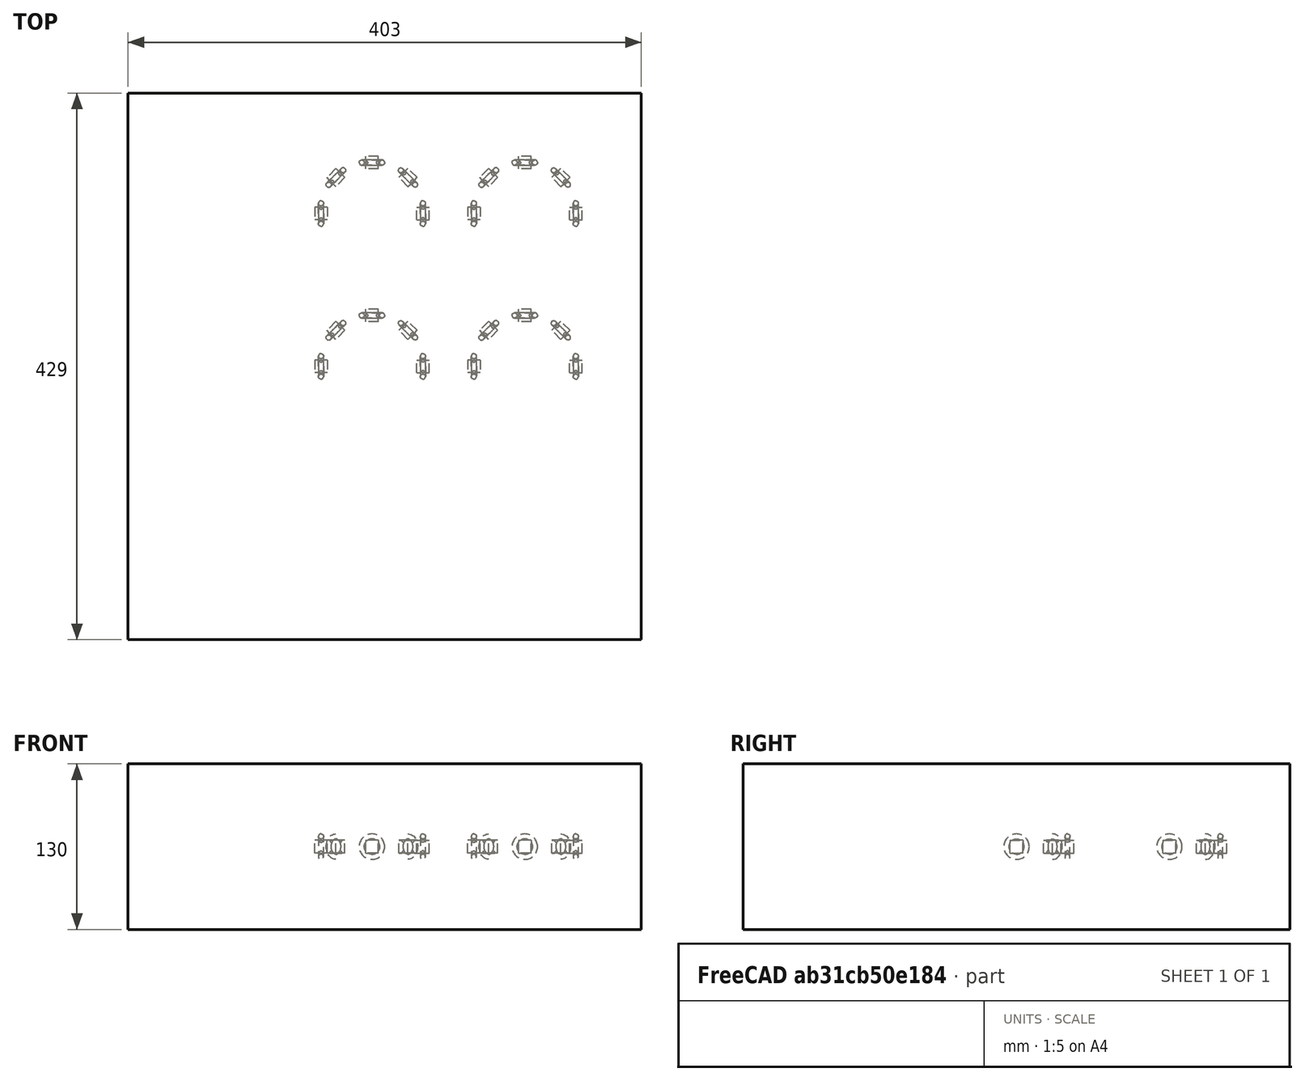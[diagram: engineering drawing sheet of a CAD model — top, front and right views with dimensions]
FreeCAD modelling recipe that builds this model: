
FCSTD DOCUMENT  (FreeCAD 0.21R33694 (Git))
Label: array-of-array-of-solid-offcenter
License: All rights reserved
objects: App::DocumentObjectGroupPython×1251, Part::FeaturePython×5, App::Part×2, Part::MultiFuse×1
note: 5 computed .brp shape members not serialized (recipe doc carries the construction recipe); baked Part::Feature solids carry a one-line shape summary decoded from their .brp

FEATURE [App::DocumentObjectGroupPython] HALFPI  # scripted group (container) (typed FeaturePython)
  name = HALFPI
  value = pi/2.
FEATURE [App::DocumentObjectGroupPython] PI  # scripted group (container) (typed FeaturePython)
  name = PI
  value = 1.*pi
FEATURE [App::DocumentObjectGroupPython] TWOPI  # scripted group (container) (typed FeaturePython)
  name = TWOPI
  value = 2.*pi
FEATURE [App::DocumentObjectGroupPython] Constants  # scripted group (container) (typed FeaturePython)
  Group = -> [HALFPI,PI,TWOPI]
FEATURE [App::DocumentObjectGroupPython] Variables  # scripted group (container) (typed FeaturePython)
FEATURE [App::DocumentObjectGroupPython] Quantities  # scripted group (container) (typed FeaturePython)
FEATURE [App::DocumentObjectGroupPython] Isotopes  # scripted group (container) (typed FeaturePython)
FEATURE [App::DocumentObjectGroupPython] Elements  # scripted group (container) (typed FeaturePython)
FEATURE [App::DocumentObjectGroupPython] Matrix  # scripted group (container) (typed FeaturePython)
FEATURE [App::DocumentObjectGroupPython] Surfaces  # scripted group (container) (typed FeaturePython)
FEATURE [App::DocumentObjectGroupPython] Opticals  # scripted group (container) (typed FeaturePython)
  Group = -> [Matrix,Surfaces]
FEATURE [App::DocumentObjectGroupPython] G4Isotopes  # scripted group (container) (typed FeaturePython)
FEATURE [App::DocumentObjectGroupPython] H_element  # scripted group (container) (typed FeaturePython)
  Z = 1
  atom_value = 1.008
  formula = H
  name = H_element
FEATURE [App::DocumentObjectGroupPython] He_element  # scripted group (container) (typed FeaturePython)
  Z = 2
  atom_value = 4.0026
  formula = He
  name = He_element
FEATURE [App::DocumentObjectGroupPython] Li_element  # scripted group (container) (typed FeaturePython)
  Z = 3
  atom_value = 6.94
  formula = Li
  name = Li_element
FEATURE [App::DocumentObjectGroupPython] Be_element  # scripted group (container) (typed FeaturePython)
  Z = 4
  atom_value = 9.01218
  formula = Be
  name = Be_element
FEATURE [App::DocumentObjectGroupPython] B_element  # scripted group (container) (typed FeaturePython)
  Z = 5
  atom_value = 10.81
  formula = B
  name = B_element
FEATURE [App::DocumentObjectGroupPython] C_element  # scripted group (container) (typed FeaturePython)
  Z = 6
  atom_value = 12.011
  formula = C
  name = C_element
FEATURE [App::DocumentObjectGroupPython] N_element  # scripted group (container) (typed FeaturePython)
  Z = 7
  atom_value = 14.007
  formula = N
  name = N_element
FEATURE [App::DocumentObjectGroupPython] O_element  # scripted group (container) (typed FeaturePython)
  Z = 8
  atom_value = 15.999
  formula = O
  name = O_element
FEATURE [App::DocumentObjectGroupPython] F_element  # scripted group (container) (typed FeaturePython)
  Z = 9
  atom_value = 18.9984
  formula = F
  name = F_element
FEATURE [App::DocumentObjectGroupPython] Ne_element  # scripted group (container) (typed FeaturePython)
  Z = 10
  atom_value = 20.1797
  formula = Ne
  name = Ne_element
FEATURE [App::DocumentObjectGroupPython] Na_element  # scripted group (container) (typed FeaturePython)
  Z = 11
  atom_value = 22.9898
  formula = Na
  name = Na_element
FEATURE [App::DocumentObjectGroupPython] Mg_element  # scripted group (container) (typed FeaturePython)
  Z = 12
  atom_value = 24.305
  formula = Mg
  name = Mg_element
FEATURE [App::DocumentObjectGroupPython] Al_element  # scripted group (container) (typed FeaturePython)
  Z = 13
  atom_value = 26.9815
  formula = Al
  name = Al_element
FEATURE [App::DocumentObjectGroupPython] Si_element  # scripted group (container) (typed FeaturePython)
  Z = 14
  atom_value = 28.085
  formula = Si
  name = Si_element
FEATURE [App::DocumentObjectGroupPython] P_element  # scripted group (container) (typed FeaturePython)
  Z = 15
  atom_value = 30.9738
  formula = P
  name = P_element
FEATURE [App::DocumentObjectGroupPython] S_element  # scripted group (container) (typed FeaturePython)
  Z = 16
  atom_value = 32.06
  formula = S
  name = S_element
FEATURE [App::DocumentObjectGroupPython] Cl_element  # scripted group (container) (typed FeaturePython)
  Z = 17
  atom_value = 35.45
  formula = Cl
  name = Cl_element
FEATURE [App::DocumentObjectGroupPython] Ar_element  # scripted group (container) (typed FeaturePython)
  Z = 18
  atom_value = 39.95
  formula = Ar
  name = Ar_element
FEATURE [App::DocumentObjectGroupPython] K_element  # scripted group (container) (typed FeaturePython)
  Z = 19
  atom_value = 39.0983
  formula = K
  name = K_element
FEATURE [App::DocumentObjectGroupPython] Ca_element  # scripted group (container) (typed FeaturePython)
  Z = 20
  atom_value = 40.078
  formula = Ca
  name = Ca_element
FEATURE [App::DocumentObjectGroupPython] Sc_element  # scripted group (container) (typed FeaturePython)
  Z = 21
  atom_value = 44.9559
  formula = Sc
  name = Sc_element
FEATURE [App::DocumentObjectGroupPython] Ti_element  # scripted group (container) (typed FeaturePython)
  Z = 22
  atom_value = 47.867
  formula = Ti
  name = Ti_element
FEATURE [App::DocumentObjectGroupPython] V_element  # scripted group (container) (typed FeaturePython)
  Z = 23
  atom_value = 50.9415
  formula = V
  name = V_element
FEATURE [App::DocumentObjectGroupPython] Cr_element  # scripted group (container) (typed FeaturePython)
  Z = 24
  atom_value = 51.9961
  formula = Cr
  name = Cr_element
FEATURE [App::DocumentObjectGroupPython] Mn_element  # scripted group (container) (typed FeaturePython)
  Z = 25
  atom_value = 54.938
  formula = Mn
  name = Mn_element
FEATURE [App::DocumentObjectGroupPython] Fe_element  # scripted group (container) (typed FeaturePython)
  Z = 26
  atom_value = 55.845
  formula = Fe
  name = Fe_element
FEATURE [App::DocumentObjectGroupPython] Co_element  # scripted group (container) (typed FeaturePython)
  Z = 27
  atom_value = 58.9332
  formula = Co
  name = Co_element
FEATURE [App::DocumentObjectGroupPython] Ni_element  # scripted group (container) (typed FeaturePython)
  Z = 28
  atom_value = 58.6934
  formula = Ni
  name = Ni_element
FEATURE [App::DocumentObjectGroupPython] Cu_element  # scripted group (container) (typed FeaturePython)
  Z = 29
  atom_value = 63.546
  formula = Cu
  name = Cu_element
FEATURE [App::DocumentObjectGroupPython] Zn_element  # scripted group (container) (typed FeaturePython)
  Z = 30
  atom_value = 65.38
  formula = Zn
  name = Zn_element
FEATURE [App::DocumentObjectGroupPython] Ga_element  # scripted group (container) (typed FeaturePython)
  Z = 31
  atom_value = 69.723
  formula = Ga
  name = Ga_element
FEATURE [App::DocumentObjectGroupPython] Ge_element  # scripted group (container) (typed FeaturePython)
  Z = 32
  atom_value = 72.63
  formula = Ge
  name = Ge_element
FEATURE [App::DocumentObjectGroupPython] As_element  # scripted group (container) (typed FeaturePython)
  Z = 33
  atom_value = 74.9216
  formula = As
  name = As_element
FEATURE [App::DocumentObjectGroupPython] Se_element  # scripted group (container) (typed FeaturePython)
  Z = 34
  atom_value = 78.971
  formula = Se
  name = Se_element
FEATURE [App::DocumentObjectGroupPython] Br_element  # scripted group (container) (typed FeaturePython)
  Z = 35
  atom_value = 79.904
  formula = Br
  name = Br_element
FEATURE [App::DocumentObjectGroupPython] Kr_element  # scripted group (container) (typed FeaturePython)
  Z = 36
  atom_value = 83.798
  formula = Kr
  name = Kr_element
FEATURE [App::DocumentObjectGroupPython] Rb_element  # scripted group (container) (typed FeaturePython)
  Z = 37
  atom_value = 85.4678
  formula = Rb
  name = Rb_element
FEATURE [App::DocumentObjectGroupPython] Sr_element  # scripted group (container) (typed FeaturePython)
  Z = 38
  atom_value = 87.62
  formula = Sr
  name = Sr_element
FEATURE [App::DocumentObjectGroupPython] Y_element  # scripted group (container) (typed FeaturePython)
  Z = 39
  atom_value = 88.9058
  formula = Y
  name = Y_element
FEATURE [App::DocumentObjectGroupPython] Zr_element  # scripted group (container) (typed FeaturePython)
  Z = 40
  atom_value = 91.224
  formula = Zr
  name = Zr_element
FEATURE [App::DocumentObjectGroupPython] Nb_element  # scripted group (container) (typed FeaturePython)
  Z = 41
  atom_value = 92.9064
  formula = Nb
  name = Nb_element
FEATURE [App::DocumentObjectGroupPython] Mo_element  # scripted group (container) (typed FeaturePython)
  Z = 42
  atom_value = 95.95
  formula = Mo
  name = Mo_element
FEATURE [App::DocumentObjectGroupPython] Tc_element  # scripted group (container) (typed FeaturePython)
  Z = 43
  atom_value = 97
  formula = Tc
  name = Tc_element
FEATURE [App::DocumentObjectGroupPython] Ru_element  # scripted group (container) (typed FeaturePython)
  Z = 44
  atom_value = 101.07
  formula = Ru
  name = Ru_element
FEATURE [App::DocumentObjectGroupPython] Rh_element  # scripted group (container) (typed FeaturePython)
  Z = 45
  atom_value = 102.905
  formula = Rh
  name = Rh_element
FEATURE [App::DocumentObjectGroupPython] Pd_element  # scripted group (container) (typed FeaturePython)
  Z = 46
  atom_value = 106.42
  formula = Pd
  name = Pd_element
FEATURE [App::DocumentObjectGroupPython] Ag_element  # scripted group (container) (typed FeaturePython)
  Z = 47
  atom_value = 107.868
  formula = Ag
  name = Ag_element
FEATURE [App::DocumentObjectGroupPython] Cd_element  # scripted group (container) (typed FeaturePython)
  Z = 48
  atom_value = 112.414
  formula = Cd
  name = Cd_element
FEATURE [App::DocumentObjectGroupPython] In_element  # scripted group (container) (typed FeaturePython)
  Z = 49
  atom_value = 114.818
  formula = In
  name = In_element
FEATURE [App::DocumentObjectGroupPython] Sn_element  # scripted group (container) (typed FeaturePython)
  Z = 50
  atom_value = 118.71
  formula = Sn
  name = Sn_element
FEATURE [App::DocumentObjectGroupPython] Sb_element  # scripted group (container) (typed FeaturePython)
  Z = 51
  atom_value = 121.76
  formula = Sb
  name = Sb_element
FEATURE [App::DocumentObjectGroupPython] Te_element  # scripted group (container) (typed FeaturePython)
  Z = 52
  atom_value = 127.6
  formula = Te
  name = Te_element
FEATURE [App::DocumentObjectGroupPython] I_element  # scripted group (container) (typed FeaturePython)
  Z = 53
  atom_value = 126.904
  formula = I
  name = I_element
FEATURE [App::DocumentObjectGroupPython] Xe_element  # scripted group (container) (typed FeaturePython)
  Z = 54
  atom_value = 131.293
  formula = Xe
  name = Xe_element
FEATURE [App::DocumentObjectGroupPython] Cs_element  # scripted group (container) (typed FeaturePython)
  Z = 55
  atom_value = 132.905
  formula = Cs
  name = Cs_element
FEATURE [App::DocumentObjectGroupPython] Ba_element  # scripted group (container) (typed FeaturePython)
  Z = 56
  atom_value = 137.327
  formula = Ba
  name = Ba_element
FEATURE [App::DocumentObjectGroupPython] La_element  # scripted group (container) (typed FeaturePython)
  Z = 57
  atom_value = 138.905
  formula = La
  name = La_element
FEATURE [App::DocumentObjectGroupPython] Ce_element  # scripted group (container) (typed FeaturePython)
  Z = 58
  atom_value = 140.116
  formula = Ce
  name = Ce_element
FEATURE [App::DocumentObjectGroupPython] Pr_element  # scripted group (container) (typed FeaturePython)
  Z = 59
  atom_value = 140.908
  formula = Pr
  name = Pr_element
FEATURE [App::DocumentObjectGroupPython] Nd_element  # scripted group (container) (typed FeaturePython)
  Z = 60
  atom_value = 144.242
  formula = Nd
  name = Nd_element
FEATURE [App::DocumentObjectGroupPython] Pm_element  # scripted group (container) (typed FeaturePython)
  Z = 61
  atom_value = 145
  formula = Pm
  name = Pm_element
FEATURE [App::DocumentObjectGroupPython] Sm_element  # scripted group (container) (typed FeaturePython)
  Z = 62
  atom_value = 150.36
  formula = Sm
  name = Sm_element
FEATURE [App::DocumentObjectGroupPython] Eu_element  # scripted group (container) (typed FeaturePython)
  Z = 63
  atom_value = 151.964
  formula = Eu
  name = Eu_element
FEATURE [App::DocumentObjectGroupPython] Gd_element  # scripted group (container) (typed FeaturePython)
  Z = 64
  atom_value = 157.25
  formula = Gd
  name = Gd_element
FEATURE [App::DocumentObjectGroupPython] Tb_element  # scripted group (container) (typed FeaturePython)
  Z = 65
  atom_value = 158.925
  formula = Tb
  name = Tb_element
FEATURE [App::DocumentObjectGroupPython] Dy_element  # scripted group (container) (typed FeaturePython)
  Z = 66
  atom_value = 162.5
  formula = Dy
  name = Dy_element
FEATURE [App::DocumentObjectGroupPython] Ho_element  # scripted group (container) (typed FeaturePython)
  Z = 67
  atom_value = 164.93
  formula = Ho
  name = Ho_element
FEATURE [App::DocumentObjectGroupPython] Er_element  # scripted group (container) (typed FeaturePython)
  Z = 68
  atom_value = 167.259
  formula = Er
  name = Er_element
FEATURE [App::DocumentObjectGroupPython] Tm_element  # scripted group (container) (typed FeaturePython)
  Z = 69
  atom_value = 168.934
  formula = Tm
  name = Tm_element
FEATURE [App::DocumentObjectGroupPython] Yb_element  # scripted group (container) (typed FeaturePython)
  Z = 70
  atom_value = 173.045
  formula = Yb
  name = Yb_element
FEATURE [App::DocumentObjectGroupPython] Lu_element  # scripted group (container) (typed FeaturePython)
  Z = 71
  atom_value = 174.967
  formula = Lu
  name = Lu_element
FEATURE [App::DocumentObjectGroupPython] Hf_element  # scripted group (container) (typed FeaturePython)
  Z = 72
  atom_value = 178.49
  formula = Hf
  name = Hf_element
FEATURE [App::DocumentObjectGroupPython] Ta_element  # scripted group (container) (typed FeaturePython)
  Z = 73
  atom_value = 180.948
  formula = Ta
  name = Ta_element
FEATURE [App::DocumentObjectGroupPython] W_element  # scripted group (container) (typed FeaturePython)
  Z = 74
  atom_value = 183.84
  formula = W
  name = W_element
FEATURE [App::DocumentObjectGroupPython] Re_element  # scripted group (container) (typed FeaturePython)
  Z = 75
  atom_value = 186.207
  formula = Re
  name = Re_element
FEATURE [App::DocumentObjectGroupPython] Os_element  # scripted group (container) (typed FeaturePython)
  Z = 76
  atom_value = 190.23
  formula = Os
  name = Os_element
FEATURE [App::DocumentObjectGroupPython] Ir_element  # scripted group (container) (typed FeaturePython)
  Z = 77
  atom_value = 192.217
  formula = Ir
  name = Ir_element
FEATURE [App::DocumentObjectGroupPython] Pt_element  # scripted group (container) (typed FeaturePython)
  Z = 78
  atom_value = 195.084
  formula = Pt
  name = Pt_element
FEATURE [App::DocumentObjectGroupPython] Au_element  # scripted group (container) (typed FeaturePython)
  Z = 79
  atom_value = 196.967
  formula = Au
  name = Au_element
FEATURE [App::DocumentObjectGroupPython] Hg_element  # scripted group (container) (typed FeaturePython)
  Z = 80
  atom_value = 200.592
  formula = Hg
  name = Hg_element
FEATURE [App::DocumentObjectGroupPython] Tl_element  # scripted group (container) (typed FeaturePython)
  Z = 81
  atom_value = 204.38
  formula = Tl
  name = Tl_element
FEATURE [App::DocumentObjectGroupPython] Pb_element  # scripted group (container) (typed FeaturePython)
  Z = 82
  atom_value = 207.2
  formula = Pb
  name = Pb_element
FEATURE [App::DocumentObjectGroupPython] Bi_element  # scripted group (container) (typed FeaturePython)
  Z = 83
  atom_value = 208.98
  formula = Bi
  name = Bi_element
FEATURE [App::DocumentObjectGroupPython] Po_element  # scripted group (container) (typed FeaturePython)
  Z = 84
  atom_value = 209
  formula = Po
  name = Po_element
FEATURE [App::DocumentObjectGroupPython] At_element  # scripted group (container) (typed FeaturePython)
  Z = 85
  atom_value = 210
  formula = At
  name = At_element
FEATURE [App::DocumentObjectGroupPython] Rn_element  # scripted group (container) (typed FeaturePython)
  Z = 86
  atom_value = 222
  formula = Rn
  name = Rn_element
FEATURE [App::DocumentObjectGroupPython] Fr_element  # scripted group (container) (typed FeaturePython)
  Z = 87
  atom_value = 223
  formula = Fr
  name = Fr_element
FEATURE [App::DocumentObjectGroupPython] Ra_element  # scripted group (container) (typed FeaturePython)
  Z = 88
  atom_value = 226
  formula = Ra
  name = Ra_element
FEATURE [App::DocumentObjectGroupPython] Ac_element  # scripted group (container) (typed FeaturePython)
  Z = 89
  atom_value = 227
  formula = Ac
  name = Ac_element
FEATURE [App::DocumentObjectGroupPython] Th_element  # scripted group (container) (typed FeaturePython)
  Z = 90
  atom_value = 232.038
  formula = Th
  name = Th_element
FEATURE [App::DocumentObjectGroupPython] Pa_element  # scripted group (container) (typed FeaturePython)
  Z = 91
  atom_value = 231.036
  formula = Pa
  name = Pa_element
FEATURE [App::DocumentObjectGroupPython] U_element  # scripted group (container) (typed FeaturePython)
  Z = 92
  atom_value = 238.029
  formula = U
  name = U_element
FEATURE [App::DocumentObjectGroupPython] Np_element  # scripted group (container) (typed FeaturePython)
  Z = 93
  atom_value = 237
  formula = Np
  name = Np_element
FEATURE [App::DocumentObjectGroupPython] Pu_element  # scripted group (container) (typed FeaturePython)
  Z = 94
  atom_value = 244
  formula = Pu
  name = Pu_element
FEATURE [App::DocumentObjectGroupPython] Am_element  # scripted group (container) (typed FeaturePython)
  Z = 95
  atom_value = 243
  formula = Am
  name = Am_element
FEATURE [App::DocumentObjectGroupPython] Cm_element  # scripted group (container) (typed FeaturePython)
  Z = 96
  atom_value = 247
  formula = Cm
  name = Cm_element
FEATURE [App::DocumentObjectGroupPython] Bk_element  # scripted group (container) (typed FeaturePython)
  Z = 97
  atom_value = 247
  formula = Bk
  name = Bk_element
FEATURE [App::DocumentObjectGroupPython] Cf_element  # scripted group (container) (typed FeaturePython)
  Z = 98
  atom_value = 251
  formula = Cf
  name = Cf_element
FEATURE [App::DocumentObjectGroupPython] G4Elements  # scripted group (container) (typed FeaturePython)
  Group = -> [H_element,He_element,Li_element,Be_element,B_element,C_element,N_element,O_element,F_element,Ne_element,Na_element,Mg_element,Al_element,Si_element,P_element,S_element,Cl_element,Ar_element,K_element,Ca_element,Sc_element,Ti_element,V_element,Cr_element,Mn_element,Fe_element,Co_element,Ni_element,Cu_element,Zn_element,Ga_element,Ge_element,As_element,Se_element,Br_element,Kr_element,Rb_element,+61 more]
FEATURE [App::DocumentObjectGroupPython] H_element001  label="H_element : 0.101"  # scripted group (container) (typed FeaturePython)
  n = 0.101327
FEATURE [App::DocumentObjectGroupPython] C_element001  label="C_element : 0.775"  # scripted group (container) (typed FeaturePython)
  n = 0.7755
FEATURE [App::DocumentObjectGroupPython] N_element001  label="N_element : 0.035"  # scripted group (container) (typed FeaturePython)
  n = 0.035057
FEATURE [App::DocumentObjectGroupPython] O_element001  label="O_element : 0.052"  # scripted group (container) (typed FeaturePython)
  n = 0.0523159
FEATURE [App::DocumentObjectGroupPython] F_element001  label="F_element : 0.017"  # scripted group (container) (typed FeaturePython)
  n = 0.017422
FEATURE [App::DocumentObjectGroupPython] Ca_element001  label="Ca_element : 0.018"  # scripted group (container) (typed FeaturePython)
  n = 0.018378
FEATURE [App::DocumentObjectGroupPython] G4_A_150_TISSUE  label="G4_A-150_TISSUE"  # scripted group (container) (typed FeaturePython)
  Dunit = g/cm3
  Dvalue = 1.127
  Group = -> [H_element001,C_element001,N_element001,O_element001,F_element001,Ca_element001]
  conduct = 2
  density = 1
  expand = 3
  formula = G4_A-150_TISSUE
  name = G4_A-150_TISSUE
  specific = 4
FEATURE [App::DocumentObjectGroupPython] C_element002  label="C_element : 3"  # scripted group (container) (typed FeaturePython)
  n = 3
  ref = C_element
FEATURE [App::DocumentObjectGroupPython] H_element002  label="H_element : 6"  # scripted group (container) (typed FeaturePython)
  n = 6
  ref = H_element
FEATURE [App::DocumentObjectGroupPython] O_element002  label="O_element : 1"  # scripted group (container) (typed FeaturePython)
  n = 1
  ref = O_element
FEATURE [App::DocumentObjectGroupPython] G4_ACETONE  # scripted group (container) (typed FeaturePython)
  Dunit = g/cm3
  Dvalue = 0.7899
  Group = -> [C_element002,H_element002,O_element002]
  conduct = 2
  density = 1
  expand = 3
  formula = G4_ACETONE
  name = G4_ACETONE
  specific = 4
FEATURE [App::DocumentObjectGroupPython] C_element003  label="C_element : 2"  # scripted group (container) (typed FeaturePython)
  n = 2
  ref = C_element
FEATURE [App::DocumentObjectGroupPython] H_element003  label="H_element : 2"  # scripted group (container) (typed FeaturePython)
  n = 2
  ref = H_element
FEATURE [App::DocumentObjectGroupPython] G4_ACETYLENE  # scripted group (container) (typed FeaturePython)
  Dunit = g/cm3
  Dvalue = 0.0010967
  Group = -> [C_element003,H_element003]
  conduct = 2
  density = 1
  expand = 3
  formula = G4_ACETYLENE
  name = G4_ACETYLENE
  specific = 4
FEATURE [App::DocumentObjectGroupPython] C_element004  label="C_element : 5"  # scripted group (container) (typed FeaturePython)
  n = 5
  ref = C_element
FEATURE [App::DocumentObjectGroupPython] H_element004  label="H_element : 5"  # scripted group (container) (typed FeaturePython)
  n = 5
  ref = H_element
FEATURE [App::DocumentObjectGroupPython] N_element002  label="N_element : 5"  # scripted group (container) (typed FeaturePython)
  n = 5
  ref = N_element
FEATURE [App::DocumentObjectGroupPython] G4_ADENINE  # scripted group (container) (typed FeaturePython)
  Dunit = g/cm3
  Dvalue = 1.6
  Group = -> [C_element004,H_element004,N_element002]
  conduct = 2
  density = 1
  expand = 3
  formula = G4_ADENINE
  name = G4_ADENINE
  specific = 4
FEATURE [App::DocumentObjectGroupPython] H_element005  label="H_element : 0.114"  # scripted group (container) (typed FeaturePython)
  n = 0.114
FEATURE [App::DocumentObjectGroupPython] C_element005  label="C_element : 0.598"  # scripted group (container) (typed FeaturePython)
  n = 0.598
FEATURE [App::DocumentObjectGroupPython] N_element003  label="N_element : 0.007"  # scripted group (container) (typed FeaturePython)
  n = 0.007
FEATURE [App::DocumentObjectGroupPython] O_element003  label="O_element : 0.278"  # scripted group (container) (typed FeaturePython)
  n = 0.278
FEATURE [App::DocumentObjectGroupPython] Na_element001  label="Na_element : 0.001"  # scripted group (container) (typed FeaturePython)
  n = 0.001
FEATURE [App::DocumentObjectGroupPython] S_element001  label="S_element : 0.001"  # scripted group (container) (typed FeaturePython)
  n = 0.001
FEATURE [App::DocumentObjectGroupPython] Cl_element001  label="Cl_element : 0.001"  # scripted group (container) (typed FeaturePython)
  n = 0.001
FEATURE [App::DocumentObjectGroupPython] G4_ADIPOSE_TISSUE_ICRP  # scripted group (container) (typed FeaturePython)
  Dunit = g/cm3
  Dvalue = 0.95
  Group = -> [H_element005,C_element005,N_element003,O_element003,Na_element001,S_element001,Cl_element001]
  conduct = 2
  density = 1
  expand = 3
  formula = G4_ADIPOSE_TISSUE_ICRP
  name = G4_ADIPOSE_TISSUE_ICRP
  specific = 4
FEATURE [App::DocumentObjectGroupPython] C_element006  label="C_element : 0.000"  # scripted group (container) (typed FeaturePython)
  n = 0.000124
FEATURE [App::DocumentObjectGroupPython] N_element004  label="N_element : 0.755"  # scripted group (container) (typed FeaturePython)
  n = 0.755268
FEATURE [App::DocumentObjectGroupPython] O_element004  label="O_element : 0.232"  # scripted group (container) (typed FeaturePython)
  n = 0.231781
FEATURE [App::DocumentObjectGroupPython] Ar_element001  label="Ar_element : 0.013"  # scripted group (container) (typed FeaturePython)
  n = 0.012827
FEATURE [App::DocumentObjectGroupPython] G4_AIR  # scripted group (container) (typed FeaturePython)
  Dunit = g/cm3
  Dvalue = 0.00120479
  Group = -> [C_element006,N_element004,O_element004,Ar_element001]
  conduct = 2
  density = 1
  expand = 3
  formula = G4_AIR
  name = G4_AIR
  specific = 4
FEATURE [App::DocumentObjectGroupPython] C_element007  label="C_element : 006"  # scripted group (container) (typed FeaturePython)
  n = 3
  ref = C_element
FEATURE [App::DocumentObjectGroupPython] H_element006  label="H_element : 7"  # scripted group (container) (typed FeaturePython)
  n = 7
  ref = H_element
FEATURE [App::DocumentObjectGroupPython] N_element005  label="N_element : 1"  # scripted group (container) (typed FeaturePython)
  n = 1
  ref = N_element
FEATURE [App::DocumentObjectGroupPython] O_element005  label="O_element : 2"  # scripted group (container) (typed FeaturePython)
  n = 2
  ref = O_element
FEATURE [App::DocumentObjectGroupPython] G4_ALANINE  # scripted group (container) (typed FeaturePython)
  Dunit = g/cm3
  Dvalue = 1.42
  Group = -> [C_element007,H_element006,N_element005,O_element005]
  conduct = 2
  density = 1
  expand = 3
  formula = G4_ALANINE
  name = G4_ALANINE
  specific = 4
FEATURE [App::DocumentObjectGroupPython] Al_element001  label="Al_element : 2"  # scripted group (container) (typed FeaturePython)
  n = 2
  ref = Al_element
FEATURE [App::DocumentObjectGroupPython] O_element006  label="O_element : 3"  # scripted group (container) (typed FeaturePython)
  n = 3
  ref = O_element
FEATURE [App::DocumentObjectGroupPython] G4_ALUMINUM_OXIDE  # scripted group (container) (typed FeaturePython)
  Dunit = g/cm3
  Dvalue = 3.97
  Group = -> [Al_element001,O_element006]
  conduct = 2
  density = 1
  expand = 3
  formula = G4_ALUMINUM_OXIDE
  name = G4_ALUMINUM_OXIDE
  specific = 4
FEATURE [App::DocumentObjectGroupPython] H_element007  label="H_element : 0.106"  # scripted group (container) (typed FeaturePython)
  n = 0.10593
FEATURE [App::DocumentObjectGroupPython] C_element008  label="C_element : 0.789"  # scripted group (container) (typed FeaturePython)
  n = 0.788974
FEATURE [App::DocumentObjectGroupPython] O_element007  label="O_element : 0.105"  # scripted group (container) (typed FeaturePython)
  n = 0.105096
FEATURE [App::DocumentObjectGroupPython] G4_AMBER  # scripted group (container) (typed FeaturePython)
  Dunit = g/cm3
  Dvalue = 1.1
  Group = -> [H_element007,C_element008,O_element007]
  conduct = 2
  density = 1
  expand = 3
  formula = G4_AMBER
  name = G4_AMBER
  specific = 4
FEATURE [App::DocumentObjectGroupPython] N_element006  label="N_element : 006"  # scripted group (container) (typed FeaturePython)
  n = 1
  ref = N_element
FEATURE [App::DocumentObjectGroupPython] H_element008  label="H_element : 3"  # scripted group (container) (typed FeaturePython)
  n = 3
  ref = H_element
FEATURE [App::DocumentObjectGroupPython] G4_AMMONIA  # scripted group (container) (typed FeaturePython)
  Dunit = g/cm3
  Dvalue = 0.000826019
  Group = -> [N_element006,H_element008]
  conduct = 2
  density = 1
  expand = 3
  formula = G4_AMMONIA
  name = G4_AMMONIA
  specific = 4
FEATURE [App::DocumentObjectGroupPython] C_element009  label="C_element : 6"  # scripted group (container) (typed FeaturePython)
  n = 6
  ref = C_element
FEATURE [App::DocumentObjectGroupPython] H_element009  label="H_element : 008"  # scripted group (container) (typed FeaturePython)
  n = 7
  ref = H_element
FEATURE [App::DocumentObjectGroupPython] N_element007  label="N_element : 007"  # scripted group (container) (typed FeaturePython)
  n = 1
  ref = N_element
FEATURE [App::DocumentObjectGroupPython] G4_ANILINE  # scripted group (container) (typed FeaturePython)
  Dunit = g/cm3
  Dvalue = 1.0235
  Group = -> [C_element009,H_element009,N_element007]
  conduct = 2
  density = 1
  expand = 3
  formula = G4_ANILINE
  name = G4_ANILINE
  specific = 4
FEATURE [App::DocumentObjectGroupPython] C_element010  label="C_element : 14"  # scripted group (container) (typed FeaturePython)
  n = 14
  ref = C_element
FEATURE [App::DocumentObjectGroupPython] H_element010  label="H_element : 10"  # scripted group (container) (typed FeaturePython)
  n = 10
  ref = H_element
FEATURE [App::DocumentObjectGroupPython] G4_ANTHRACENE  # scripted group (container) (typed FeaturePython)
  Dunit = g/cm3
  Dvalue = 1.283
  Group = -> [C_element010,H_element010]
  conduct = 2
  density = 1
  expand = 3
  formula = G4_ANTHRACENE
  name = G4_ANTHRACENE
  specific = 4
FEATURE [App::DocumentObjectGroupPython] H_element011  label="H_element : 0.065"  # scripted group (container) (typed FeaturePython)
  n = 0.0654709
FEATURE [App::DocumentObjectGroupPython] C_element011  label="C_element : 0.537"  # scripted group (container) (typed FeaturePython)
  n = 0.536944
FEATURE [App::DocumentObjectGroupPython] N_element008  label="N_element : 0.021"  # scripted group (container) (typed FeaturePython)
  n = 0.0215
FEATURE [App::DocumentObjectGroupPython] O_element008  label="O_element : 0.032"  # scripted group (container) (typed FeaturePython)
  n = 0.032085
FEATURE [App::DocumentObjectGroupPython] F_element002  label="F_element : 0.167"  # scripted group (container) (typed FeaturePython)
  n = 0.167411
FEATURE [App::DocumentObjectGroupPython] Ca_element002  label="Ca_element : 0.177"  # scripted group (container) (typed FeaturePython)
  n = 0.176589
FEATURE [App::DocumentObjectGroupPython] G4_B_100_BONE  label="G4_B-100_BONE"  # scripted group (container) (typed FeaturePython)
  Dunit = g/cm3
  Dvalue = 1.45
  Group = -> [H_element011,C_element011,N_element008,O_element008,F_element002,Ca_element002]
  conduct = 2
  density = 1
  expand = 3
  formula = G4_B-100_BONE
  name = G4_B-100_BONE
  specific = 4
FEATURE [App::DocumentObjectGroupPython] H_element012  label="H_element : 0.057"  # scripted group (container) (typed FeaturePython)
  n = 0.057441
FEATURE [App::DocumentObjectGroupPython] C_element012  label="C_element : 0.790"  # scripted group (container) (typed FeaturePython)
  n = 0.774591
FEATURE [App::DocumentObjectGroupPython] O_element009  label="O_element : 0.168"  # scripted group (container) (typed FeaturePython)
  n = 0.167968
FEATURE [App::DocumentObjectGroupPython] G4_BAKELITE  # scripted group (container) (typed FeaturePython)
  Dunit = g/cm3
  Dvalue = 1.25
  Group = -> [H_element012,C_element012,O_element009]
  conduct = 2
  density = 1
  expand = 3
  formula = G4_BAKELITE
  name = G4_BAKELITE
  specific = 4
FEATURE [App::DocumentObjectGroupPython] Ba_element001  label="Ba_element : 1"  # scripted group (container) (typed FeaturePython)
  n = 1
  ref = Ba_element
FEATURE [App::DocumentObjectGroupPython] F_element003  label="F_element : 2"  # scripted group (container) (typed FeaturePython)
  n = 2
  ref = F_element
FEATURE [App::DocumentObjectGroupPython] G4_BARIUM_FLUORIDE  # scripted group (container) (typed FeaturePython)
  Dunit = g/cm3
  Dvalue = 4.89
  Group = -> [Ba_element001,F_element003]
  conduct = 2
  density = 1
  expand = 3
  formula = G4_BARIUM_FLUORIDE
  name = G4_BARIUM_FLUORIDE
  specific = 4
FEATURE [App::DocumentObjectGroupPython] Ba_element002  label="Ba_element : 002"  # scripted group (container) (typed FeaturePython)
  n = 1
  ref = Ba_element
FEATURE [App::DocumentObjectGroupPython] S_element002  label="S_element : 1"  # scripted group (container) (typed FeaturePython)
  n = 1
  ref = S_element
FEATURE [App::DocumentObjectGroupPython] O_element010  label="O_element : 4"  # scripted group (container) (typed FeaturePython)
  n = 4
  ref = O_element
FEATURE [App::DocumentObjectGroupPython] G4_BARIUM_SULFATE  # scripted group (container) (typed FeaturePython)
  Dunit = g/cm3
  Dvalue = 4.5
  Group = -> [Ba_element002,S_element002,O_element010]
  conduct = 2
  density = 1
  expand = 3
  formula = G4_BARIUM_SULFATE
  name = G4_BARIUM_SULFATE
  specific = 4
FEATURE [App::DocumentObjectGroupPython] C_element013  label="C_element : 007"  # scripted group (container) (typed FeaturePython)
  n = 6
  ref = C_element
FEATURE [App::DocumentObjectGroupPython] H_element013  label="H_element : 009"  # scripted group (container) (typed FeaturePython)
  n = 6
  ref = H_element
FEATURE [App::DocumentObjectGroupPython] G4_BENZENE  # scripted group (container) (typed FeaturePython)
  Dunit = g/cm3
  Dvalue = 0.87865
  Group = -> [C_element013,H_element013]
  conduct = 2
  density = 1
  expand = 3
  formula = G4_BENZENE
  name = G4_BENZENE
  specific = 4
FEATURE [App::DocumentObjectGroupPython] Be_element001  label="Be_element : 1"  # scripted group (container) (typed FeaturePython)
  n = 1
  ref = Be_element
FEATURE [App::DocumentObjectGroupPython] O_element011  label="O_element : 005"  # scripted group (container) (typed FeaturePython)
  n = 1
  ref = O_element
FEATURE [App::DocumentObjectGroupPython] G4_BERYLLIUM_OXIDE  # scripted group (container) (typed FeaturePython)
  Dunit = g/cm3
  Dvalue = 3.01
  Group = -> [Be_element001,O_element011]
  conduct = 2
  density = 1
  expand = 3
  formula = G4_BERYLLIUM_OXIDE
  name = G4_BERYLLIUM_OXIDE
  specific = 4
FEATURE [App::DocumentObjectGroupPython] Bi_element001  label="Bi_element : 4"  # scripted group (container) (typed FeaturePython)
  n = 4
  ref = Bi_element
FEATURE [App::DocumentObjectGroupPython] Ge_element001  label="Ge_element : 3"  # scripted group (container) (typed FeaturePython)
  n = 3
  ref = Ge_element
FEATURE [App::DocumentObjectGroupPython] O_element012  label="O_element : 12"  # scripted group (container) (typed FeaturePython)
  n = 12
  ref = O_element
FEATURE [App::DocumentObjectGroupPython] G4_BGO  # scripted group (container) (typed FeaturePython)
  Dunit = g/cm3
  Dvalue = 7.13
  Group = -> [Bi_element001,Ge_element001,O_element012]
  conduct = 2
  density = 1
  expand = 3
  formula = G4_BGO
  name = G4_BGO
  specific = 4
FEATURE [App::DocumentObjectGroupPython] H_element014  label="H_element : 0.102"  # scripted group (container) (typed FeaturePython)
  n = 0.102
FEATURE [App::DocumentObjectGroupPython] C_element014  label="C_element : 0.110"  # scripted group (container) (typed FeaturePython)
  n = 0.11
FEATURE [App::DocumentObjectGroupPython] N_element009  label="N_element : 0.033"  # scripted group (container) (typed FeaturePython)
  n = 0.033
FEATURE [App::DocumentObjectGroupPython] O_element013  label="O_element : 0.745"  # scripted group (container) (typed FeaturePython)
  n = 0.745
FEATURE [App::DocumentObjectGroupPython] Na_element002  label="Na_element : 0.002"  # scripted group (container) (typed FeaturePython)
  n = 0.001
FEATURE [App::DocumentObjectGroupPython] P_element001  label="P_element : 0.001"  # scripted group (container) (typed FeaturePython)
  n = 0.001
FEATURE [App::DocumentObjectGroupPython] S_element003  label="S_element : 0.002"  # scripted group (container) (typed FeaturePython)
  n = 0.002
FEATURE [App::DocumentObjectGroupPython] Cl_element002  label="Cl_element : 0.003"  # scripted group (container) (typed FeaturePython)
  n = 0.003
FEATURE [App::DocumentObjectGroupPython] K_element001  label="K_element : 0.002"  # scripted group (container) (typed FeaturePython)
  n = 0.002
FEATURE [App::DocumentObjectGroupPython] Fe_element001  label="Fe_element : 0.001"  # scripted group (container) (typed FeaturePython)
  n = 0.001
FEATURE [App::DocumentObjectGroupPython] G4_BLOOD_ICRP  # scripted group (container) (typed FeaturePython)
  Dunit = g/cm3
  Dvalue = 1.06
  Group = -> [H_element014,C_element014,N_element009,O_element013,Na_element002,P_element001,S_element003,Cl_element002,K_element001,Fe_element001]
  conduct = 2
  density = 1
  expand = 3
  formula = G4_BLOOD_ICRP
  name = G4_BLOOD_ICRP
  specific = 4
FEATURE [App::DocumentObjectGroupPython] H_element015  label="H_element : 0.064"  # scripted group (container) (typed FeaturePython)
  n = 0.064
FEATURE [App::DocumentObjectGroupPython] C_element015  label="C_element : 0.278"  # scripted group (container) (typed FeaturePython)
  n = 0.278
FEATURE [App::DocumentObjectGroupPython] N_element010  label="N_element : 0.027"  # scripted group (container) (typed FeaturePython)
  n = 0.027
FEATURE [App::DocumentObjectGroupPython] O_element014  label="O_element : 0.410"  # scripted group (container) (typed FeaturePython)
  n = 0.41
FEATURE [App::DocumentObjectGroupPython] Mg_element001  label="Mg_element : 0.002"  # scripted group (container) (typed FeaturePython)
  n = 0.002
FEATURE [App::DocumentObjectGroupPython] P_element002  label="P_element : 0.070"  # scripted group (container) (typed FeaturePython)
  n = 0.07
FEATURE [App::DocumentObjectGroupPython] S_element004  label="S_element : 0.003"  # scripted group (container) (typed FeaturePython)
  n = 0.002
FEATURE [App::DocumentObjectGroupPython] Ca_element003  label="Ca_element : 0.147"  # scripted group (container) (typed FeaturePython)
  n = 0.147
FEATURE [App::DocumentObjectGroupPython] G4_BONE_COMPACT_ICRU  # scripted group (container) (typed FeaturePython)
  Dunit = g/cm3
  Dvalue = 1.85
  Group = -> [H_element015,C_element015,N_element010,O_element014,Mg_element001,P_element002,S_element004,Ca_element003]
  conduct = 2
  density = 1
  expand = 3
  formula = G4_BONE_COMPACT_ICRU
  name = G4_BONE_COMPACT_ICRU
  specific = 4
FEATURE [App::DocumentObjectGroupPython] H_element016  label="H_element : 0.034"  # scripted group (container) (typed FeaturePython)
  n = 0.034
FEATURE [App::DocumentObjectGroupPython] C_element016  label="C_element : 0.155"  # scripted group (container) (typed FeaturePython)
  n = 0.155
FEATURE [App::DocumentObjectGroupPython] N_element011  label="N_element : 0.042"  # scripted group (container) (typed FeaturePython)
  n = 0.042
FEATURE [App::DocumentObjectGroupPython] O_element015  label="O_element : 0.435"  # scripted group (container) (typed FeaturePython)
  n = 0.435
FEATURE [App::DocumentObjectGroupPython] Na_element003  label="Na_element : 0.003"  # scripted group (container) (typed FeaturePython)
  n = 0.001
FEATURE [App::DocumentObjectGroupPython] Mg_element002  label="Mg_element : 0.003"  # scripted group (container) (typed FeaturePython)
  n = 0.002
FEATURE [App::DocumentObjectGroupPython] P_element003  label="P_element : 0.103"  # scripted group (container) (typed FeaturePython)
  n = 0.103
FEATURE [App::DocumentObjectGroupPython] S_element005  label="S_element : 0.004"  # scripted group (container) (typed FeaturePython)
  n = 0.003
FEATURE [App::DocumentObjectGroupPython] Ca_element004  label="Ca_element : 0.225"  # scripted group (container) (typed FeaturePython)
  n = 0.225
FEATURE [App::DocumentObjectGroupPython] G4_BONE_CORTICAL_ICRP  # scripted group (container) (typed FeaturePython)
  Dunit = g/cm3
  Dvalue = 1.92
  Group = -> [H_element016,C_element016,N_element011,O_element015,Na_element003,Mg_element002,P_element003,S_element005,Ca_element004]
  conduct = 2
  density = 1
  expand = 3
  formula = G4_BONE_CORTICAL_ICRP
  name = G4_BONE_CORTICAL_ICRP
  specific = 4
FEATURE [App::DocumentObjectGroupPython] B_element001  label="B_element : 4"  # scripted group (container) (typed FeaturePython)
  n = 4
  ref = B_element
FEATURE [App::DocumentObjectGroupPython] C_element017  label="C_element : 1"  # scripted group (container) (typed FeaturePython)
  n = 1
  ref = C_element
FEATURE [App::DocumentObjectGroupPython] G4_BORON_CARBIDE  # scripted group (container) (typed FeaturePython)
  Dunit = g/cm3
  Dvalue = 2.52
  Group = -> [B_element001,C_element017]
  conduct = 2
  density = 1
  expand = 3
  formula = G4_BORON_CARBIDE
  name = G4_BORON_CARBIDE
  specific = 4
FEATURE [App::DocumentObjectGroupPython] B_element002  label="B_element : 2"  # scripted group (container) (typed FeaturePython)
  n = 2
  ref = B_element
FEATURE [App::DocumentObjectGroupPython] O_element016  label="O_element : 006"  # scripted group (container) (typed FeaturePython)
  n = 3
  ref = O_element
FEATURE [App::DocumentObjectGroupPython] G4_BORON_OXIDE  # scripted group (container) (typed FeaturePython)
  Dunit = g/cm3
  Dvalue = 1.812
  Group = -> [B_element002,O_element016]
  conduct = 2
  density = 1
  expand = 3
  formula = G4_BORON_OXIDE
  name = G4_BORON_OXIDE
  specific = 4
FEATURE [App::DocumentObjectGroupPython] H_element017  label="H_element : 0.107"  # scripted group (container) (typed FeaturePython)
  n = 0.107
FEATURE [App::DocumentObjectGroupPython] C_element018  label="C_element : 0.145"  # scripted group (container) (typed FeaturePython)
  n = 0.145
FEATURE [App::DocumentObjectGroupPython] N_element012  label="N_element : 0.022"  # scripted group (container) (typed FeaturePython)
  n = 0.022
FEATURE [App::DocumentObjectGroupPython] O_element017  label="O_element : 0.712"  # scripted group (container) (typed FeaturePython)
  n = 0.712
FEATURE [App::DocumentObjectGroupPython] Na_element004  label="Na_element : 0.004"  # scripted group (container) (typed FeaturePython)
  n = 0.002
FEATURE [App::DocumentObjectGroupPython] P_element004  label="P_element : 0.004"  # scripted group (container) (typed FeaturePython)
  n = 0.004
FEATURE [App::DocumentObjectGroupPython] S_element006  label="S_element : 0.005"  # scripted group (container) (typed FeaturePython)
  n = 0.002
FEATURE [App::DocumentObjectGroupPython] Cl_element003  label="Cl_element : 0.004"  # scripted group (container) (typed FeaturePython)
  n = 0.003
FEATURE [App::DocumentObjectGroupPython] K_element002  label="K_element : 0.003"  # scripted group (container) (typed FeaturePython)
  n = 0.003
FEATURE [App::DocumentObjectGroupPython] G4_BRAIN_ICRP  # scripted group (container) (typed FeaturePython)
  Dunit = g/cm3
  Dvalue = 1.04
  Group = -> [H_element017,C_element018,N_element012,O_element017,Na_element004,P_element004,S_element006,Cl_element003,K_element002]
  conduct = 2
  density = 1
  expand = 3
  formula = G4_BRAIN_ICRP
  name = G4_BRAIN_ICRP
  specific = 4
FEATURE [App::DocumentObjectGroupPython] C_element019  label="C_element : 4"  # scripted group (container) (typed FeaturePython)
  n = 4
  ref = C_element
FEATURE [App::DocumentObjectGroupPython] H_element018  label="H_element : 010"  # scripted group (container) (typed FeaturePython)
  n = 10
  ref = H_element
FEATURE [App::DocumentObjectGroupPython] G4_BUTANE  # scripted group (container) (typed FeaturePython)
  Dunit = g/cm3
  Dvalue = 0.00249343
  Group = -> [C_element019,H_element018]
  conduct = 2
  density = 1
  expand = 3
  formula = G4_BUTANE
  name = G4_BUTANE
  specific = 4
FEATURE [App::DocumentObjectGroupPython] C_element020  label="C_element : 008"  # scripted group (container) (typed FeaturePython)
  n = 4
  ref = C_element
FEATURE [App::DocumentObjectGroupPython] H_element019  label="H_element : 011"  # scripted group (container) (typed FeaturePython)
  n = 10
  ref = H_element
FEATURE [App::DocumentObjectGroupPython] O_element018  label="O_element : 007"  # scripted group (container) (typed FeaturePython)
  n = 1
  ref = O_element
FEATURE [App::DocumentObjectGroupPython] G4_N_BUTYL_ALCOHOL  label="G4_N-BUTYL_ALCOHOL"  # scripted group (container) (typed FeaturePython)
  Dunit = g/cm3
  Dvalue = 0.8098
  Group = -> [C_element020,H_element019,O_element018]
  conduct = 2
  density = 1
  expand = 3
  formula = G4_N-BUTYL_ALCOHOL
  name = G4_N-BUTYL_ALCOHOL
  specific = 4
FEATURE [App::DocumentObjectGroupPython] H_element020  label="H_element : 0.025"  # scripted group (container) (typed FeaturePython)
  n = 0.02468
FEATURE [App::DocumentObjectGroupPython] C_element021  label="C_element : 0.502"  # scripted group (container) (typed FeaturePython)
  n = 0.501611
FEATURE [App::DocumentObjectGroupPython] O_element019  label="O_element : 0.005"  # scripted group (container) (typed FeaturePython)
  n = 0.004527
FEATURE [App::DocumentObjectGroupPython] F_element004  label="F_element : 0.465"  # scripted group (container) (typed FeaturePython)
  n = 0.465209
FEATURE [App::DocumentObjectGroupPython] Si_element001  label="Si_element : 0.004"  # scripted group (container) (typed FeaturePython)
  n = 0.003973
FEATURE [App::DocumentObjectGroupPython] G4_C_552  label="G4_C-552"  # scripted group (container) (typed FeaturePython)
  Dunit = g/cm3
  Dvalue = 1.76
  Group = -> [H_element020,C_element021,O_element019,F_element004,Si_element001]
  conduct = 2
  density = 1
  expand = 3
  formula = G4_C-552
  name = G4_C-552
  specific = 4
FEATURE [App::DocumentObjectGroupPython] Cd_element001  label="Cd_element : 1"  # scripted group (container) (typed FeaturePython)
  n = 1
  ref = Cd_element
FEATURE [App::DocumentObjectGroupPython] Te_element001  label="Te_element : 1"  # scripted group (container) (typed FeaturePython)
  n = 1
  ref = Te_element
FEATURE [App::DocumentObjectGroupPython] G4_CADMIUM_TELLURIDE  # scripted group (container) (typed FeaturePython)
  Dunit = g/cm3
  Dvalue = 6.2
  Group = -> [Cd_element001,Te_element001]
  conduct = 2
  density = 1
  expand = 3
  formula = G4_CADMIUM_TELLURIDE
  name = G4_CADMIUM_TELLURIDE
  specific = 4
FEATURE [App::DocumentObjectGroupPython] Cd_element002  label="Cd_element : 002"  # scripted group (container) (typed FeaturePython)
  n = 1
  ref = Cd_element
FEATURE [App::DocumentObjectGroupPython] W_element001  label="W_element : 1"  # scripted group (container) (typed FeaturePython)
  n = 1
  ref = W_element
FEATURE [App::DocumentObjectGroupPython] O_element020  label="O_element : 008"  # scripted group (container) (typed FeaturePython)
  n = 4
  ref = O_element
FEATURE [App::DocumentObjectGroupPython] G4_CADMIUM_TUNGSTATE  # scripted group (container) (typed FeaturePython)
  Dunit = g/cm3
  Dvalue = 7.9
  Group = -> [Cd_element002,W_element001,O_element020]
  conduct = 2
  density = 1
  expand = 3
  formula = G4_CADMIUM_TUNGSTATE
  name = G4_CADMIUM_TUNGSTATE
  specific = 4
FEATURE [App::DocumentObjectGroupPython] Ca_element005  label="Ca_element : 1"  # scripted group (container) (typed FeaturePython)
  n = 1
  ref = Ca_element
FEATURE [App::DocumentObjectGroupPython] C_element022  label="C_element : 009"  # scripted group (container) (typed FeaturePython)
  n = 1
  ref = C_element
FEATURE [App::DocumentObjectGroupPython] O_element021  label="O_element : 009"  # scripted group (container) (typed FeaturePython)
  n = 3
  ref = O_element
FEATURE [App::DocumentObjectGroupPython] G4_CALCIUM_CARBONATE  # scripted group (container) (typed FeaturePython)
  Dunit = g/cm3
  Dvalue = 2.8
  Group = -> [Ca_element005,C_element022,O_element021]
  conduct = 2
  density = 1
  expand = 3
  formula = G4_CALCIUM_CARBONATE
  name = G4_CALCIUM_CARBONATE
  specific = 4
FEATURE [App::DocumentObjectGroupPython] Ca_element006  label="Ca_element : 002"  # scripted group (container) (typed FeaturePython)
  n = 1
  ref = Ca_element
FEATURE [App::DocumentObjectGroupPython] F_element005  label="F_element : 003"  # scripted group (container) (typed FeaturePython)
  n = 2
  ref = F_element
FEATURE [App::DocumentObjectGroupPython] G4_CALCIUM_FLUORIDE  # scripted group (container) (typed FeaturePython)
  Dunit = g/cm3
  Dvalue = 3.18
  Group = -> [Ca_element006,F_element005]
  conduct = 2
  density = 1
  expand = 3
  formula = G4_CALCIUM_FLUORIDE
  name = G4_CALCIUM_FLUORIDE
  specific = 4
FEATURE [App::DocumentObjectGroupPython] Ca_element007  label="Ca_element : 003"  # scripted group (container) (typed FeaturePython)
  n = 1
  ref = Ca_element
FEATURE [App::DocumentObjectGroupPython] O_element022  label="O_element : 010"  # scripted group (container) (typed FeaturePython)
  n = 1
  ref = O_element
FEATURE [App::DocumentObjectGroupPython] G4_CALCIUM_OXIDE  # scripted group (container) (typed FeaturePython)
  Dunit = g/cm3
  Dvalue = 3.3
  Group = -> [Ca_element007,O_element022]
  conduct = 2
  density = 1
  expand = 3
  formula = G4_CALCIUM_OXIDE
  name = G4_CALCIUM_OXIDE
  specific = 4
FEATURE [App::DocumentObjectGroupPython] Ca_element008  label="Ca_element : 004"  # scripted group (container) (typed FeaturePython)
  n = 1
  ref = Ca_element
FEATURE [App::DocumentObjectGroupPython] S_element007  label="S_element : 002"  # scripted group (container) (typed FeaturePython)
  n = 1
  ref = S_element
FEATURE [App::DocumentObjectGroupPython] O_element023  label="O_element : 011"  # scripted group (container) (typed FeaturePython)
  n = 4
  ref = O_element
FEATURE [App::DocumentObjectGroupPython] G4_CALCIUM_SULFATE  # scripted group (container) (typed FeaturePython)
  Dunit = g/cm3
  Dvalue = 2.96
  Group = -> [Ca_element008,S_element007,O_element023]
  conduct = 2
  density = 1
  expand = 3
  formula = G4_CALCIUM_SULFATE
  name = G4_CALCIUM_SULFATE
  specific = 4
FEATURE [App::DocumentObjectGroupPython] Ca_element009  label="Ca_element : 005"  # scripted group (container) (typed FeaturePython)
  n = 1
  ref = Ca_element
FEATURE [App::DocumentObjectGroupPython] W_element002  label="W_element : 002"  # scripted group (container) (typed FeaturePython)
  n = 1
  ref = W_element
FEATURE [App::DocumentObjectGroupPython] O_element024  label="O_element : 012"  # scripted group (container) (typed FeaturePython)
  n = 4
  ref = O_element
FEATURE [App::DocumentObjectGroupPython] G4_CALCIUM_TUNGSTATE  # scripted group (container) (typed FeaturePython)
  Dunit = g/cm3
  Dvalue = 6.062
  Group = -> [Ca_element009,W_element002,O_element024]
  conduct = 2
  density = 1
  expand = 3
  formula = G4_CALCIUM_TUNGSTATE
  name = G4_CALCIUM_TUNGSTATE
  specific = 4
FEATURE [App::DocumentObjectGroupPython] C_element023  label="C_element : 010"  # scripted group (container) (typed FeaturePython)
  n = 1
  ref = C_element
FEATURE [App::DocumentObjectGroupPython] O_element025  label="O_element : 013"  # scripted group (container) (typed FeaturePython)
  n = 2
  ref = O_element
FEATURE [App::DocumentObjectGroupPython] G4_CARBON_DIOXIDE  # scripted group (container) (typed FeaturePython)
  Dunit = g/cm3
  Dvalue = 0.00184212
  Group = -> [C_element023,O_element025]
  conduct = 2
  density = 1
  expand = 3
  formula = G4_CARBON_DIOXIDE
  name = G4_CARBON_DIOXIDE
  specific = 4
FEATURE [App::DocumentObjectGroupPython] C_element024  label="C_element : 011"  # scripted group (container) (typed FeaturePython)
  n = 1
  ref = C_element
FEATURE [App::DocumentObjectGroupPython] Cl_element004  label="Cl_element : 4"  # scripted group (container) (typed FeaturePython)
  n = 4
  ref = Cl_element
FEATURE [App::DocumentObjectGroupPython] G4_CARBON_TETRACHLORIDE  # scripted group (container) (typed FeaturePython)
  Dunit = g/cm3
  Dvalue = 1.594
  Group = -> [C_element024,Cl_element004]
  conduct = 2
  density = 1
  expand = 3
  formula = G4_CARBON_TETRACHLORIDE
  name = G4_CARBON_TETRACHLORIDE
  specific = 4
FEATURE [App::DocumentObjectGroupPython] C_element025  label="C_element : 012"  # scripted group (container) (typed FeaturePython)
  n = 6
  ref = C_element
FEATURE [App::DocumentObjectGroupPython] H_element021  label="H_element : 012"  # scripted group (container) (typed FeaturePython)
  n = 10
  ref = H_element
FEATURE [App::DocumentObjectGroupPython] O_element026  label="O_element : 5"  # scripted group (container) (typed FeaturePython)
  n = 5
  ref = O_element
FEATURE [App::DocumentObjectGroupPython] G4_CELLULOSE_CELLOPHANE  # scripted group (container) (typed FeaturePython)
  Dunit = g/cm3
  Dvalue = 1.42
  Group = -> [C_element025,H_element021,O_element026]
  conduct = 2
  density = 1
  expand = 3
  formula = G4_CELLULOSE_CELLOPHANE
  name = G4_CELLULOSE_CELLOPHANE
  specific = 4
FEATURE [App::DocumentObjectGroupPython] H_element022  label="H_element : 0.067"  # scripted group (container) (typed FeaturePython)
  n = 0.067125
FEATURE [App::DocumentObjectGroupPython] C_element026  label="C_element : 0.545"  # scripted group (container) (typed FeaturePython)
  n = 0.545403
FEATURE [App::DocumentObjectGroupPython] O_element027  label="O_element : 0.387"  # scripted group (container) (typed FeaturePython)
  n = 0.387472
FEATURE [App::DocumentObjectGroupPython] G4_CELLULOSE_BUTYRATE  # scripted group (container) (typed FeaturePython)
  Dunit = g/cm3
  Dvalue = 1.2
  Group = -> [H_element022,C_element026,O_element027]
  conduct = 2
  density = 1
  expand = 3
  formula = G4_CELLULOSE_BUTYRATE
  name = G4_CELLULOSE_BUTYRATE
  specific = 4
FEATURE [App::DocumentObjectGroupPython] H_element023  label="H_element : 0.029"  # scripted group (container) (typed FeaturePython)
  n = 0.029216
FEATURE [App::DocumentObjectGroupPython] C_element027  label="C_element : 0.271"  # scripted group (container) (typed FeaturePython)
  n = 0.271296
FEATURE [App::DocumentObjectGroupPython] N_element013  label="N_element : 0.121"  # scripted group (container) (typed FeaturePython)
  n = 0.121276
FEATURE [App::DocumentObjectGroupPython] O_element028  label="O_element : 0.578"  # scripted group (container) (typed FeaturePython)
  n = 0.578212
FEATURE [App::DocumentObjectGroupPython] G4_CELLULOSE_NITRATE  # scripted group (container) (typed FeaturePython)
  Dunit = g/cm3
  Dvalue = 1.49
  Group = -> [H_element023,C_element027,N_element013,O_element028]
  conduct = 2
  density = 1
  expand = 3
  formula = G4_CELLULOSE_NITRATE
  name = G4_CELLULOSE_NITRATE
  specific = 4
FEATURE [App::DocumentObjectGroupPython] H_element024  label="H_element : 0.108"  # scripted group (container) (typed FeaturePython)
  n = 0.107596
FEATURE [App::DocumentObjectGroupPython] N_element014  label="N_element : 0.001"  # scripted group (container) (typed FeaturePython)
  n = 0.0008
FEATURE [App::DocumentObjectGroupPython] O_element029  label="O_element : 0.875"  # scripted group (container) (typed FeaturePython)
  n = 0.874976
FEATURE [App::DocumentObjectGroupPython] S_element008  label="S_element : 0.015"  # scripted group (container) (typed FeaturePython)
  n = 0.014627
FEATURE [App::DocumentObjectGroupPython] Ce_element001  label="Ce_element : 0.002"  # scripted group (container) (typed FeaturePython)
  n = 0.002001
FEATURE [App::DocumentObjectGroupPython] G4_CERIC_SULFATE  # scripted group (container) (typed FeaturePython)
  Dunit = g/cm3
  Dvalue = 1.03
  Group = -> [H_element024,N_element014,O_element029,S_element008,Ce_element001]
  conduct = 2
  density = 1
  expand = 3
  formula = G4_CERIC_SULFATE
  name = G4_CERIC_SULFATE
  specific = 4
FEATURE [App::DocumentObjectGroupPython] Cs_element001  label="Cs_element : 1"  # scripted group (container) (typed FeaturePython)
  n = 1
  ref = Cs_element
FEATURE [App::DocumentObjectGroupPython] F_element006  label="F_element : 1"  # scripted group (container) (typed FeaturePython)
  n = 1
  ref = F_element
FEATURE [App::DocumentObjectGroupPython] G4_CESIUM_FLUORIDE  # scripted group (container) (typed FeaturePython)
  Dunit = g/cm3
  Dvalue = 4.115
  Group = -> [Cs_element001,F_element006]
  conduct = 2
  density = 1
  expand = 3
  formula = G4_CESIUM_FLUORIDE
  name = G4_CESIUM_FLUORIDE
  specific = 4
FEATURE [App::DocumentObjectGroupPython] Cs_element002  label="Cs_element : 002"  # scripted group (container) (typed FeaturePython)
  n = 1
  ref = Cs_element
FEATURE [App::DocumentObjectGroupPython] I_element001  label="I_element : 1"  # scripted group (container) (typed FeaturePython)
  n = 1
  ref = I_element
FEATURE [App::DocumentObjectGroupPython] G4_CESIUM_IODIDE  # scripted group (container) (typed FeaturePython)
  Dunit = g/cm3
  Dvalue = 4.51
  Group = -> [Cs_element002,I_element001]
  conduct = 2
  density = 1
  expand = 3
  formula = G4_CESIUM_IODIDE
  name = G4_CESIUM_IODIDE
  specific = 4
FEATURE [App::DocumentObjectGroupPython] C_element028  label="C_element : 013"  # scripted group (container) (typed FeaturePython)
  n = 6
  ref = C_element
FEATURE [App::DocumentObjectGroupPython] H_element025  label="H_element : 013"  # scripted group (container) (typed FeaturePython)
  n = 5
  ref = H_element
FEATURE [App::DocumentObjectGroupPython] Cl_element005  label="Cl_element : 1"  # scripted group (container) (typed FeaturePython)
  n = 1
  ref = Cl_element
FEATURE [App::DocumentObjectGroupPython] G4_CHLOROBENZENE  # scripted group (container) (typed FeaturePython)
  Dunit = g/cm3
  Dvalue = 1.1058
  Group = -> [C_element028,H_element025,Cl_element005]
  conduct = 2
  density = 1
  expand = 3
  formula = G4_CHLOROBENZENE
  name = G4_CHLOROBENZENE
  specific = 4
FEATURE [App::DocumentObjectGroupPython] C_element029  label="C_element : 014"  # scripted group (container) (typed FeaturePython)
  n = 1
  ref = C_element
FEATURE [App::DocumentObjectGroupPython] H_element026  label="H_element : 1"  # scripted group (container) (typed FeaturePython)
  n = 1
  ref = H_element
FEATURE [App::DocumentObjectGroupPython] Cl_element006  label="Cl_element : 3"  # scripted group (container) (typed FeaturePython)
  n = 3
  ref = Cl_element
FEATURE [App::DocumentObjectGroupPython] G4_CHLOROFORM  # scripted group (container) (typed FeaturePython)
  Dunit = g/cm3
  Dvalue = 1.4832
  Group = -> [C_element029,H_element026,Cl_element006]
  conduct = 2
  density = 1
  expand = 3
  formula = G4_CHLOROFORM
  name = G4_CHLOROFORM
  specific = 4
FEATURE [App::DocumentObjectGroupPython] H_element027  label="H_element : 0.010"  # scripted group (container) (typed FeaturePython)
  n = 0.01
FEATURE [App::DocumentObjectGroupPython] C_element030  label="C_element : 0.001"  # scripted group (container) (typed FeaturePython)
  n = 0.001
FEATURE [App::DocumentObjectGroupPython] O_element030  label="O_element : 0.529"  # scripted group (container) (typed FeaturePython)
  n = 0.529107
FEATURE [App::DocumentObjectGroupPython] Na_element005  label="Na_element : 0.016"  # scripted group (container) (typed FeaturePython)
  n = 0.016
FEATURE [App::DocumentObjectGroupPython] Mg_element003  label="Mg_element : 0.004"  # scripted group (container) (typed FeaturePython)
  n = 0.002
FEATURE [App::DocumentObjectGroupPython] Al_element002  label="Al_element : 0.034"  # scripted group (container) (typed FeaturePython)
  n = 0.033872
FEATURE [App::DocumentObjectGroupPython] Si_element002  label="Si_element : 0.337"  # scripted group (container) (typed FeaturePython)
  n = 0.337021
FEATURE [App::DocumentObjectGroupPython] K_element003  label="K_element : 0.013"  # scripted group (container) (typed FeaturePython)
  n = 0.013
FEATURE [App::DocumentObjectGroupPython] Ca_element010  label="Ca_element : 0.044"  # scripted group (container) (typed FeaturePython)
  n = 0.044
FEATURE [App::DocumentObjectGroupPython] Fe_element002  label="Fe_element : 0.014"  # scripted group (container) (typed FeaturePython)
  n = 0.014
FEATURE [App::DocumentObjectGroupPython] G4_CONCRETE  # scripted group (container) (typed FeaturePython)
  Dunit = g/cm3
  Dvalue = 2.3
  Group = -> [H_element027,C_element030,O_element030,Na_element005,Mg_element003,Al_element002,Si_element002,K_element003,Ca_element010,Fe_element002]
  conduct = 2
  density = 1
  expand = 3
  formula = G4_CONCRETE
  name = G4_CONCRETE
  specific = 4
FEATURE [App::DocumentObjectGroupPython] C_element031  label="C_element : 015"  # scripted group (container) (typed FeaturePython)
  n = 6
  ref = C_element
FEATURE [App::DocumentObjectGroupPython] H_element028  label="H_element : 12"  # scripted group (container) (typed FeaturePython)
  n = 12
  ref = H_element
FEATURE [App::DocumentObjectGroupPython] G4_CYCLOHEXANE  # scripted group (container) (typed FeaturePython)
  Dunit = g/cm3
  Dvalue = 0.779
  Group = -> [C_element031,H_element028]
  conduct = 2
  density = 1
  expand = 3
  formula = G4_CYCLOHEXANE
  name = G4_CYCLOHEXANE
  specific = 4
FEATURE [App::DocumentObjectGroupPython] C_element032  label="C_element : 016"  # scripted group (container) (typed FeaturePython)
  n = 6
  ref = C_element
FEATURE [App::DocumentObjectGroupPython] H_element029  label="H_element : 4"  # scripted group (container) (typed FeaturePython)
  n = 4
  ref = H_element
FEATURE [App::DocumentObjectGroupPython] Cl_element007  label="Cl_element : 2"  # scripted group (container) (typed FeaturePython)
  n = 2
  ref = Cl_element
FEATURE [App::DocumentObjectGroupPython] G4_1_2_DICHLOROBENZENE  label="G4_1.2-DICHLOROBENZENE"  # scripted group (container) (typed FeaturePython)
  Dunit = g/cm3
  Dvalue = 1.3048
  Group = -> [C_element032,H_element029,Cl_element007]
  conduct = 2
  density = 1
  expand = 3
  formula = G4_1.2-DICHLOROBENZENE
  name = G4_1.2-DICHLOROBENZENE
  specific = 4
FEATURE [App::DocumentObjectGroupPython] C_element033  label="C_element : 017"  # scripted group (container) (typed FeaturePython)
  n = 4
  ref = C_element
FEATURE [App::DocumentObjectGroupPython] H_element030  label="H_element : 8"  # scripted group (container) (typed FeaturePython)
  n = 8
  ref = H_element
FEATURE [App::DocumentObjectGroupPython] O_element031  label="O_element : 014"  # scripted group (container) (typed FeaturePython)
  n = 1
  ref = O_element
FEATURE [App::DocumentObjectGroupPython] Cl_element008  label="Cl_element : 005"  # scripted group (container) (typed FeaturePython)
  n = 2
  ref = Cl_element
FEATURE [App::DocumentObjectGroupPython] G4_DICHLORODIETHYL_ETHER  # scripted group (container) (typed FeaturePython)
  Dunit = g/cm3
  Dvalue = 1.2199
  Group = -> [C_element033,H_element030,O_element031,Cl_element008]
  conduct = 2
  density = 1
  expand = 3
  formula = G4_DICHLORODIETHYL_ETHER
  name = G4_DICHLORODIETHYL_ETHER
  specific = 4
FEATURE [App::DocumentObjectGroupPython] C_element034  label="C_element : 018"  # scripted group (container) (typed FeaturePython)
  n = 2
  ref = C_element
FEATURE [App::DocumentObjectGroupPython] H_element031  label="H_element : 014"  # scripted group (container) (typed FeaturePython)
  n = 4
  ref = H_element
FEATURE [App::DocumentObjectGroupPython] Cl_element009  label="Cl_element : 006"  # scripted group (container) (typed FeaturePython)
  n = 2
  ref = Cl_element
FEATURE [App::DocumentObjectGroupPython] G4_1_2_DICHLOROETHANE  label="G4_1.2-DICHLOROETHANE"  # scripted group (container) (typed FeaturePython)
  Dunit = g/cm3
  Dvalue = 1.2351
  Group = -> [C_element034,H_element031,Cl_element009]
  conduct = 2
  density = 1
  expand = 3
  formula = G4_1.2-DICHLOROETHANE
  name = G4_1.2-DICHLOROETHANE
  specific = 4
FEATURE [App::DocumentObjectGroupPython] C_element035  label="C_element : 019"  # scripted group (container) (typed FeaturePython)
  n = 4
  ref = C_element
FEATURE [App::DocumentObjectGroupPython] H_element032  label="H_element : 015"  # scripted group (container) (typed FeaturePython)
  n = 10
  ref = H_element
FEATURE [App::DocumentObjectGroupPython] O_element032  label="O_element : 015"  # scripted group (container) (typed FeaturePython)
  n = 1
  ref = O_element
FEATURE [App::DocumentObjectGroupPython] G4_DIETHYL_ETHER  # scripted group (container) (typed FeaturePython)
  Dunit = g/cm3
  Dvalue = 0.71378
  Group = -> [C_element035,H_element032,O_element032]
  conduct = 2
  density = 1
  expand = 3
  formula = G4_DIETHYL_ETHER
  name = G4_DIETHYL_ETHER
  specific = 4
FEATURE [App::DocumentObjectGroupPython] C_element036  label="C_element : 020"  # scripted group (container) (typed FeaturePython)
  n = 3
  ref = C_element
FEATURE [App::DocumentObjectGroupPython] H_element033  label="H_element : 016"  # scripted group (container) (typed FeaturePython)
  n = 7
  ref = H_element
FEATURE [App::DocumentObjectGroupPython] N_element015  label="N_element : 008"  # scripted group (container) (typed FeaturePython)
  n = 1
  ref = N_element
FEATURE [App::DocumentObjectGroupPython] O_element033  label="O_element : 016"  # scripted group (container) (typed FeaturePython)
  n = 1
  ref = O_element
FEATURE [App::DocumentObjectGroupPython] G4_N_N_DIMETHYL_FORMAMIDE  label="G4_N.N-DIMETHYL_FORMAMIDE"  # scripted group (container) (typed FeaturePython)
  Dunit = g/cm3
  Dvalue = 0.9487
  Group = -> [C_element036,H_element033,N_element015,O_element033]
  conduct = 2
  density = 1
  expand = 3
  formula = G4_N.N-DIMETHYL_FORMAMIDE
  name = G4_N.N-DIMETHYL_FORMAMIDE
  specific = 4
FEATURE [App::DocumentObjectGroupPython] C_element037  label="C_element : 021"  # scripted group (container) (typed FeaturePython)
  n = 2
  ref = C_element
FEATURE [App::DocumentObjectGroupPython] H_element034  label="H_element : 017"  # scripted group (container) (typed FeaturePython)
  n = 6
  ref = H_element
FEATURE [App::DocumentObjectGroupPython] O_element034  label="O_element : 017"  # scripted group (container) (typed FeaturePython)
  n = 1
  ref = O_element
FEATURE [App::DocumentObjectGroupPython] S_element009  label="S_element : 003"  # scripted group (container) (typed FeaturePython)
  n = 1
  ref = S_element
FEATURE [App::DocumentObjectGroupPython] G4_DIMETHYL_SULFOXIDE  # scripted group (container) (typed FeaturePython)
  Dunit = g/cm3
  Dvalue = 1.1014
  Group = -> [C_element037,H_element034,O_element034,S_element009]
  conduct = 2
  density = 1
  expand = 3
  formula = G4_DIMETHYL_SULFOXIDE
  name = G4_DIMETHYL_SULFOXIDE
  specific = 4
FEATURE [App::DocumentObjectGroupPython] C_element038  label="C_element : 022"  # scripted group (container) (typed FeaturePython)
  n = 2
  ref = C_element
FEATURE [App::DocumentObjectGroupPython] H_element035  label="H_element : 018"  # scripted group (container) (typed FeaturePython)
  n = 6
  ref = H_element
FEATURE [App::DocumentObjectGroupPython] G4_ETHANE  # scripted group (container) (typed FeaturePython)
  Dunit = g/cm3
  Dvalue = 0.00125324
  Group = -> [C_element038,H_element035]
  conduct = 2
  density = 1
  expand = 3
  formula = G4_ETHANE
  name = G4_ETHANE
  specific = 4
FEATURE [App::DocumentObjectGroupPython] C_element039  label="C_element : 023"  # scripted group (container) (typed FeaturePython)
  n = 2
  ref = C_element
FEATURE [App::DocumentObjectGroupPython] H_element036  label="H_element : 019"  # scripted group (container) (typed FeaturePython)
  n = 6
  ref = H_element
FEATURE [App::DocumentObjectGroupPython] O_element035  label="O_element : 018"  # scripted group (container) (typed FeaturePython)
  n = 1
  ref = O_element
FEATURE [App::DocumentObjectGroupPython] G4_ETHYL_ALCOHOL  # scripted group (container) (typed FeaturePython)
  Dunit = g/cm3
  Dvalue = 0.7893
  Group = -> [C_element039,H_element036,O_element035]
  conduct = 2
  density = 1
  expand = 3
  formula = G4_ETHYL_ALCOHOL
  name = G4_ETHYL_ALCOHOL
  specific = 4
FEATURE [App::DocumentObjectGroupPython] H_element037  label="H_element : 0.090"  # scripted group (container) (typed FeaturePython)
  n = 0.090027
FEATURE [App::DocumentObjectGroupPython] C_element040  label="C_element : 0.585"  # scripted group (container) (typed FeaturePython)
  n = 0.585182
FEATURE [App::DocumentObjectGroupPython] O_element036  label="O_element : 0.325"  # scripted group (container) (typed FeaturePython)
  n = 0.324791
FEATURE [App::DocumentObjectGroupPython] G4_ETHYL_CELLULOSE  # scripted group (container) (typed FeaturePython)
  Dunit = g/cm3
  Dvalue = 1.13
  Group = -> [H_element037,C_element040,O_element036]
  conduct = 2
  density = 1
  expand = 3
  formula = G4_ETHYL_CELLULOSE
  name = G4_ETHYL_CELLULOSE
  specific = 4
FEATURE [App::DocumentObjectGroupPython] C_element041  label="C_element : 024"  # scripted group (container) (typed FeaturePython)
  n = 2
  ref = C_element
FEATURE [App::DocumentObjectGroupPython] H_element038  label="H_element : 020"  # scripted group (container) (typed FeaturePython)
  n = 4
  ref = H_element
FEATURE [App::DocumentObjectGroupPython] G4_ETHYLENE  # scripted group (container) (typed FeaturePython)
  Dunit = g/cm3
  Dvalue = 0.00117497
  Group = -> [C_element041,H_element038]
  conduct = 2
  density = 1
  expand = 3
  formula = G4_ETHYLENE
  name = G4_ETHYLENE
  specific = 4
FEATURE [App::DocumentObjectGroupPython] H_element039  label="H_element : 0.096"  # scripted group (container) (typed FeaturePython)
  n = 0.096
FEATURE [App::DocumentObjectGroupPython] C_element042  label="C_element : 0.195"  # scripted group (container) (typed FeaturePython)
  n = 0.195
FEATURE [App::DocumentObjectGroupPython] N_element016  label="N_element : 0.057"  # scripted group (container) (typed FeaturePython)
  n = 0.057
FEATURE [App::DocumentObjectGroupPython] O_element037  label="O_element : 0.646"  # scripted group (container) (typed FeaturePython)
  n = 0.646
FEATURE [App::DocumentObjectGroupPython] Na_element006  label="Na_element : 0.017"  # scripted group (container) (typed FeaturePython)
  n = 0.001
FEATURE [App::DocumentObjectGroupPython] P_element005  label="P_element : 0.104"  # scripted group (container) (typed FeaturePython)
  n = 0.001
FEATURE [App::DocumentObjectGroupPython] S_element010  label="S_element : 0.016"  # scripted group (container) (typed FeaturePython)
  n = 0.003
FEATURE [App::DocumentObjectGroupPython] Cl_element010  label="Cl_element : 0.005"  # scripted group (container) (typed FeaturePython)
  n = 0.001
FEATURE [App::DocumentObjectGroupPython] G4_EYE_LENS_ICRP  # scripted group (container) (typed FeaturePython)
  Dunit = g/cm3
  Dvalue = 1.07
  Group = -> [H_element039,C_element042,N_element016,O_element037,Na_element006,P_element005,S_element010,Cl_element010]
  conduct = 2
  density = 1
  expand = 3
  formula = G4_EYE_LENS_ICRP
  name = G4_EYE_LENS_ICRP
  specific = 4
FEATURE [App::DocumentObjectGroupPython] Fe_element003  label="Fe_element : 2"  # scripted group (container) (typed FeaturePython)
  n = 2
  ref = Fe_element
FEATURE [App::DocumentObjectGroupPython] O_element038  label="O_element : 019"  # scripted group (container) (typed FeaturePython)
  n = 3
  ref = O_element
FEATURE [App::DocumentObjectGroupPython] G4_FERRIC_OXIDE  # scripted group (container) (typed FeaturePython)
  Dunit = g/cm3
  Dvalue = 5.2
  Group = -> [Fe_element003,O_element038]
  conduct = 2
  density = 1
  expand = 3
  formula = G4_FERRIC_OXIDE
  name = G4_FERRIC_OXIDE
  specific = 4
FEATURE [App::DocumentObjectGroupPython] Fe_element004  label="Fe_element : 1"  # scripted group (container) (typed FeaturePython)
  n = 1
  ref = Fe_element
FEATURE [App::DocumentObjectGroupPython] B_element003  label="B_element : 1"  # scripted group (container) (typed FeaturePython)
  n = 1
  ref = B_element
FEATURE [App::DocumentObjectGroupPython] G4_FERROBORIDE  # scripted group (container) (typed FeaturePython)
  Dunit = g/cm3
  Dvalue = 7.15
  Group = -> [Fe_element004,B_element003]
  conduct = 2
  density = 1
  expand = 3
  formula = G4_FERROBORIDE
  name = G4_FERROBORIDE
  specific = 4
FEATURE [App::DocumentObjectGroupPython] Fe_element005  label="Fe_element : 003"  # scripted group (container) (typed FeaturePython)
  n = 1
  ref = Fe_element
FEATURE [App::DocumentObjectGroupPython] O_element039  label="O_element : 020"  # scripted group (container) (typed FeaturePython)
  n = 1
  ref = O_element
FEATURE [App::DocumentObjectGroupPython] G4_FERROUS_OXIDE  # scripted group (container) (typed FeaturePython)
  Dunit = g/cm3
  Dvalue = 5.7
  Group = -> [Fe_element005,O_element039]
  conduct = 2
  density = 1
  expand = 3
  formula = G4_FERROUS_OXIDE
  name = G4_FERROUS_OXIDE
  specific = 4
FEATURE [App::DocumentObjectGroupPython] H_element040  label="H_element : 0.115"  # scripted group (container) (typed FeaturePython)
  n = 0.108259
FEATURE [App::DocumentObjectGroupPython] N_element017  label="N_element : 0.000"  # scripted group (container) (typed FeaturePython)
  n = 2.7e-05
FEATURE [App::DocumentObjectGroupPython] O_element040  label="O_element : 0.879"  # scripted group (container) (typed FeaturePython)
  n = 0.878636
FEATURE [App::DocumentObjectGroupPython] Na_element007  label="Na_element : 0.000"  # scripted group (container) (typed FeaturePython)
  n = 2.2e-05
FEATURE [App::DocumentObjectGroupPython] S_element011  label="S_element : 0.013"  # scripted group (container) (typed FeaturePython)
  n = 0.012968
FEATURE [App::DocumentObjectGroupPython] Cl_element011  label="Cl_element : 0.000"  # scripted group (container) (typed FeaturePython)
  n = 3.4e-05
FEATURE [App::DocumentObjectGroupPython] Fe_element006  label="Fe_element : 0.000"  # scripted group (container) (typed FeaturePython)
  n = 5.4e-05
FEATURE [App::DocumentObjectGroupPython] G4_FERROUS_SULFATE  # scripted group (container) (typed FeaturePython)
  Dunit = g/cm3
  Dvalue = 1.024
  Group = -> [H_element040,N_element017,O_element040,Na_element007,S_element011,Cl_element011,Fe_element006]
  conduct = 2
  density = 1
  expand = 3
  formula = G4_FERROUS_SULFATE
  name = G4_FERROUS_SULFATE
  specific = 4
FEATURE [App::DocumentObjectGroupPython] C_element043  label="C_element : 0.099"  # scripted group (container) (typed FeaturePython)
  n = 0.099335
FEATURE [App::DocumentObjectGroupPython] F_element007  label="F_element : 0.314"  # scripted group (container) (typed FeaturePython)
  n = 0.314247
FEATURE [App::DocumentObjectGroupPython] Cl_element012  label="Cl_element : 0.586"  # scripted group (container) (typed FeaturePython)
  n = 0.586418
FEATURE [App::DocumentObjectGroupPython] G4_FREON_12  label="G4_FREON-12"  # scripted group (container) (typed FeaturePython)
  Dunit = g/cm3
  Dvalue = 1.12
  Group = -> [C_element043,F_element007,Cl_element012]
  conduct = 2
  density = 1
  expand = 3
  formula = G4_FREON-12
  name = G4_FREON-12
  specific = 4
FEATURE [App::DocumentObjectGroupPython] C_element044  label="C_element : 0.057"  # scripted group (container) (typed FeaturePython)
  n = 0.057245
FEATURE [App::DocumentObjectGroupPython] F_element008  label="F_element : 0.181"  # scripted group (container) (typed FeaturePython)
  n = 0.181096
FEATURE [App::DocumentObjectGroupPython] Br_element001  label="Br_element : 0.762"  # scripted group (container) (typed FeaturePython)
  n = 0.761659
FEATURE [App::DocumentObjectGroupPython] G4_FREON_12B2  label="G4_FREON-12B2"  # scripted group (container) (typed FeaturePython)
  Dunit = g/cm3
  Dvalue = 1.8
  Group = -> [C_element044,F_element008,Br_element001]
  conduct = 2
  density = 1
  expand = 3
  formula = G4_FREON-12B2
  name = G4_FREON-12B2
  specific = 4
FEATURE [App::DocumentObjectGroupPython] C_element045  label="C_element : 0.115"  # scripted group (container) (typed FeaturePython)
  n = 0.114983
FEATURE [App::DocumentObjectGroupPython] F_element009  label="F_element : 0.546"  # scripted group (container) (typed FeaturePython)
  n = 0.545621
FEATURE [App::DocumentObjectGroupPython] Cl_element013  label="Cl_element : 0.339"  # scripted group (container) (typed FeaturePython)
  n = 0.339396
FEATURE [App::DocumentObjectGroupPython] G4_FREON_13  label="G4_FREON-13"  # scripted group (container) (typed FeaturePython)
  Dunit = g/cm3
  Dvalue = 0.95
  Group = -> [C_element045,F_element009,Cl_element013]
  conduct = 2
  density = 1
  expand = 3
  formula = G4_FREON-13
  name = G4_FREON-13
  specific = 4
FEATURE [App::DocumentObjectGroupPython] C_element046  label="C_element : 025"  # scripted group (container) (typed FeaturePython)
  n = 1
  ref = C_element
FEATURE [App::DocumentObjectGroupPython] F_element010  label="F_element : 3"  # scripted group (container) (typed FeaturePython)
  n = 3
  ref = F_element
FEATURE [App::DocumentObjectGroupPython] Br_element002  label="Br_element : 1"  # scripted group (container) (typed FeaturePython)
  n = 1
  ref = Br_element
FEATURE [App::DocumentObjectGroupPython] G4_FREON_13B1  label="G4_FREON-13B1"  # scripted group (container) (typed FeaturePython)
  Dunit = g/cm3
  Dvalue = 1.5
  Group = -> [C_element046,F_element010,Br_element002]
  conduct = 2
  density = 1
  expand = 3
  formula = G4_FREON-13B1
  name = G4_FREON-13B1
  specific = 4
FEATURE [App::DocumentObjectGroupPython] C_element047  label="C_element : 0.061"  # scripted group (container) (typed FeaturePython)
  n = 0.061309
FEATURE [App::DocumentObjectGroupPython] F_element011  label="F_element : 0.291"  # scripted group (container) (typed FeaturePython)
  n = 0.290924
FEATURE [App::DocumentObjectGroupPython] I_element002  label="I_element : 0.648"  # scripted group (container) (typed FeaturePython)
  n = 0.647767
FEATURE [App::DocumentObjectGroupPython] G4_FREON_13I1  label="G4_FREON-13I1"  # scripted group (container) (typed FeaturePython)
  Dunit = g/cm3
  Dvalue = 1.8
  Group = -> [C_element047,F_element011,I_element002]
  conduct = 2
  density = 1
  expand = 3
  formula = G4_FREON-13I1
  name = G4_FREON-13I1
  specific = 4
FEATURE [App::DocumentObjectGroupPython] Gd_element001  label="Gd_element : 2"  # scripted group (container) (typed FeaturePython)
  n = 2
  ref = Gd_element
FEATURE [App::DocumentObjectGroupPython] O_element041  label="O_element : 021"  # scripted group (container) (typed FeaturePython)
  n = 2
  ref = O_element
FEATURE [App::DocumentObjectGroupPython] S_element012  label="S_element : 004"  # scripted group (container) (typed FeaturePython)
  n = 1
  ref = S_element
FEATURE [App::DocumentObjectGroupPython] G4_GADOLINIUM_OXYSULFIDE  # scripted group (container) (typed FeaturePython)
  Dunit = g/cm3
  Dvalue = 7.44
  Group = -> [Gd_element001,O_element041,S_element012]
  conduct = 2
  density = 1
  expand = 3
  formula = G4_GADOLINIUM_OXYSULFIDE
  name = G4_GADOLINIUM_OXYSULFIDE
  specific = 4
FEATURE [App::DocumentObjectGroupPython] Ga_element001  label="Ga_element : 1"  # scripted group (container) (typed FeaturePython)
  n = 1
  ref = Ga_element
FEATURE [App::DocumentObjectGroupPython] As_element001  label="As_element : 1"  # scripted group (container) (typed FeaturePython)
  n = 1
  ref = As_element
FEATURE [App::DocumentObjectGroupPython] G4_GALLIUM_ARSENIDE  # scripted group (container) (typed FeaturePython)
  Dunit = g/cm3
  Dvalue = 5.31
  Group = -> [Ga_element001,As_element001]
  conduct = 2
  density = 1
  expand = 3
  formula = G4_GALLIUM_ARSENIDE
  name = G4_GALLIUM_ARSENIDE
  specific = 4
FEATURE [App::DocumentObjectGroupPython] H_element041  label="H_element : 0.081"  # scripted group (container) (typed FeaturePython)
  n = 0.08118
FEATURE [App::DocumentObjectGroupPython] C_element048  label="C_element : 0.416"  # scripted group (container) (typed FeaturePython)
  n = 0.41606
FEATURE [App::DocumentObjectGroupPython] N_element018  label="N_element : 0.111"  # scripted group (container) (typed FeaturePython)
  n = 0.11124
FEATURE [App::DocumentObjectGroupPython] O_element042  label="O_element : 0.381"  # scripted group (container) (typed FeaturePython)
  n = 0.38064
FEATURE [App::DocumentObjectGroupPython] S_element013  label="S_element : 0.011"  # scripted group (container) (typed FeaturePython)
  n = 0.01088
FEATURE [App::DocumentObjectGroupPython] G4_GEL_PHOTO_EMULSION  # scripted group (container) (typed FeaturePython)
  Dunit = g/cm3
  Dvalue = 1.2914
  Group = -> [H_element041,C_element048,N_element018,O_element042,S_element013]
  conduct = 2
  density = 1
  expand = 3
  formula = G4_GEL_PHOTO_EMULSION
  name = G4_GEL_PHOTO_EMULSION
  specific = 4
FEATURE [App::DocumentObjectGroupPython] B_element004  label="B_element : 0.040"  # scripted group (container) (typed FeaturePython)
  n = 0.0400639
FEATURE [App::DocumentObjectGroupPython] O_element043  label="O_element : 0.540"  # scripted group (container) (typed FeaturePython)
  n = 0.539561
FEATURE [App::DocumentObjectGroupPython] Na_element008  label="Na_element : 0.028"  # scripted group (container) (typed FeaturePython)
  n = 0.0281909
FEATURE [App::DocumentObjectGroupPython] Al_element003  label="Al_element : 0.012"  # scripted group (container) (typed FeaturePython)
  n = 0.011644
FEATURE [App::DocumentObjectGroupPython] Si_element003  label="Si_element : 0.377"  # scripted group (container) (typed FeaturePython)
  n = 0.377219
FEATURE [App::DocumentObjectGroupPython] K_element004  label="K_element : 0.014"  # scripted group (container) (typed FeaturePython)
  n = 0.00332099
FEATURE [App::DocumentObjectGroupPython] G4_Pyrex_Glass  # scripted group (container) (typed FeaturePython)
  Dunit = g/cm3
  Dvalue = 2.23
  Group = -> [B_element004,O_element043,Na_element008,Al_element003,Si_element003,K_element004]
  conduct = 2
  density = 1
  expand = 3
  formula = G4_Pyrex_Glass
  name = G4_Pyrex_Glass
  specific = 4
FEATURE [App::DocumentObjectGroupPython] O_element044  label="O_element : 0.156"  # scripted group (container) (typed FeaturePython)
  n = 0.156453
FEATURE [App::DocumentObjectGroupPython] Si_element004  label="Si_element : 0.081"  # scripted group (container) (typed FeaturePython)
  n = 0.080866
FEATURE [App::DocumentObjectGroupPython] Ti_element001  label="Ti_element : 0.008"  # scripted group (container) (typed FeaturePython)
  n = 0.008092
FEATURE [App::DocumentObjectGroupPython] As_element002  label="As_element : 0.003"  # scripted group (container) (typed FeaturePython)
  n = 0.002651
FEATURE [App::DocumentObjectGroupPython] Pb_element001  label="Pb_element : 0.752"  # scripted group (container) (typed FeaturePython)
  n = 0.751938
FEATURE [App::DocumentObjectGroupPython] G4_GLASS_LEAD  # scripted group (container) (typed FeaturePython)
  Dunit = g/cm3
  Dvalue = 6.22
  Group = -> [O_element044,Si_element004,Ti_element001,As_element002,Pb_element001]
  conduct = 2
  density = 1
  expand = 3
  formula = G4_GLASS_LEAD
  name = G4_GLASS_LEAD
  specific = 4
FEATURE [App::DocumentObjectGroupPython] O_element045  label="O_element : 0.460"  # scripted group (container) (typed FeaturePython)
  n = 0.4598
FEATURE [App::DocumentObjectGroupPython] Na_element009  label="Na_element : 0.096"  # scripted group (container) (typed FeaturePython)
  n = 0.0964411
FEATURE [App::DocumentObjectGroupPython] Si_element005  label="Si_element : 0.378"  # scripted group (container) (typed FeaturePython)
  n = 0.336553
FEATURE [App::DocumentObjectGroupPython] Ca_element011  label="Ca_element : 0.107"  # scripted group (container) (typed FeaturePython)
  n = 0.107205
FEATURE [App::DocumentObjectGroupPython] G4_GLASS_PLATE  # scripted group (container) (typed FeaturePython)
  Dunit = g/cm3
  Dvalue = 2.4
  Group = -> [O_element045,Na_element009,Si_element005,Ca_element011]
  conduct = 2
  density = 1
  expand = 3
  formula = G4_GLASS_PLATE
  name = G4_GLASS_PLATE
  specific = 4
FEATURE [App::DocumentObjectGroupPython] C_element049  label="C_element : 026"  # scripted group (container) (typed FeaturePython)
  n = 5
  ref = C_element
FEATURE [App::DocumentObjectGroupPython] H_element042  label="H_element : 021"  # scripted group (container) (typed FeaturePython)
  n = 10
  ref = H_element
FEATURE [App::DocumentObjectGroupPython] N_element019  label="N_element : 2"  # scripted group (container) (typed FeaturePython)
  n = 2
  ref = N_element
FEATURE [App::DocumentObjectGroupPython] O_element046  label="O_element : 022"  # scripted group (container) (typed FeaturePython)
  n = 3
  ref = O_element
FEATURE [App::DocumentObjectGroupPython] G4_GLUTAMINE  # scripted group (container) (typed FeaturePython)
  Dunit = g/cm3
  Dvalue = 1.46
  Group = -> [C_element049,H_element042,N_element019,O_element046]
  conduct = 2
  density = 1
  expand = 3
  formula = G4_GLUTAMINE
  name = G4_GLUTAMINE
  specific = 4
FEATURE [App::DocumentObjectGroupPython] C_element050  label="C_element : 027"  # scripted group (container) (typed FeaturePython)
  n = 3
  ref = C_element
FEATURE [App::DocumentObjectGroupPython] H_element043  label="H_element : 022"  # scripted group (container) (typed FeaturePython)
  n = 8
  ref = H_element
FEATURE [App::DocumentObjectGroupPython] O_element047  label="O_element : 023"  # scripted group (container) (typed FeaturePython)
  n = 3
  ref = O_element
FEATURE [App::DocumentObjectGroupPython] G4_GLYCEROL  # scripted group (container) (typed FeaturePython)
  Dunit = g/cm3
  Dvalue = 1.2613
  Group = -> [C_element050,H_element043,O_element047]
  conduct = 2
  density = 1
  expand = 3
  formula = G4_GLYCEROL
  name = G4_GLYCEROL
  specific = 4
FEATURE [App::DocumentObjectGroupPython] C_element051  label="C_element : 028"  # scripted group (container) (typed FeaturePython)
  n = 5
  ref = C_element
FEATURE [App::DocumentObjectGroupPython] H_element044  label="H_element : 023"  # scripted group (container) (typed FeaturePython)
  n = 5
  ref = H_element
FEATURE [App::DocumentObjectGroupPython] N_element020  label="N_element : 009"  # scripted group (container) (typed FeaturePython)
  n = 5
  ref = N_element
FEATURE [App::DocumentObjectGroupPython] O_element048  label="O_element : 024"  # scripted group (container) (typed FeaturePython)
  n = 1
  ref = O_element
FEATURE [App::DocumentObjectGroupPython] G4_GUANINE  # scripted group (container) (typed FeaturePython)
  Dunit = g/cm3
  Dvalue = 2.2
  Group = -> [C_element051,H_element044,N_element020,O_element048]
  conduct = 2
  density = 1
  expand = 3
  formula = G4_GUANINE
  name = G4_GUANINE
  specific = 4
FEATURE [App::DocumentObjectGroupPython] Ca_element012  label="Ca_element : 006"  # scripted group (container) (typed FeaturePython)
  n = 1
  ref = Ca_element
FEATURE [App::DocumentObjectGroupPython] S_element014  label="S_element : 005"  # scripted group (container) (typed FeaturePython)
  n = 1
  ref = S_element
FEATURE [App::DocumentObjectGroupPython] O_element049  label="O_element : 6"  # scripted group (container) (typed FeaturePython)
  n = 6
  ref = O_element
FEATURE [App::DocumentObjectGroupPython] H_element045  label="H_element : 024"  # scripted group (container) (typed FeaturePython)
  n = 4
  ref = H_element
FEATURE [App::DocumentObjectGroupPython] G4_GYPSUM  # scripted group (container) (typed FeaturePython)
  Dunit = g/cm3
  Dvalue = 2.32
  Group = -> [Ca_element012,S_element014,O_element049,H_element045]
  conduct = 2
  density = 1
  expand = 3
  formula = G4_GYPSUM
  name = G4_GYPSUM
  specific = 4
FEATURE [App::DocumentObjectGroupPython] C_element052  label="C_element : 7"  # scripted group (container) (typed FeaturePython)
  n = 7
  ref = C_element
FEATURE [App::DocumentObjectGroupPython] H_element046  label="H_element : 16"  # scripted group (container) (typed FeaturePython)
  n = 16
  ref = H_element
FEATURE [App::DocumentObjectGroupPython] G4_N_HEPTANE  label="G4_N-HEPTANE"  # scripted group (container) (typed FeaturePython)
  Dunit = g/cm3
  Dvalue = 0.68376
  Group = -> [C_element052,H_element046]
  conduct = 2
  density = 1
  expand = 3
  formula = G4_N-HEPTANE
  name = G4_N-HEPTANE
  specific = 4
FEATURE [App::DocumentObjectGroupPython] C_element053  label="C_element : 029"  # scripted group (container) (typed FeaturePython)
  n = 6
  ref = C_element
FEATURE [App::DocumentObjectGroupPython] H_element047  label="H_element : 14"  # scripted group (container) (typed FeaturePython)
  n = 14
  ref = H_element
FEATURE [App::DocumentObjectGroupPython] G4_N_HEXANE  label="G4_N-HEXANE"  # scripted group (container) (typed FeaturePython)
  Dunit = g/cm3
  Dvalue = 0.6603
  Group = -> [C_element053,H_element047]
  conduct = 2
  density = 1
  expand = 3
  formula = G4_N-HEXANE
  name = G4_N-HEXANE
  specific = 4
FEATURE [App::DocumentObjectGroupPython] C_element054  label="C_element : 22"  # scripted group (container) (typed FeaturePython)
  n = 22
  ref = C_element
FEATURE [App::DocumentObjectGroupPython] H_element048  label="H_element : 025"  # scripted group (container) (typed FeaturePython)
  n = 10
  ref = H_element
FEATURE [App::DocumentObjectGroupPython] N_element021  label="N_element : 010"  # scripted group (container) (typed FeaturePython)
  n = 2
  ref = N_element
FEATURE [App::DocumentObjectGroupPython] O_element050  label="O_element : 025"  # scripted group (container) (typed FeaturePython)
  n = 5
  ref = O_element
FEATURE [App::DocumentObjectGroupPython] G4_KAPTON  # scripted group (container) (typed FeaturePython)
  Dunit = g/cm3
  Dvalue = 1.42
  Group = -> [C_element054,H_element048,N_element021,O_element050]
  conduct = 2
  density = 1
  expand = 3
  formula = G4_KAPTON
  name = G4_KAPTON
  specific = 4
FEATURE [App::DocumentObjectGroupPython] La_element001  label="La_element : 1"  # scripted group (container) (typed FeaturePython)
  n = 1
  ref = La_element
FEATURE [App::DocumentObjectGroupPython] Br_element003  label="Br_element : 002"  # scripted group (container) (typed FeaturePython)
  n = 1
  ref = Br_element
FEATURE [App::DocumentObjectGroupPython] O_element051  label="O_element : 026"  # scripted group (container) (typed FeaturePython)
  n = 1
  ref = O_element
FEATURE [App::DocumentObjectGroupPython] G4_LANTHANUM_OXYBROMIDE  # scripted group (container) (typed FeaturePython)
  Dunit = g/cm3
  Dvalue = 6.28
  Group = -> [La_element001,Br_element003,O_element051]
  conduct = 2
  density = 1
  expand = 3
  formula = G4_LANTHANUM_OXYBROMIDE
  name = G4_LANTHANUM_OXYBROMIDE
  specific = 4
FEATURE [App::DocumentObjectGroupPython] La_element002  label="La_element : 2"  # scripted group (container) (typed FeaturePython)
  n = 2
  ref = La_element
FEATURE [App::DocumentObjectGroupPython] O_element052  label="O_element : 027"  # scripted group (container) (typed FeaturePython)
  n = 2
  ref = O_element
FEATURE [App::DocumentObjectGroupPython] S_element015  label="S_element : 006"  # scripted group (container) (typed FeaturePython)
  n = 1
  ref = S_element
FEATURE [App::DocumentObjectGroupPython] G4_LANTHANUM_OXYSULFIDE  # scripted group (container) (typed FeaturePython)
  Dunit = g/cm3
  Dvalue = 5.86
  Group = -> [La_element002,O_element052,S_element015]
  conduct = 2
  density = 1
  expand = 3
  formula = G4_LANTHANUM_OXYSULFIDE
  name = G4_LANTHANUM_OXYSULFIDE
  specific = 4
FEATURE [App::DocumentObjectGroupPython] O_element053  label="O_element : 0.072"  # scripted group (container) (typed FeaturePython)
  n = 0.071682
FEATURE [App::DocumentObjectGroupPython] Pb_element002  label="Pb_element : 0.928"  # scripted group (container) (typed FeaturePython)
  n = 0.928318
FEATURE [App::DocumentObjectGroupPython] G4_LEAD_OXIDE  # scripted group (container) (typed FeaturePython)
  Dunit = g/cm3
  Dvalue = 9.53
  Group = -> [O_element053,Pb_element002]
  conduct = 2
  density = 1
  expand = 3
  formula = G4_LEAD_OXIDE
  name = G4_LEAD_OXIDE
  specific = 4
FEATURE [App::DocumentObjectGroupPython] Li_element001  label="Li_element : 1"  # scripted group (container) (typed FeaturePython)
  n = 1
  ref = Li_element
FEATURE [App::DocumentObjectGroupPython] N_element022  label="N_element : 011"  # scripted group (container) (typed FeaturePython)
  n = 1
  ref = N_element
FEATURE [App::DocumentObjectGroupPython] H_element049  label="H_element : 026"  # scripted group (container) (typed FeaturePython)
  n = 2
  ref = H_element
FEATURE [App::DocumentObjectGroupPython] G4_LITHIUM_AMIDE  # scripted group (container) (typed FeaturePython)
  Dunit = g/cm3
  Dvalue = 1.178
  Group = -> [Li_element001,N_element022,H_element049]
  conduct = 2
  density = 1
  expand = 3
  formula = G4_LITHIUM_AMIDE
  name = G4_LITHIUM_AMIDE
  specific = 4
FEATURE [App::DocumentObjectGroupPython] Li_element002  label="Li_element : 2"  # scripted group (container) (typed FeaturePython)
  n = 2
  ref = Li_element
FEATURE [App::DocumentObjectGroupPython] C_element055  label="C_element : 030"  # scripted group (container) (typed FeaturePython)
  n = 1
  ref = C_element
FEATURE [App::DocumentObjectGroupPython] O_element054  label="O_element : 028"  # scripted group (container) (typed FeaturePython)
  n = 3
  ref = O_element
FEATURE [App::DocumentObjectGroupPython] G4_LITHIUM_CARBONATE  # scripted group (container) (typed FeaturePython)
  Dunit = g/cm3
  Dvalue = 2.11
  Group = -> [Li_element002,C_element055,O_element054]
  conduct = 2
  density = 1
  expand = 3
  formula = G4_LITHIUM_CARBONATE
  name = G4_LITHIUM_CARBONATE
  specific = 4
FEATURE [App::DocumentObjectGroupPython] Li_element003  label="Li_element : 003"  # scripted group (container) (typed FeaturePython)
  n = 1
  ref = Li_element
FEATURE [App::DocumentObjectGroupPython] F_element012  label="F_element : 004"  # scripted group (container) (typed FeaturePython)
  n = 1
  ref = F_element
FEATURE [App::DocumentObjectGroupPython] G4_LITHIUM_FLUORIDE  # scripted group (container) (typed FeaturePython)
  Dunit = g/cm3
  Dvalue = 2.635
  Group = -> [Li_element003,F_element012]
  conduct = 2
  density = 1
  expand = 3
  formula = G4_LITHIUM_FLUORIDE
  name = G4_LITHIUM_FLUORIDE
  specific = 4
FEATURE [App::DocumentObjectGroupPython] Li_element004  label="Li_element : 004"  # scripted group (container) (typed FeaturePython)
  n = 1
  ref = Li_element
FEATURE [App::DocumentObjectGroupPython] H_element050  label="H_element : 027"  # scripted group (container) (typed FeaturePython)
  n = 1
  ref = H_element
FEATURE [App::DocumentObjectGroupPython] G4_LITHIUM_HYDRIDE  # scripted group (container) (typed FeaturePython)
  Dunit = g/cm3
  Dvalue = 0.82
  Group = -> [Li_element004,H_element050]
  conduct = 2
  density = 1
  expand = 3
  formula = G4_LITHIUM_HYDRIDE
  name = G4_LITHIUM_HYDRIDE
  specific = 4
FEATURE [App::DocumentObjectGroupPython] Li_element005  label="Li_element : 005"  # scripted group (container) (typed FeaturePython)
  n = 1
  ref = Li_element
FEATURE [App::DocumentObjectGroupPython] I_element003  label="I_element : 002"  # scripted group (container) (typed FeaturePython)
  n = 1
  ref = I_element
FEATURE [App::DocumentObjectGroupPython] G4_LITHIUM_IODIDE  # scripted group (container) (typed FeaturePython)
  Dunit = g/cm3
  Dvalue = 3.494
  Group = -> [Li_element005,I_element003]
  conduct = 2
  density = 1
  expand = 3
  formula = G4_LITHIUM_IODIDE
  name = G4_LITHIUM_IODIDE
  specific = 4
FEATURE [App::DocumentObjectGroupPython] Li_element006  label="Li_element : 006"  # scripted group (container) (typed FeaturePython)
  n = 2
  ref = Li_element
FEATURE [App::DocumentObjectGroupPython] O_element055  label="O_element : 029"  # scripted group (container) (typed FeaturePython)
  n = 1
  ref = O_element
FEATURE [App::DocumentObjectGroupPython] G4_LITHIUM_OXIDE  # scripted group (container) (typed FeaturePython)
  Dunit = g/cm3
  Dvalue = 2.013
  Group = -> [Li_element006,O_element055]
  conduct = 2
  density = 1
  expand = 3
  formula = G4_LITHIUM_OXIDE
  name = G4_LITHIUM_OXIDE
  specific = 4
FEATURE [App::DocumentObjectGroupPython] Li_element007  label="Li_element : 007"  # scripted group (container) (typed FeaturePython)
  n = 2
  ref = Li_element
FEATURE [App::DocumentObjectGroupPython] B_element005  label="B_element : 005"  # scripted group (container) (typed FeaturePython)
  n = 4
  ref = B_element
FEATURE [App::DocumentObjectGroupPython] O_element056  label="O_element : 7"  # scripted group (container) (typed FeaturePython)
  n = 7
  ref = O_element
FEATURE [App::DocumentObjectGroupPython] G4_LITHIUM_TETRABORATE  # scripted group (container) (typed FeaturePython)
  Dunit = g/cm3
  Dvalue = 2.44
  Group = -> [Li_element007,B_element005,O_element056]
  conduct = 2
  density = 1
  expand = 3
  formula = G4_LITHIUM_TETRABORATE
  name = G4_LITHIUM_TETRABORATE
  specific = 4
FEATURE [App::DocumentObjectGroupPython] H_element051  label="H_element : 0.105"  # scripted group (container) (typed FeaturePython)
  n = 0.105
FEATURE [App::DocumentObjectGroupPython] C_element056  label="C_element : 0.083"  # scripted group (container) (typed FeaturePython)
  n = 0.083
FEATURE [App::DocumentObjectGroupPython] N_element023  label="N_element : 0.023"  # scripted group (container) (typed FeaturePython)
  n = 0.023
FEATURE [App::DocumentObjectGroupPython] O_element057  label="O_element : 0.779"  # scripted group (container) (typed FeaturePython)
  n = 0.779
FEATURE [App::DocumentObjectGroupPython] Na_element010  label="Na_element : 0.097"  # scripted group (container) (typed FeaturePython)
  n = 0.002
FEATURE [App::DocumentObjectGroupPython] P_element006  label="P_element : 0.105"  # scripted group (container) (typed FeaturePython)
  n = 0.001
FEATURE [App::DocumentObjectGroupPython] S_element016  label="S_element : 0.017"  # scripted group (container) (typed FeaturePython)
  n = 0.002
FEATURE [App::DocumentObjectGroupPython] Cl_element014  label="Cl_element : 0.587"  # scripted group (container) (typed FeaturePython)
  n = 0.003
FEATURE [App::DocumentObjectGroupPython] K_element005  label="K_element : 0.015"  # scripted group (container) (typed FeaturePython)
  n = 0.002
FEATURE [App::DocumentObjectGroupPython] G4_LUNG_ICRP  # scripted group (container) (typed FeaturePython)
  Dunit = g/cm3
  Dvalue = 1.04
  Group = -> [H_element051,C_element056,N_element023,O_element057,Na_element010,P_element006,S_element016,Cl_element014,K_element005]
  conduct = 2
  density = 1
  expand = 3
  formula = G4_LUNG_ICRP
  name = G4_LUNG_ICRP
  specific = 4
FEATURE [App::DocumentObjectGroupPython] H_element052  label="H_element : 0.116"  # scripted group (container) (typed FeaturePython)
  n = 0.114318
FEATURE [App::DocumentObjectGroupPython] C_element057  label="C_element : 0.656"  # scripted group (container) (typed FeaturePython)
  n = 0.655824
FEATURE [App::DocumentObjectGroupPython] O_element058  label="O_element : 0.092"  # scripted group (container) (typed FeaturePython)
  n = 0.0921831
FEATURE [App::DocumentObjectGroupPython] Mg_element004  label="Mg_element : 0.135"  # scripted group (container) (typed FeaturePython)
  n = 0.134792
FEATURE [App::DocumentObjectGroupPython] Ca_element013  label="Ca_element : 0.003"  # scripted group (container) (typed FeaturePython)
  n = 0.002883
FEATURE [App::DocumentObjectGroupPython] G4_M3_WAX  # scripted group (container) (typed FeaturePython)
  Dunit = g/cm3
  Dvalue = 1.05
  Group = -> [H_element052,C_element057,O_element058,Mg_element004,Ca_element013]
  conduct = 2
  density = 1
  expand = 3
  formula = G4_M3_WAX
  name = G4_M3_WAX
  specific = 4
FEATURE [App::DocumentObjectGroupPython] Mg_element005  label="Mg_element : 1"  # scripted group (container) (typed FeaturePython)
  n = 1
  ref = Mg_element
FEATURE [App::DocumentObjectGroupPython] C_element058  label="C_element : 031"  # scripted group (container) (typed FeaturePython)
  n = 1
  ref = C_element
FEATURE [App::DocumentObjectGroupPython] O_element059  label="O_element : 030"  # scripted group (container) (typed FeaturePython)
  n = 3
  ref = O_element
FEATURE [App::DocumentObjectGroupPython] G4_MAGNESIUM_CARBONATE  # scripted group (container) (typed FeaturePython)
  Dunit = g/cm3
  Dvalue = 2.958
  Group = -> [Mg_element005,C_element058,O_element059]
  conduct = 2
  density = 1
  expand = 3
  formula = G4_MAGNESIUM_CARBONATE
  name = G4_MAGNESIUM_CARBONATE
  specific = 4
FEATURE [App::DocumentObjectGroupPython] Mg_element006  label="Mg_element : 002"  # scripted group (container) (typed FeaturePython)
  n = 1
  ref = Mg_element
FEATURE [App::DocumentObjectGroupPython] F_element013  label="F_element : 005"  # scripted group (container) (typed FeaturePython)
  n = 2
  ref = F_element
FEATURE [App::DocumentObjectGroupPython] G4_MAGNESIUM_FLUORIDE  # scripted group (container) (typed FeaturePython)
  Dunit = g/cm3
  Dvalue = 3
  Group = -> [Mg_element006,F_element013]
  conduct = 2
  density = 1
  expand = 3
  formula = G4_MAGNESIUM_FLUORIDE
  name = G4_MAGNESIUM_FLUORIDE
  specific = 4
FEATURE [App::DocumentObjectGroupPython] Mg_element007  label="Mg_element : 003"  # scripted group (container) (typed FeaturePython)
  n = 1
  ref = Mg_element
FEATURE [App::DocumentObjectGroupPython] O_element060  label="O_element : 031"  # scripted group (container) (typed FeaturePython)
  n = 1
  ref = O_element
FEATURE [App::DocumentObjectGroupPython] G4_MAGNESIUM_OXIDE  # scripted group (container) (typed FeaturePython)
  Dunit = g/cm3
  Dvalue = 3.58
  Group = -> [Mg_element007,O_element060]
  conduct = 2
  density = 1
  expand = 3
  formula = G4_MAGNESIUM_OXIDE
  name = G4_MAGNESIUM_OXIDE
  specific = 4
FEATURE [App::DocumentObjectGroupPython] Mg_element008  label="Mg_element : 004"  # scripted group (container) (typed FeaturePython)
  n = 1
  ref = Mg_element
FEATURE [App::DocumentObjectGroupPython] B_element006  label="B_element : 006"  # scripted group (container) (typed FeaturePython)
  n = 4
  ref = B_element
FEATURE [App::DocumentObjectGroupPython] O_element061  label="O_element : 032"  # scripted group (container) (typed FeaturePython)
  n = 7
  ref = O_element
FEATURE [App::DocumentObjectGroupPython] G4_MAGNESIUM_TETRABORATE  # scripted group (container) (typed FeaturePython)
  Dunit = g/cm3
  Dvalue = 2.53
  Group = -> [Mg_element008,B_element006,O_element061]
  conduct = 2
  density = 1
  expand = 3
  formula = G4_MAGNESIUM_TETRABORATE
  name = G4_MAGNESIUM_TETRABORATE
  specific = 4
FEATURE [App::DocumentObjectGroupPython] Hg_element001  label="Hg_element : 1"  # scripted group (container) (typed FeaturePython)
  n = 1
  ref = Hg_element
FEATURE [App::DocumentObjectGroupPython] I_element004  label="I_element : 2"  # scripted group (container) (typed FeaturePython)
  n = 2
  ref = I_element
FEATURE [App::DocumentObjectGroupPython] G4_MERCURIC_IODIDE  # scripted group (container) (typed FeaturePython)
  Dunit = g/cm3
  Dvalue = 6.36
  Group = -> [Hg_element001,I_element004]
  conduct = 2
  density = 1
  expand = 3
  formula = G4_MERCURIC_IODIDE
  name = G4_MERCURIC_IODIDE
  specific = 4
FEATURE [App::DocumentObjectGroupPython] C_element059  label="C_element : 032"  # scripted group (container) (typed FeaturePython)
  n = 1
  ref = C_element
FEATURE [App::DocumentObjectGroupPython] H_element053  label="H_element : 028"  # scripted group (container) (typed FeaturePython)
  n = 4
  ref = H_element
FEATURE [App::DocumentObjectGroupPython] G4_METHANE  # scripted group (container) (typed FeaturePython)
  Dunit = g/cm3
  Dvalue = 0.000667151
  Group = -> [C_element059,H_element053]
  conduct = 2
  density = 1
  expand = 3
  formula = G4_METHANE
  name = G4_METHANE
  specific = 4
FEATURE [App::DocumentObjectGroupPython] C_element060  label="C_element : 033"  # scripted group (container) (typed FeaturePython)
  n = 1
  ref = C_element
FEATURE [App::DocumentObjectGroupPython] H_element054  label="H_element : 029"  # scripted group (container) (typed FeaturePython)
  n = 4
  ref = H_element
FEATURE [App::DocumentObjectGroupPython] O_element062  label="O_element : 033"  # scripted group (container) (typed FeaturePython)
  n = 1
  ref = O_element
FEATURE [App::DocumentObjectGroupPython] G4_METHANOL  # scripted group (container) (typed FeaturePython)
  Dunit = g/cm3
  Dvalue = 0.7914
  Group = -> [C_element060,H_element054,O_element062]
  conduct = 2
  density = 1
  expand = 3
  formula = G4_METHANOL
  name = G4_METHANOL
  specific = 4
FEATURE [App::DocumentObjectGroupPython] H_element055  label="H_element : 0.134"  # scripted group (container) (typed FeaturePython)
  n = 0.13404
FEATURE [App::DocumentObjectGroupPython] C_element061  label="C_element : 0.778"  # scripted group (container) (typed FeaturePython)
  n = 0.77796
FEATURE [App::DocumentObjectGroupPython] O_element063  label="O_element : 0.035"  # scripted group (container) (typed FeaturePython)
  n = 0.03502
FEATURE [App::DocumentObjectGroupPython] Mg_element009  label="Mg_element : 0.039"  # scripted group (container) (typed FeaturePython)
  n = 0.038594
FEATURE [App::DocumentObjectGroupPython] Ti_element002  label="Ti_element : 0.014"  # scripted group (container) (typed FeaturePython)
  n = 0.014386
FEATURE [App::DocumentObjectGroupPython] G4_MIX_D_WAX  # scripted group (container) (typed FeaturePython)
  Dunit = g/cm3
  Dvalue = 0.99
  Group = -> [H_element055,C_element061,O_element063,Mg_element009,Ti_element002]
  conduct = 2
  density = 1
  expand = 3
  formula = G4_MIX_D_WAX
  name = G4_MIX_D_WAX
  specific = 4
FEATURE [App::DocumentObjectGroupPython] H_element056  label="H_element : 0.135"  # scripted group (container) (typed FeaturePython)
  n = 0.081192
FEATURE [App::DocumentObjectGroupPython] C_element062  label="C_element : 0.583"  # scripted group (container) (typed FeaturePython)
  n = 0.583442
FEATURE [App::DocumentObjectGroupPython] N_element024  label="N_element : 0.018"  # scripted group (container) (typed FeaturePython)
  n = 0.017798
FEATURE [App::DocumentObjectGroupPython] O_element064  label="O_element : 0.186"  # scripted group (container) (typed FeaturePython)
  n = 0.186381
FEATURE [App::DocumentObjectGroupPython] Mg_element010  label="Mg_element : 0.130"  # scripted group (container) (typed FeaturePython)
  n = 0.130287
FEATURE [App::DocumentObjectGroupPython] Cl_element015  label="Cl_element : 0.588"  # scripted group (container) (typed FeaturePython)
  n = 0.0009
FEATURE [App::DocumentObjectGroupPython] G4_MS20_TISSUE  # scripted group (container) (typed FeaturePython)
  Dunit = g/cm3
  Dvalue = 1
  Group = -> [H_element056,C_element062,N_element024,O_element064,Mg_element010,Cl_element015]
  conduct = 2
  density = 1
  expand = 3
  formula = G4_MS20_TISSUE
  name = G4_MS20_TISSUE
  specific = 4
FEATURE [App::DocumentObjectGroupPython] H_element057  label="H_element : 0.136"  # scripted group (container) (typed FeaturePython)
  n = 0.102
FEATURE [App::DocumentObjectGroupPython] C_element063  label="C_element : 0.143"  # scripted group (container) (typed FeaturePython)
  n = 0.143
FEATURE [App::DocumentObjectGroupPython] N_element025  label="N_element : 0.034"  # scripted group (container) (typed FeaturePython)
  n = 0.034
FEATURE [App::DocumentObjectGroupPython] O_element065  label="O_element : 0.710"  # scripted group (container) (typed FeaturePython)
  n = 0.71
FEATURE [App::DocumentObjectGroupPython] Na_element011  label="Na_element : 0.098"  # scripted group (container) (typed FeaturePython)
  n = 0.001
FEATURE [App::DocumentObjectGroupPython] P_element007  label="P_element : 0.002"  # scripted group (container) (typed FeaturePython)
  n = 0.002
FEATURE [App::DocumentObjectGroupPython] S_element017  label="S_element : 0.018"  # scripted group (container) (typed FeaturePython)
  n = 0.003
FEATURE [App::DocumentObjectGroupPython] Cl_element016  label="Cl_element : 0.589"  # scripted group (container) (typed FeaturePython)
  n = 0.001
FEATURE [App::DocumentObjectGroupPython] K_element006  label="K_element : 0.004"  # scripted group (container) (typed FeaturePython)
  n = 0.004
FEATURE [App::DocumentObjectGroupPython] G4_MUSCLE_SKELETAL_ICRP  # scripted group (container) (typed FeaturePython)
  Dunit = g/cm3
  Dvalue = 1.05
  Group = -> [H_element057,C_element063,N_element025,O_element065,Na_element011,P_element007,S_element017,Cl_element016,K_element006]
  conduct = 2
  density = 1
  expand = 3
  formula = G4_MUSCLE_SKELETAL_ICRP
  name = G4_MUSCLE_SKELETAL_ICRP
  specific = 4
FEATURE [App::DocumentObjectGroupPython] H_element058  label="H_element : 0.137"  # scripted group (container) (typed FeaturePython)
  n = 0.102102
FEATURE [App::DocumentObjectGroupPython] C_element064  label="C_element : 0.123"  # scripted group (container) (typed FeaturePython)
  n = 0.123123
FEATURE [App::DocumentObjectGroupPython] N_element026  label="N_element : 0.756"  # scripted group (container) (typed FeaturePython)
  n = 0.035035
FEATURE [App::DocumentObjectGroupPython] O_element066  label="O_element : 0.730"  # scripted group (container) (typed FeaturePython)
  n = 0.72973
FEATURE [App::DocumentObjectGroupPython] Na_element012  label="Na_element : 0.099"  # scripted group (container) (typed FeaturePython)
  n = 0.001001
FEATURE [App::DocumentObjectGroupPython] P_element008  label="P_element : 0.106"  # scripted group (container) (typed FeaturePython)
  n = 0.002002
FEATURE [App::DocumentObjectGroupPython] S_element018  label="S_element : 0.019"  # scripted group (container) (typed FeaturePython)
  n = 0.004004
FEATURE [App::DocumentObjectGroupPython] K_element007  label="K_element : 0.016"  # scripted group (container) (typed FeaturePython)
  n = 0.003003
FEATURE [App::DocumentObjectGroupPython] G4_MUSCLE_STRIATED_ICRU  # scripted group (container) (typed FeaturePython)
  Dunit = g/cm3
  Dvalue = 1.04
  Group = -> [H_element058,C_element064,N_element026,O_element066,Na_element012,P_element008,S_element018,K_element007]
  conduct = 2
  density = 1
  expand = 3
  formula = G4_MUSCLE_STRIATED_ICRU
  name = G4_MUSCLE_STRIATED_ICRU
  specific = 4
FEATURE [App::DocumentObjectGroupPython] H_element059  label="H_element : 0.098"  # scripted group (container) (typed FeaturePython)
  n = 0.0982341
FEATURE [App::DocumentObjectGroupPython] C_element065  label="C_element : 0.156"  # scripted group (container) (typed FeaturePython)
  n = 0.156214
FEATURE [App::DocumentObjectGroupPython] N_element027  label="N_element : 0.757"  # scripted group (container) (typed FeaturePython)
  n = 0.035451
FEATURE [App::DocumentObjectGroupPython] O_element067  label="O_element : 0.880"  # scripted group (container) (typed FeaturePython)
  n = 0.710101
FEATURE [App::DocumentObjectGroupPython] G4_MUSCLE_WITH_SUCROSE  # scripted group (container) (typed FeaturePython)
  Dunit = g/cm3
  Dvalue = 1.11
  Group = -> [H_element059,C_element065,N_element027,O_element067]
  conduct = 2
  density = 1
  expand = 3
  formula = G4_MUSCLE_WITH_SUCROSE
  name = G4_MUSCLE_WITH_SUCROSE
  specific = 4
FEATURE [App::DocumentObjectGroupPython] H_element060  label="H_element : 0.138"  # scripted group (container) (typed FeaturePython)
  n = 0.101969
FEATURE [App::DocumentObjectGroupPython] C_element066  label="C_element : 0.120"  # scripted group (container) (typed FeaturePython)
  n = 0.120058
FEATURE [App::DocumentObjectGroupPython] N_element028  label="N_element : 0.758"  # scripted group (container) (typed FeaturePython)
  n = 0.035451
FEATURE [App::DocumentObjectGroupPython] O_element068  label="O_element : 0.743"  # scripted group (container) (typed FeaturePython)
  n = 0.742522
FEATURE [App::DocumentObjectGroupPython] G4_MUSCLE_WITHOUT_SUCROSE  # scripted group (container) (typed FeaturePython)
  Dunit = g/cm3
  Dvalue = 1.07
  Group = -> [H_element060,C_element066,N_element028,O_element068]
  conduct = 2
  density = 1
  expand = 3
  formula = G4_MUSCLE_WITHOUT_SUCROSE
  name = G4_MUSCLE_WITHOUT_SUCROSE
  specific = 4
FEATURE [App::DocumentObjectGroupPython] C_element067  label="C_element : 10"  # scripted group (container) (typed FeaturePython)
  n = 10
  ref = C_element
FEATURE [App::DocumentObjectGroupPython] H_element061  label="H_element : 030"  # scripted group (container) (typed FeaturePython)
  n = 8
  ref = H_element
FEATURE [App::DocumentObjectGroupPython] G4_NAPHTHALENE  # scripted group (container) (typed FeaturePython)
  Dunit = g/cm3
  Dvalue = 1.145
  Group = -> [C_element067,H_element061]
  conduct = 2
  density = 1
  expand = 3
  formula = G4_NAPHTHALENE
  name = G4_NAPHTHALENE
  specific = 4
FEATURE [App::DocumentObjectGroupPython] C_element068  label="C_element : 034"  # scripted group (container) (typed FeaturePython)
  n = 6
  ref = C_element
FEATURE [App::DocumentObjectGroupPython] H_element062  label="H_element : 031"  # scripted group (container) (typed FeaturePython)
  n = 5
  ref = H_element
FEATURE [App::DocumentObjectGroupPython] N_element029  label="N_element : 012"  # scripted group (container) (typed FeaturePython)
  n = 1
  ref = N_element
FEATURE [App::DocumentObjectGroupPython] O_element069  label="O_element : 034"  # scripted group (container) (typed FeaturePython)
  n = 2
  ref = O_element
FEATURE [App::DocumentObjectGroupPython] G4_NITROBENZENE  # scripted group (container) (typed FeaturePython)
  Dunit = g/cm3
  Dvalue = 1.19867
  Group = -> [C_element068,H_element062,N_element029,O_element069]
  conduct = 2
  density = 1
  expand = 3
  formula = G4_NITROBENZENE
  name = G4_NITROBENZENE
  specific = 4
FEATURE [App::DocumentObjectGroupPython] N_element030  label="N_element : 013"  # scripted group (container) (typed FeaturePython)
  n = 2
  ref = N_element
FEATURE [App::DocumentObjectGroupPython] O_element070  label="O_element : 035"  # scripted group (container) (typed FeaturePython)
  n = 1
  ref = O_element
FEATURE [App::DocumentObjectGroupPython] G4_NITROUS_OXIDE  # scripted group (container) (typed FeaturePython)
  Dunit = g/cm3
  Dvalue = 0.00183094
  Group = -> [N_element030,O_element070]
  conduct = 2
  density = 1
  expand = 3
  formula = G4_NITROUS_OXIDE
  name = G4_NITROUS_OXIDE
  specific = 4
FEATURE [App::DocumentObjectGroupPython] H_element063  label="H_element : 0.104"  # scripted group (container) (typed FeaturePython)
  n = 0.103509
FEATURE [App::DocumentObjectGroupPython] C_element069  label="C_element : 0.648"  # scripted group (container) (typed FeaturePython)
  n = 0.648416
FEATURE [App::DocumentObjectGroupPython] N_element031  label="N_element : 0.100"  # scripted group (container) (typed FeaturePython)
  n = 0.0995361
FEATURE [App::DocumentObjectGroupPython] O_element071  label="O_element : 0.149"  # scripted group (container) (typed FeaturePython)
  n = 0.148539
FEATURE [App::DocumentObjectGroupPython] G4_NYLON_8062  label="G4_NYLON-8062"  # scripted group (container) (typed FeaturePython)
  Dunit = g/cm3
  Dvalue = 1.08
  Group = -> [H_element063,C_element069,N_element031,O_element071]
  conduct = 2
  density = 1
  expand = 3
  formula = G4_NYLON-8062
  name = G4_NYLON-8062
  specific = 4
FEATURE [App::DocumentObjectGroupPython] C_element070  label="C_element : 035"  # scripted group (container) (typed FeaturePython)
  n = 6
  ref = C_element
FEATURE [App::DocumentObjectGroupPython] H_element064  label="H_element : 11"  # scripted group (container) (typed FeaturePython)
  n = 11
  ref = H_element
FEATURE [App::DocumentObjectGroupPython] N_element032  label="N_element : 014"  # scripted group (container) (typed FeaturePython)
  n = 1
  ref = N_element
FEATURE [App::DocumentObjectGroupPython] O_element072  label="O_element : 036"  # scripted group (container) (typed FeaturePython)
  n = 1
  ref = O_element
FEATURE [App::DocumentObjectGroupPython] G4_NYLON_6_6  label="G4_NYLON-6-6"  # scripted group (container) (typed FeaturePython)
  Dunit = g/cm3
  Dvalue = 1.14
  Group = -> [C_element070,H_element064,N_element032,O_element072]
  conduct = 2
  density = 1
  expand = 3
  formula = G4_NYLON-6-6
  name = G4_NYLON-6-6
  specific = 4
FEATURE [App::DocumentObjectGroupPython] H_element065  label="H_element : 0.139"  # scripted group (container) (typed FeaturePython)
  n = 0.107062
FEATURE [App::DocumentObjectGroupPython] C_element071  label="C_element : 0.680"  # scripted group (container) (typed FeaturePython)
  n = 0.680449
FEATURE [App::DocumentObjectGroupPython] N_element033  label="N_element : 0.099"  # scripted group (container) (typed FeaturePython)
  n = 0.099189
FEATURE [App::DocumentObjectGroupPython] O_element073  label="O_element : 0.113"  # scripted group (container) (typed FeaturePython)
  n = 0.1133
FEATURE [App::DocumentObjectGroupPython] G4_NYLON_6_10  label="G4_NYLON-6-10"  # scripted group (container) (typed FeaturePython)
  Dunit = g/cm3
  Dvalue = 1.14
  Group = -> [H_element065,C_element071,N_element033,O_element073]
  conduct = 2
  density = 1
  expand = 3
  formula = G4_NYLON-6-10
  name = G4_NYLON-6-10
  specific = 4
FEATURE [App::DocumentObjectGroupPython] H_element066  label="H_element : 0.140"  # scripted group (container) (typed FeaturePython)
  n = 0.115476
FEATURE [App::DocumentObjectGroupPython] C_element072  label="C_element : 0.721"  # scripted group (container) (typed FeaturePython)
  n = 0.720818
FEATURE [App::DocumentObjectGroupPython] N_element034  label="N_element : 0.076"  # scripted group (container) (typed FeaturePython)
  n = 0.0764169
FEATURE [App::DocumentObjectGroupPython] O_element074  label="O_element : 0.087"  # scripted group (container) (typed FeaturePython)
  n = 0.0872889
FEATURE [App::DocumentObjectGroupPython] G4_NYLON_11_RILSAN  label="G4_NYLON-11_RILSAN"  # scripted group (container) (typed FeaturePython)
  Dunit = g/cm3
  Dvalue = 1.425
  Group = -> [H_element066,C_element072,N_element034,O_element074]
  conduct = 2
  density = 1
  expand = 3
  formula = G4_NYLON-11_RILSAN
  name = G4_NYLON-11_RILSAN
  specific = 4
FEATURE [App::DocumentObjectGroupPython] C_element073  label="C_element : 8"  # scripted group (container) (typed FeaturePython)
  n = 8
  ref = C_element
FEATURE [App::DocumentObjectGroupPython] H_element067  label="H_element : 18"  # scripted group (container) (typed FeaturePython)
  n = 18
  ref = H_element
FEATURE [App::DocumentObjectGroupPython] G4_OCTANE  # scripted group (container) (typed FeaturePython)
  Dunit = g/cm3
  Dvalue = 0.7026
  Group = -> [C_element073,H_element067]
  conduct = 2
  density = 1
  expand = 3
  formula = G4_OCTANE
  name = G4_OCTANE
  specific = 4
FEATURE [App::DocumentObjectGroupPython] C_element074  label="C_element : 25"  # scripted group (container) (typed FeaturePython)
  n = 25
  ref = C_element
FEATURE [App::DocumentObjectGroupPython] H_element068  label="H_element : 52"  # scripted group (container) (typed FeaturePython)
  n = 52
  ref = H_element
FEATURE [App::DocumentObjectGroupPython] G4_PARAFFIN  # scripted group (container) (typed FeaturePython)
  Dunit = g/cm3
  Dvalue = 0.93
  Group = -> [C_element074,H_element068]
  conduct = 2
  density = 1
  expand = 3
  formula = G4_PARAFFIN
  name = G4_PARAFFIN
  specific = 4
FEATURE [App::DocumentObjectGroupPython] C_element075  label="C_element : 036"  # scripted group (container) (typed FeaturePython)
  n = 5
  ref = C_element
FEATURE [App::DocumentObjectGroupPython] H_element069  label="H_element : 032"  # scripted group (container) (typed FeaturePython)
  n = 12
  ref = H_element
FEATURE [App::DocumentObjectGroupPython] G4_N_PENTANE  label="G4_N-PENTANE"  # scripted group (container) (typed FeaturePython)
  Dunit = g/cm3
  Dvalue = 0.6262
  Group = -> [C_element075,H_element069]
  conduct = 2
  density = 1
  expand = 3
  formula = G4_N-PENTANE
  name = G4_N-PENTANE
  specific = 4
FEATURE [App::DocumentObjectGroupPython] H_element070  label="H_element : 0.014"  # scripted group (container) (typed FeaturePython)
  n = 0.0141
FEATURE [App::DocumentObjectGroupPython] C_element076  label="C_element : 0.072"  # scripted group (container) (typed FeaturePython)
  n = 0.072261
FEATURE [App::DocumentObjectGroupPython] N_element035  label="N_element : 0.019"  # scripted group (container) (typed FeaturePython)
  n = 0.01932
FEATURE [App::DocumentObjectGroupPython] O_element075  label="O_element : 0.066"  # scripted group (container) (typed FeaturePython)
  n = 0.066101
FEATURE [App::DocumentObjectGroupPython] S_element019  label="S_element : 0.020"  # scripted group (container) (typed FeaturePython)
  n = 0.00189
FEATURE [App::DocumentObjectGroupPython] Br_element004  label="Br_element : 0.349"  # scripted group (container) (typed FeaturePython)
  n = 0.349103
FEATURE [App::DocumentObjectGroupPython] Ag_element001  label="Ag_element : 0.474"  # scripted group (container) (typed FeaturePython)
  n = 0.474105
FEATURE [App::DocumentObjectGroupPython] I_element005  label="I_element : 0.003"  # scripted group (container) (typed FeaturePython)
  n = 0.00312
FEATURE [App::DocumentObjectGroupPython] G4_PHOTO_EMULSION  # scripted group (container) (typed FeaturePython)
  Dunit = g/cm3
  Dvalue = 3.815
  Group = -> [H_element070,C_element076,N_element035,O_element075,S_element019,Br_element004,Ag_element001,I_element005]
  conduct = 2
  density = 1
  expand = 3
  formula = G4_PHOTO_EMULSION
  name = G4_PHOTO_EMULSION
  specific = 4
FEATURE [App::DocumentObjectGroupPython] C_element077  label="C_element : 9"  # scripted group (container) (typed FeaturePython)
  n = 9
  ref = C_element
FEATURE [App::DocumentObjectGroupPython] H_element071  label="H_element : 033"  # scripted group (container) (typed FeaturePython)
  n = 10
  ref = H_element
FEATURE [App::DocumentObjectGroupPython] G4_PLASTIC_SC_VINYLTOLUENE  # scripted group (container) (typed FeaturePython)
  Dunit = g/cm3
  Dvalue = 1.032
  Group = -> [C_element077,H_element071]
  conduct = 2
  density = 1
  expand = 3
  formula = G4_PLASTIC_SC_VINYLTOLUENE
  name = G4_PLASTIC_SC_VINYLTOLUENE
  specific = 4
FEATURE [App::DocumentObjectGroupPython] Pu_element001  label="Pu_element : 1"  # scripted group (container) (typed FeaturePython)
  n = 1
  ref = Pu_element
FEATURE [App::DocumentObjectGroupPython] O_element076  label="O_element : 037"  # scripted group (container) (typed FeaturePython)
  n = 2
  ref = O_element
FEATURE [App::DocumentObjectGroupPython] G4_PLUTONIUM_DIOXIDE  # scripted group (container) (typed FeaturePython)
  Dunit = g/cm3
  Dvalue = 11.46
  Group = -> [Pu_element001,O_element076]
  conduct = 2
  density = 1
  expand = 3
  formula = G4_PLUTONIUM_DIOXIDE
  name = G4_PLUTONIUM_DIOXIDE
  specific = 4
FEATURE [App::DocumentObjectGroupPython] C_element078  label="C_element : 037"  # scripted group (container) (typed FeaturePython)
  n = 3
  ref = C_element
FEATURE [App::DocumentObjectGroupPython] H_element072  label="H_element : 034"  # scripted group (container) (typed FeaturePython)
  n = 3
  ref = H_element
FEATURE [App::DocumentObjectGroupPython] N_element036  label="N_element : 015"  # scripted group (container) (typed FeaturePython)
  n = 1
  ref = N_element
FEATURE [App::DocumentObjectGroupPython] G4_POLYACRYLONITRILE  # scripted group (container) (typed FeaturePython)
  Dunit = g/cm3
  Dvalue = 1.17
  Group = -> [C_element078,H_element072,N_element036]
  conduct = 2
  density = 1
  expand = 3
  formula = G4_POLYACRYLONITRILE
  name = G4_POLYACRYLONITRILE
  specific = 4
FEATURE [App::DocumentObjectGroupPython] C_element079  label="C_element : 16"  # scripted group (container) (typed FeaturePython)
  n = 16
  ref = C_element
FEATURE [App::DocumentObjectGroupPython] H_element073  label="H_element : 035"  # scripted group (container) (typed FeaturePython)
  n = 14
  ref = H_element
FEATURE [App::DocumentObjectGroupPython] O_element077  label="O_element : 038"  # scripted group (container) (typed FeaturePython)
  n = 3
  ref = O_element
FEATURE [App::DocumentObjectGroupPython] G4_POLYCARBONATE  # scripted group (container) (typed FeaturePython)
  Dunit = g/cm3
  Dvalue = 1.2
  Group = -> [C_element079,H_element073,O_element077]
  conduct = 2
  density = 1
  expand = 3
  formula = G4_POLYCARBONATE
  name = G4_POLYCARBONATE
  specific = 4
FEATURE [App::DocumentObjectGroupPython] C_element080  label="C_element : 038"  # scripted group (container) (typed FeaturePython)
  n = 8
  ref = C_element
FEATURE [App::DocumentObjectGroupPython] H_element074  label="H_element : 036"  # scripted group (container) (typed FeaturePython)
  n = 7
  ref = H_element
FEATURE [App::DocumentObjectGroupPython] Cl_element017  label="Cl_element : 007"  # scripted group (container) (typed FeaturePython)
  n = 1
  ref = Cl_element
FEATURE [App::DocumentObjectGroupPython] G4_POLYCHLOROSTYRENE  # scripted group (container) (typed FeaturePython)
  Dunit = g/cm3
  Dvalue = 1.3
  Group = -> [C_element080,H_element074,Cl_element017]
  conduct = 2
  density = 1
  expand = 3
  formula = G4_POLYCHLOROSTYRENE
  name = G4_POLYCHLOROSTYRENE
  specific = 4
FEATURE [App::DocumentObjectGroupPython] C_element081  label="C_element : 039"  # scripted group (container) (typed FeaturePython)
  n = 1
  ref = C_element
FEATURE [App::DocumentObjectGroupPython] H_element075  label="H_element : 037"  # scripted group (container) (typed FeaturePython)
  n = 2
  ref = H_element
FEATURE [App::DocumentObjectGroupPython] G4_POLYETHYLENE  # scripted group (container) (typed FeaturePython)
  Dunit = g/cm3
  Dvalue = 0.94
  Group = -> [C_element081,H_element075]
  conduct = 2
  density = 1
  expand = 3
  formula = G4_POLYETHYLENE
  name = G4_POLYETHYLENE
  specific = 4
FEATURE [App::DocumentObjectGroupPython] C_element082  label="C_element : 040"  # scripted group (container) (typed FeaturePython)
  n = 10
  ref = C_element
FEATURE [App::DocumentObjectGroupPython] H_element076  label="H_element : 038"  # scripted group (container) (typed FeaturePython)
  n = 8
  ref = H_element
FEATURE [App::DocumentObjectGroupPython] O_element078  label="O_element : 039"  # scripted group (container) (typed FeaturePython)
  n = 4
  ref = O_element
FEATURE [App::DocumentObjectGroupPython] G4_MYLAR  # scripted group (container) (typed FeaturePython)
  Dunit = g/cm3
  Dvalue = 1.4
  Group = -> [C_element082,H_element076,O_element078]
  conduct = 2
  density = 1
  expand = 3
  formula = G4_MYLAR
  name = G4_MYLAR
  specific = 4
FEATURE [App::DocumentObjectGroupPython] C_element083  label="C_element : 041"  # scripted group (container) (typed FeaturePython)
  n = 5
  ref = C_element
FEATURE [App::DocumentObjectGroupPython] H_element077  label="H_element : 039"  # scripted group (container) (typed FeaturePython)
  n = 8
  ref = H_element
FEATURE [App::DocumentObjectGroupPython] O_element079  label="O_element : 040"  # scripted group (container) (typed FeaturePython)
  n = 2
  ref = O_element
FEATURE [App::DocumentObjectGroupPython] G4_PLEXIGLASS  # scripted group (container) (typed FeaturePython)
  Dunit = g/cm3
  Dvalue = 1.19
  Group = -> [C_element083,H_element077,O_element079]
  conduct = 2
  density = 1
  expand = 3
  formula = G4_PLEXIGLASS
  name = G4_PLEXIGLASS
  specific = 4
FEATURE [App::DocumentObjectGroupPython] C_element084  label="C_element : 042"  # scripted group (container) (typed FeaturePython)
  n = 1
  ref = C_element
FEATURE [App::DocumentObjectGroupPython] H_element078  label="H_element : 040"  # scripted group (container) (typed FeaturePython)
  n = 2
  ref = H_element
FEATURE [App::DocumentObjectGroupPython] O_element080  label="O_element : 041"  # scripted group (container) (typed FeaturePython)
  n = 1
  ref = O_element
FEATURE [App::DocumentObjectGroupPython] G4_POLYOXYMETHYLENE  # scripted group (container) (typed FeaturePython)
  Dunit = g/cm3
  Dvalue = 1.425
  Group = -> [C_element084,H_element078,O_element080]
  conduct = 2
  density = 1
  expand = 3
  formula = G4_POLYOXYMETHYLENE
  name = G4_POLYOXYMETHYLENE
  specific = 4
FEATURE [App::DocumentObjectGroupPython] C_element085  label="C_element : 043"  # scripted group (container) (typed FeaturePython)
  n = 2
  ref = C_element
FEATURE [App::DocumentObjectGroupPython] H_element079  label="H_element : 041"  # scripted group (container) (typed FeaturePython)
  n = 4
  ref = H_element
FEATURE [App::DocumentObjectGroupPython] G4_POLYPROPYLENE  # scripted group (container) (typed FeaturePython)
  Dunit = g/cm3
  Dvalue = 0.9
  Group = -> [C_element085,H_element079]
  conduct = 2
  density = 1
  expand = 3
  formula = G4_POLYPROPYLENE
  name = G4_POLYPROPYLENE
  specific = 4
FEATURE [App::DocumentObjectGroupPython] C_element086  label="C_element : 044"  # scripted group (container) (typed FeaturePython)
  n = 8
  ref = C_element
FEATURE [App::DocumentObjectGroupPython] H_element080  label="H_element : 042"  # scripted group (container) (typed FeaturePython)
  n = 8
  ref = H_element
FEATURE [App::DocumentObjectGroupPython] G4_POLYSTYRENE  # scripted group (container) (typed FeaturePython)
  Dunit = g/cm3
  Dvalue = 1.06
  Group = -> [C_element086,H_element080]
  conduct = 2
  density = 1
  expand = 3
  formula = G4_POLYSTYRENE
  name = G4_POLYSTYRENE
  specific = 4
FEATURE [App::DocumentObjectGroupPython] C_element087  label="C_element : 045"  # scripted group (container) (typed FeaturePython)
  n = 2
  ref = C_element
FEATURE [App::DocumentObjectGroupPython] F_element014  label="F_element : 4"  # scripted group (container) (typed FeaturePython)
  n = 4
  ref = F_element
FEATURE [App::DocumentObjectGroupPython] G4_TEFLON  # scripted group (container) (typed FeaturePython)
  Dunit = g/cm3
  Dvalue = 2.2
  Group = -> [C_element087,F_element014]
  conduct = 2
  density = 1
  expand = 3
  formula = G4_TEFLON
  name = G4_TEFLON
  specific = 4
FEATURE [App::DocumentObjectGroupPython] C_element088  label="C_element : 046"  # scripted group (container) (typed FeaturePython)
  n = 2
  ref = C_element
FEATURE [App::DocumentObjectGroupPython] F_element015  label="F_element : 006"  # scripted group (container) (typed FeaturePython)
  n = 3
  ref = F_element
FEATURE [App::DocumentObjectGroupPython] Cl_element018  label="Cl_element : 008"  # scripted group (container) (typed FeaturePython)
  n = 1
  ref = Cl_element
FEATURE [App::DocumentObjectGroupPython] G4_POLYTRIFLUOROCHLOROETHYLENE  # scripted group (container) (typed FeaturePython)
  Dunit = g/cm3
  Dvalue = 2.1
  Group = -> [C_element088,F_element015,Cl_element018]
  conduct = 2
  density = 1
  expand = 3
  formula = G4_POLYTRIFLUOROCHLOROETHYLENE
  name = G4_POLYTRIFLUOROCHLOROETHYLENE
  specific = 4
FEATURE [App::DocumentObjectGroupPython] C_element089  label="C_element : 047"  # scripted group (container) (typed FeaturePython)
  n = 4
  ref = C_element
FEATURE [App::DocumentObjectGroupPython] H_element081  label="H_element : 043"  # scripted group (container) (typed FeaturePython)
  n = 6
  ref = H_element
FEATURE [App::DocumentObjectGroupPython] O_element081  label="O_element : 042"  # scripted group (container) (typed FeaturePython)
  n = 2
  ref = O_element
FEATURE [App::DocumentObjectGroupPython] G4_POLYVINYL_ACETATE  # scripted group (container) (typed FeaturePython)
  Dunit = g/cm3
  Dvalue = 1.19
  Group = -> [C_element089,H_element081,O_element081]
  conduct = 2
  density = 1
  expand = 3
  formula = G4_POLYVINYL_ACETATE
  name = G4_POLYVINYL_ACETATE
  specific = 4
FEATURE [App::DocumentObjectGroupPython] C_element090  label="C_element : 048"  # scripted group (container) (typed FeaturePython)
  n = 2
  ref = C_element
FEATURE [App::DocumentObjectGroupPython] H_element082  label="H_element : 044"  # scripted group (container) (typed FeaturePython)
  n = 4
  ref = H_element
FEATURE [App::DocumentObjectGroupPython] O_element082  label="O_element : 043"  # scripted group (container) (typed FeaturePython)
  n = 1
  ref = O_element
FEATURE [App::DocumentObjectGroupPython] G4_POLYVINYL_ALCOHOL  # scripted group (container) (typed FeaturePython)
  Dunit = g/cm3
  Dvalue = 1.3
  Group = -> [C_element090,H_element082,O_element082]
  conduct = 2
  density = 1
  expand = 3
  formula = G4_POLYVINYL_ALCOHOL
  name = G4_POLYVINYL_ALCOHOL
  specific = 4
FEATURE [App::DocumentObjectGroupPython] C_element091  label="C_element : 049"  # scripted group (container) (typed FeaturePython)
  n = 8
  ref = C_element
FEATURE [App::DocumentObjectGroupPython] H_element083  label="H_element : 045"  # scripted group (container) (typed FeaturePython)
  n = 14
  ref = H_element
FEATURE [App::DocumentObjectGroupPython] O_element083  label="O_element : 044"  # scripted group (container) (typed FeaturePython)
  n = 2
  ref = O_element
FEATURE [App::DocumentObjectGroupPython] G4_POLYVINYL_BUTYRAL  # scripted group (container) (typed FeaturePython)
  Dunit = g/cm3
  Dvalue = 1.12
  Group = -> [C_element091,H_element083,O_element083]
  conduct = 2
  density = 1
  expand = 3
  formula = G4_POLYVINYL_BUTYRAL
  name = G4_POLYVINYL_BUTYRAL
  specific = 4
FEATURE [App::DocumentObjectGroupPython] C_element092  label="C_element : 050"  # scripted group (container) (typed FeaturePython)
  n = 2
  ref = C_element
FEATURE [App::DocumentObjectGroupPython] H_element084  label="H_element : 046"  # scripted group (container) (typed FeaturePython)
  n = 3
  ref = H_element
FEATURE [App::DocumentObjectGroupPython] Cl_element019  label="Cl_element : 009"  # scripted group (container) (typed FeaturePython)
  n = 1
  ref = Cl_element
FEATURE [App::DocumentObjectGroupPython] G4_POLYVINYL_CHLORIDE  # scripted group (container) (typed FeaturePython)
  Dunit = g/cm3
  Dvalue = 1.3
  Group = -> [C_element092,H_element084,Cl_element019]
  conduct = 2
  density = 1
  expand = 3
  formula = G4_POLYVINYL_CHLORIDE
  name = G4_POLYVINYL_CHLORIDE
  specific = 4
FEATURE [App::DocumentObjectGroupPython] C_element093  label="C_element : 051"  # scripted group (container) (typed FeaturePython)
  n = 2
  ref = C_element
FEATURE [App::DocumentObjectGroupPython] H_element085  label="H_element : 047"  # scripted group (container) (typed FeaturePython)
  n = 2
  ref = H_element
FEATURE [App::DocumentObjectGroupPython] Cl_element020  label="Cl_element : 010"  # scripted group (container) (typed FeaturePython)
  n = 2
  ref = Cl_element
FEATURE [App::DocumentObjectGroupPython] G4_POLYVINYLIDENE_CHLORIDE  # scripted group (container) (typed FeaturePython)
  Dunit = g/cm3
  Dvalue = 1.7
  Group = -> [C_element093,H_element085,Cl_element020]
  conduct = 2
  density = 1
  expand = 3
  formula = G4_POLYVINYLIDENE_CHLORIDE
  name = G4_POLYVINYLIDENE_CHLORIDE
  specific = 4
FEATURE [App::DocumentObjectGroupPython] C_element094  label="C_element : 052"  # scripted group (container) (typed FeaturePython)
  n = 2
  ref = C_element
FEATURE [App::DocumentObjectGroupPython] H_element086  label="H_element : 048"  # scripted group (container) (typed FeaturePython)
  n = 2
  ref = H_element
FEATURE [App::DocumentObjectGroupPython] F_element016  label="F_element : 007"  # scripted group (container) (typed FeaturePython)
  n = 2
  ref = F_element
FEATURE [App::DocumentObjectGroupPython] G4_POLYVINYLIDENE_FLUORIDE  # scripted group (container) (typed FeaturePython)
  Dunit = g/cm3
  Dvalue = 1.76
  Group = -> [C_element094,H_element086,F_element016]
  conduct = 2
  density = 1
  expand = 3
  formula = G4_POLYVINYLIDENE_FLUORIDE
  name = G4_POLYVINYLIDENE_FLUORIDE
  specific = 4
FEATURE [App::DocumentObjectGroupPython] C_element095  label="C_element : 053"  # scripted group (container) (typed FeaturePython)
  n = 6
  ref = C_element
FEATURE [App::DocumentObjectGroupPython] H_element087  label="H_element : 9"  # scripted group (container) (typed FeaturePython)
  n = 9
  ref = H_element
FEATURE [App::DocumentObjectGroupPython] N_element037  label="N_element : 016"  # scripted group (container) (typed FeaturePython)
  n = 1
  ref = N_element
FEATURE [App::DocumentObjectGroupPython] O_element084  label="O_element : 045"  # scripted group (container) (typed FeaturePython)
  n = 1
  ref = O_element
FEATURE [App::DocumentObjectGroupPython] G4_POLYVINYL_PYRROLIDONE  # scripted group (container) (typed FeaturePython)
  Dunit = g/cm3
  Dvalue = 1.25
  Group = -> [C_element095,H_element087,N_element037,O_element084]
  conduct = 2
  density = 1
  expand = 3
  formula = G4_POLYVINYL_PYRROLIDONE
  name = G4_POLYVINYL_PYRROLIDONE
  specific = 4
FEATURE [App::DocumentObjectGroupPython] K_element008  label="K_element : 1"  # scripted group (container) (typed FeaturePython)
  n = 1
  ref = K_element
FEATURE [App::DocumentObjectGroupPython] I_element006  label="I_element : 003"  # scripted group (container) (typed FeaturePython)
  n = 1
  ref = I_element
FEATURE [App::DocumentObjectGroupPython] G4_POTASSIUM_IODIDE  # scripted group (container) (typed FeaturePython)
  Dunit = g/cm3
  Dvalue = 3.13
  Group = -> [K_element008,I_element006]
  conduct = 2
  density = 1
  expand = 3
  formula = G4_POTASSIUM_IODIDE
  name = G4_POTASSIUM_IODIDE
  specific = 4
FEATURE [App::DocumentObjectGroupPython] K_element009  label="K_element : 2"  # scripted group (container) (typed FeaturePython)
  n = 2
  ref = K_element
FEATURE [App::DocumentObjectGroupPython] O_element085  label="O_element : 046"  # scripted group (container) (typed FeaturePython)
  n = 1
  ref = O_element
FEATURE [App::DocumentObjectGroupPython] G4_POTASSIUM_OXIDE  # scripted group (container) (typed FeaturePython)
  Dunit = g/cm3
  Dvalue = 2.32
  Group = -> [K_element009,O_element085]
  conduct = 2
  density = 1
  expand = 3
  formula = G4_POTASSIUM_OXIDE
  name = G4_POTASSIUM_OXIDE
  specific = 4
FEATURE [App::DocumentObjectGroupPython] C_element096  label="C_element : 054"  # scripted group (container) (typed FeaturePython)
  n = 3
  ref = C_element
FEATURE [App::DocumentObjectGroupPython] H_element088  label="H_element : 049"  # scripted group (container) (typed FeaturePython)
  n = 8
  ref = H_element
FEATURE [App::DocumentObjectGroupPython] G4_PROPANE  # scripted group (container) (typed FeaturePython)
  Dunit = g/cm3
  Dvalue = 0.00187939
  Group = -> [C_element096,H_element088]
  conduct = 2
  density = 1
  expand = 3
  formula = G4_PROPANE
  name = G4_PROPANE
  specific = 4
FEATURE [App::DocumentObjectGroupPython] C_element097  label="C_element : 055"  # scripted group (container) (typed FeaturePython)
  n = 3
  ref = C_element
FEATURE [App::DocumentObjectGroupPython] H_element089  label="H_element : 050"  # scripted group (container) (typed FeaturePython)
  n = 8
  ref = H_element
FEATURE [App::DocumentObjectGroupPython] G4_lPROPANE  # scripted group (container) (typed FeaturePython)
  Dunit = g/cm3
  Dvalue = 0.43
  Group = -> [C_element097,H_element089]
  conduct = 2
  density = 1
  expand = 3
  formula = G4_lPROPANE
  name = G4_lPROPANE
  specific = 4
FEATURE [App::DocumentObjectGroupPython] C_element098  label="C_element : 056"  # scripted group (container) (typed FeaturePython)
  n = 3
  ref = C_element
FEATURE [App::DocumentObjectGroupPython] H_element090  label="H_element : 051"  # scripted group (container) (typed FeaturePython)
  n = 8
  ref = H_element
FEATURE [App::DocumentObjectGroupPython] O_element086  label="O_element : 047"  # scripted group (container) (typed FeaturePython)
  n = 1
  ref = O_element
FEATURE [App::DocumentObjectGroupPython] G4_N_PROPYL_ALCOHOL  label="G4_N-PROPYL_ALCOHOL"  # scripted group (container) (typed FeaturePython)
  Dunit = g/cm3
  Dvalue = 0.8035
  Group = -> [C_element098,H_element090,O_element086]
  conduct = 2
  density = 1
  expand = 3
  formula = G4_N-PROPYL_ALCOHOL
  name = G4_N-PROPYL_ALCOHOL
  specific = 4
FEATURE [App::DocumentObjectGroupPython] C_element099  label="C_element : 057"  # scripted group (container) (typed FeaturePython)
  n = 5
  ref = C_element
FEATURE [App::DocumentObjectGroupPython] H_element091  label="H_element : 052"  # scripted group (container) (typed FeaturePython)
  n = 5
  ref = H_element
FEATURE [App::DocumentObjectGroupPython] N_element038  label="N_element : 017"  # scripted group (container) (typed FeaturePython)
  n = 1
  ref = N_element
FEATURE [App::DocumentObjectGroupPython] G4_PYRIDINE  # scripted group (container) (typed FeaturePython)
  Dunit = g/cm3
  Dvalue = 0.9819
  Group = -> [C_element099,H_element091,N_element038]
  conduct = 2
  density = 1
  expand = 3
  formula = G4_PYRIDINE
  name = G4_PYRIDINE
  specific = 4
FEATURE [App::DocumentObjectGroupPython] H_element092  label="H_element : 0.144"  # scripted group (container) (typed FeaturePython)
  n = 0.143711
FEATURE [App::DocumentObjectGroupPython] C_element100  label="C_element : 0.856"  # scripted group (container) (typed FeaturePython)
  n = 0.856289
FEATURE [App::DocumentObjectGroupPython] G4_RUBBER_BUTYL  # scripted group (container) (typed FeaturePython)
  Dunit = g/cm3
  Dvalue = 0.92
  Group = -> [H_element092,C_element100]
  conduct = 2
  density = 1
  expand = 3
  formula = G4_RUBBER_BUTYL
  name = G4_RUBBER_BUTYL
  specific = 4
FEATURE [App::DocumentObjectGroupPython] H_element093  label="H_element : 0.118"  # scripted group (container) (typed FeaturePython)
  n = 0.118371
FEATURE [App::DocumentObjectGroupPython] C_element101  label="C_element : 0.882"  # scripted group (container) (typed FeaturePython)
  n = 0.881629
FEATURE [App::DocumentObjectGroupPython] G4_RUBBER_NATURAL  # scripted group (container) (typed FeaturePython)
  Dunit = g/cm3
  Dvalue = 0.92
  Group = -> [H_element093,C_element101]
  conduct = 2
  density = 1
  expand = 3
  formula = G4_RUBBER_NATURAL
  name = G4_RUBBER_NATURAL
  specific = 4
FEATURE [App::DocumentObjectGroupPython] H_element094  label="H_element : 0.145"  # scripted group (container) (typed FeaturePython)
  n = 0.05692
FEATURE [App::DocumentObjectGroupPython] C_element102  label="C_element : 0.543"  # scripted group (container) (typed FeaturePython)
  n = 0.542646
FEATURE [App::DocumentObjectGroupPython] Cl_element021  label="Cl_element : 0.400"  # scripted group (container) (typed FeaturePython)
  n = 0.400434
FEATURE [App::DocumentObjectGroupPython] G4_RUBBER_NEOPRENE  # scripted group (container) (typed FeaturePython)
  Dunit = g/cm3
  Dvalue = 1.23
  Group = -> [H_element094,C_element102,Cl_element021]
  conduct = 2
  density = 1
  expand = 3
  formula = G4_RUBBER_NEOPRENE
  name = G4_RUBBER_NEOPRENE
  specific = 4
FEATURE [App::DocumentObjectGroupPython] Si_element006  label="Si_element : 1"  # scripted group (container) (typed FeaturePython)
  n = 1
  ref = Si_element
FEATURE [App::DocumentObjectGroupPython] O_element087  label="O_element : 048"  # scripted group (container) (typed FeaturePython)
  n = 2
  ref = O_element
FEATURE [App::DocumentObjectGroupPython] G4_SILICON_DIOXIDE  # scripted group (container) (typed FeaturePython)
  Dunit = g/cm3
  Dvalue = 2.32
  Group = -> [Si_element006,O_element087]
  conduct = 2
  density = 1
  expand = 3
  formula = G4_SILICON_DIOXIDE
  name = G4_SILICON_DIOXIDE
  specific = 4
FEATURE [App::DocumentObjectGroupPython] Ag_element002  label="Ag_element : 1"  # scripted group (container) (typed FeaturePython)
  n = 1
  ref = Ag_element
FEATURE [App::DocumentObjectGroupPython] Br_element005  label="Br_element : 003"  # scripted group (container) (typed FeaturePython)
  n = 1
  ref = Br_element
FEATURE [App::DocumentObjectGroupPython] G4_SILVER_BROMIDE  # scripted group (container) (typed FeaturePython)
  Dunit = g/cm3
  Dvalue = 6.473
  Group = -> [Ag_element002,Br_element005]
  conduct = 2
  density = 1
  expand = 3
  formula = G4_SILVER_BROMIDE
  name = G4_SILVER_BROMIDE
  specific = 4
FEATURE [App::DocumentObjectGroupPython] Ag_element003  label="Ag_element : 002"  # scripted group (container) (typed FeaturePython)
  n = 1
  ref = Ag_element
FEATURE [App::DocumentObjectGroupPython] Cl_element022  label="Cl_element : 011"  # scripted group (container) (typed FeaturePython)
  n = 1
  ref = Cl_element
FEATURE [App::DocumentObjectGroupPython] G4_SILVER_CHLORIDE  # scripted group (container) (typed FeaturePython)
  Dunit = g/cm3
  Dvalue = 5.56
  Group = -> [Ag_element003,Cl_element022]
  conduct = 2
  density = 1
  expand = 3
  formula = G4_SILVER_CHLORIDE
  name = G4_SILVER_CHLORIDE
  specific = 4
FEATURE [App::DocumentObjectGroupPython] Br_element006  label="Br_element : 0.423"  # scripted group (container) (typed FeaturePython)
  n = 0.422895
FEATURE [App::DocumentObjectGroupPython] Ag_element004  label="Ag_element : 0.574"  # scripted group (container) (typed FeaturePython)
  n = 0.573748
FEATURE [App::DocumentObjectGroupPython] I_element007  label="I_element : 0.649"  # scripted group (container) (typed FeaturePython)
  n = 0.003357
FEATURE [App::DocumentObjectGroupPython] G4_SILVER_HALIDES  # scripted group (container) (typed FeaturePython)
  Dunit = g/cm3
  Dvalue = 6.47
  Group = -> [Br_element006,Ag_element004,I_element007]
  conduct = 2
  density = 1
  expand = 3
  formula = G4_SILVER_HALIDES
  name = G4_SILVER_HALIDES
  specific = 4
FEATURE [App::DocumentObjectGroupPython] Ag_element005  label="Ag_element : 003"  # scripted group (container) (typed FeaturePython)
  n = 1
  ref = Ag_element
FEATURE [App::DocumentObjectGroupPython] I_element008  label="I_element : 004"  # scripted group (container) (typed FeaturePython)
  n = 1
  ref = I_element
FEATURE [App::DocumentObjectGroupPython] G4_SILVER_IODIDE  # scripted group (container) (typed FeaturePython)
  Dunit = g/cm3
  Dvalue = 6.01
  Group = -> [Ag_element005,I_element008]
  conduct = 2
  density = 1
  expand = 3
  formula = G4_SILVER_IODIDE
  name = G4_SILVER_IODIDE
  specific = 4
FEATURE [App::DocumentObjectGroupPython] H_element095  label="H_element : 0.100"  # scripted group (container) (typed FeaturePython)
  n = 0.1
FEATURE [App::DocumentObjectGroupPython] C_element103  label="C_element : 0.204"  # scripted group (container) (typed FeaturePython)
  n = 0.204
FEATURE [App::DocumentObjectGroupPython] N_element039  label="N_element : 0.759"  # scripted group (container) (typed FeaturePython)
  n = 0.042
FEATURE [App::DocumentObjectGroupPython] O_element088  label="O_element : 0.645"  # scripted group (container) (typed FeaturePython)
  n = 0.645
FEATURE [App::DocumentObjectGroupPython] Na_element013  label="Na_element : 0.100"  # scripted group (container) (typed FeaturePython)
  n = 0.002
FEATURE [App::DocumentObjectGroupPython] P_element009  label="P_element : 0.107"  # scripted group (container) (typed FeaturePython)
  n = 0.001
FEATURE [App::DocumentObjectGroupPython] S_element020  label="S_element : 0.021"  # scripted group (container) (typed FeaturePython)
  n = 0.002
FEATURE [App::DocumentObjectGroupPython] Cl_element023  label="Cl_element : 0.590"  # scripted group (container) (typed FeaturePython)
  n = 0.003
FEATURE [App::DocumentObjectGroupPython] K_element010  label="K_element : 0.001"  # scripted group (container) (typed FeaturePython)
  n = 0.001
FEATURE [App::DocumentObjectGroupPython] G4_SKIN_ICRP  # scripted group (container) (typed FeaturePython)
  Dunit = g/cm3
  Dvalue = 1.09
  Group = -> [H_element095,C_element103,N_element039,O_element088,Na_element013,P_element009,S_element020,Cl_element023,K_element010]
  conduct = 2
  density = 1
  expand = 3
  formula = G4_SKIN_ICRP
  name = G4_SKIN_ICRP
  specific = 4
FEATURE [App::DocumentObjectGroupPython] Na_element014  label="Na_element : 2"  # scripted group (container) (typed FeaturePython)
  n = 2
  ref = Na_element
FEATURE [App::DocumentObjectGroupPython] C_element104  label="C_element : 058"  # scripted group (container) (typed FeaturePython)
  n = 1
  ref = C_element
FEATURE [App::DocumentObjectGroupPython] O_element089  label="O_element : 049"  # scripted group (container) (typed FeaturePython)
  n = 3
  ref = O_element
FEATURE [App::DocumentObjectGroupPython] G4_SODIUM_CARBONATE  # scripted group (container) (typed FeaturePython)
  Dunit = g/cm3
  Dvalue = 2.532
  Group = -> [Na_element014,C_element104,O_element089]
  conduct = 2
  density = 1
  expand = 3
  formula = G4_SODIUM_CARBONATE
  name = G4_SODIUM_CARBONATE
  specific = 4
FEATURE [App::DocumentObjectGroupPython] Na_element015  label="Na_element : 1"  # scripted group (container) (typed FeaturePython)
  n = 1
  ref = Na_element
FEATURE [App::DocumentObjectGroupPython] I_element009  label="I_element : 005"  # scripted group (container) (typed FeaturePython)
  n = 1
  ref = I_element
FEATURE [App::DocumentObjectGroupPython] G4_SODIUM_IODIDE  # scripted group (container) (typed FeaturePython)
  Dunit = g/cm3
  Dvalue = 3.667
  Group = -> [Na_element015,I_element009]
  conduct = 2
  density = 1
  expand = 3
  formula = G4_SODIUM_IODIDE
  name = G4_SODIUM_IODIDE
  specific = 4
FEATURE [App::DocumentObjectGroupPython] Na_element016  label="Na_element : 003"  # scripted group (container) (typed FeaturePython)
  n = 2
  ref = Na_element
FEATURE [App::DocumentObjectGroupPython] O_element090  label="O_element : 050"  # scripted group (container) (typed FeaturePython)
  n = 1
  ref = O_element
FEATURE [App::DocumentObjectGroupPython] G4_SODIUM_MONOXIDE  # scripted group (container) (typed FeaturePython)
  Dunit = g/cm3
  Dvalue = 2.27
  Group = -> [Na_element016,O_element090]
  conduct = 2
  density = 1
  expand = 3
  formula = G4_SODIUM_MONOXIDE
  name = G4_SODIUM_MONOXIDE
  specific = 4
FEATURE [App::DocumentObjectGroupPython] Na_element017  label="Na_element : 004"  # scripted group (container) (typed FeaturePython)
  n = 1
  ref = Na_element
FEATURE [App::DocumentObjectGroupPython] N_element040  label="N_element : 018"  # scripted group (container) (typed FeaturePython)
  n = 1
  ref = N_element
FEATURE [App::DocumentObjectGroupPython] O_element091  label="O_element : 051"  # scripted group (container) (typed FeaturePython)
  n = 3
  ref = O_element
FEATURE [App::DocumentObjectGroupPython] G4_SODIUM_NITRATE  # scripted group (container) (typed FeaturePython)
  Dunit = g/cm3
  Dvalue = 2.261
  Group = -> [Na_element017,N_element040,O_element091]
  conduct = 2
  density = 1
  expand = 3
  formula = G4_SODIUM_NITRATE
  name = G4_SODIUM_NITRATE
  specific = 4
FEATURE [App::DocumentObjectGroupPython] C_element105  label="C_element : 059"  # scripted group (container) (typed FeaturePython)
  n = 14
  ref = C_element
FEATURE [App::DocumentObjectGroupPython] H_element096  label="H_element : 053"  # scripted group (container) (typed FeaturePython)
  n = 12
  ref = H_element
FEATURE [App::DocumentObjectGroupPython] G4_STILBENE  # scripted group (container) (typed FeaturePython)
  Dunit = g/cm3
  Dvalue = 0.9707
  Group = -> [C_element105,H_element096]
  conduct = 2
  density = 1
  expand = 3
  formula = G4_STILBENE
  name = G4_STILBENE
  specific = 4
FEATURE [App::DocumentObjectGroupPython] C_element106  label="C_element : 12"  # scripted group (container) (typed FeaturePython)
  n = 12
  ref = C_element
FEATURE [App::DocumentObjectGroupPython] H_element097  label="H_element : 22"  # scripted group (container) (typed FeaturePython)
  n = 22
  ref = H_element
FEATURE [App::DocumentObjectGroupPython] O_element092  label="O_element : 11"  # scripted group (container) (typed FeaturePython)
  n = 11
  ref = O_element
FEATURE [App::DocumentObjectGroupPython] G4_SUCROSE  # scripted group (container) (typed FeaturePython)
  Dunit = g/cm3
  Dvalue = 1.5805
  Group = -> [C_element106,H_element097,O_element092]
  conduct = 2
  density = 1
  expand = 3
  formula = G4_SUCROSE
  name = G4_SUCROSE
  specific = 4
FEATURE [App::DocumentObjectGroupPython] C_element107  label="C_element : 18"  # scripted group (container) (typed FeaturePython)
  n = 18
  ref = C_element
FEATURE [App::DocumentObjectGroupPython] H_element098  label="H_element : 054"  # scripted group (container) (typed FeaturePython)
  n = 14
  ref = H_element
FEATURE [App::DocumentObjectGroupPython] G4_TERPHENYL  # scripted group (container) (typed FeaturePython)
  Dunit = g/cm3
  Dvalue = 1.24
  Group = -> [C_element107,H_element098]
  conduct = 2
  density = 1
  expand = 3
  formula = G4_TERPHENYL
  name = G4_TERPHENYL
  specific = 4
FEATURE [App::DocumentObjectGroupPython] H_element099  label="H_element : 0.146"  # scripted group (container) (typed FeaturePython)
  n = 0.106
FEATURE [App::DocumentObjectGroupPython] C_element108  label="C_element : 0.883"  # scripted group (container) (typed FeaturePython)
  n = 0.099
FEATURE [App::DocumentObjectGroupPython] N_element041  label="N_element : 0.020"  # scripted group (container) (typed FeaturePython)
  n = 0.02
FEATURE [App::DocumentObjectGroupPython] O_element093  label="O_element : 0.766"  # scripted group (container) (typed FeaturePython)
  n = 0.766
FEATURE [App::DocumentObjectGroupPython] Na_element018  label="Na_element : 0.101"  # scripted group (container) (typed FeaturePython)
  n = 0.002
FEATURE [App::DocumentObjectGroupPython] P_element010  label="P_element : 0.108"  # scripted group (container) (typed FeaturePython)
  n = 0.001
FEATURE [App::DocumentObjectGroupPython] S_element021  label="S_element : 0.022"  # scripted group (container) (typed FeaturePython)
  n = 0.002
FEATURE [App::DocumentObjectGroupPython] Cl_element024  label="Cl_element : 0.002"  # scripted group (container) (typed FeaturePython)
  n = 0.002
FEATURE [App::DocumentObjectGroupPython] K_element011  label="K_element : 0.017"  # scripted group (container) (typed FeaturePython)
  n = 0.002
FEATURE [App::DocumentObjectGroupPython] G4_TESTIS_ICRP  # scripted group (container) (typed FeaturePython)
  Dunit = g/cm3
  Dvalue = 1.04
  Group = -> [H_element099,C_element108,N_element041,O_element093,Na_element018,P_element010,S_element021,Cl_element024,K_element011]
  conduct = 2
  density = 1
  expand = 3
  formula = G4_TESTIS_ICRP
  name = G4_TESTIS_ICRP
  specific = 4
FEATURE [App::DocumentObjectGroupPython] C_element109  label="C_element : 060"  # scripted group (container) (typed FeaturePython)
  n = 2
  ref = C_element
FEATURE [App::DocumentObjectGroupPython] Cl_element025  label="Cl_element : 012"  # scripted group (container) (typed FeaturePython)
  n = 4
  ref = Cl_element
FEATURE [App::DocumentObjectGroupPython] G4_TETRACHLOROETHYLENE  # scripted group (container) (typed FeaturePython)
  Dunit = g/cm3
  Dvalue = 1.625
  Group = -> [C_element109,Cl_element025]
  conduct = 2
  density = 1
  expand = 3
  formula = G4_TETRACHLOROETHYLENE
  name = G4_TETRACHLOROETHYLENE
  specific = 4
FEATURE [App::DocumentObjectGroupPython] Tl_element001  label="Tl_element : 1"  # scripted group (container) (typed FeaturePython)
  n = 1
  ref = Tl_element
FEATURE [App::DocumentObjectGroupPython] Cl_element026  label="Cl_element : 013"  # scripted group (container) (typed FeaturePython)
  n = 1
  ref = Cl_element
FEATURE [App::DocumentObjectGroupPython] G4_THALLIUM_CHLORIDE  # scripted group (container) (typed FeaturePython)
  Dunit = g/cm3
  Dvalue = 7.004
  Group = -> [Tl_element001,Cl_element026]
  conduct = 2
  density = 1
  expand = 3
  formula = G4_THALLIUM_CHLORIDE
  name = G4_THALLIUM_CHLORIDE
  specific = 4
FEATURE [App::DocumentObjectGroupPython] H_element100  label="H_element : 0.147"  # scripted group (container) (typed FeaturePython)
  n = 0.105
FEATURE [App::DocumentObjectGroupPython] C_element110  label="C_element : 0.256"  # scripted group (container) (typed FeaturePython)
  n = 0.256
FEATURE [App::DocumentObjectGroupPython] N_element042  label="N_element : 0.760"  # scripted group (container) (typed FeaturePython)
  n = 0.027
FEATURE [App::DocumentObjectGroupPython] O_element094  label="O_element : 0.602"  # scripted group (container) (typed FeaturePython)
  n = 0.602
FEATURE [App::DocumentObjectGroupPython] Na_element019  label="Na_element : 0.102"  # scripted group (container) (typed FeaturePython)
  n = 0.001
FEATURE [App::DocumentObjectGroupPython] P_element011  label="P_element : 0.109"  # scripted group (container) (typed FeaturePython)
  n = 0.002
FEATURE [App::DocumentObjectGroupPython] S_element022  label="S_element : 0.023"  # scripted group (container) (typed FeaturePython)
  n = 0.003
FEATURE [App::DocumentObjectGroupPython] Cl_element027  label="Cl_element : 0.591"  # scripted group (container) (typed FeaturePython)
  n = 0.002
FEATURE [App::DocumentObjectGroupPython] K_element012  label="K_element : 0.018"  # scripted group (container) (typed FeaturePython)
  n = 0.002
FEATURE [App::DocumentObjectGroupPython] G4_TISSUE_SOFT_ICRP  # scripted group (container) (typed FeaturePython)
  Dunit = g/cm3
  Dvalue = 1.03
  Group = -> [H_element100,C_element110,N_element042,O_element094,Na_element019,P_element011,S_element022,Cl_element027,K_element012]
  conduct = 2
  density = 1
  expand = 3
  formula = G4_TISSUE_SOFT_ICRP
  name = G4_TISSUE_SOFT_ICRP
  specific = 4
FEATURE [App::DocumentObjectGroupPython] H_element101  label="H_element : 0.148"  # scripted group (container) (typed FeaturePython)
  n = 0.101
FEATURE [App::DocumentObjectGroupPython] C_element111  label="C_element : 0.111"  # scripted group (container) (typed FeaturePython)
  n = 0.111
FEATURE [App::DocumentObjectGroupPython] N_element043  label="N_element : 0.026"  # scripted group (container) (typed FeaturePython)
  n = 0.026
FEATURE [App::DocumentObjectGroupPython] O_element095  label="O_element : 0.762"  # scripted group (container) (typed FeaturePython)
  n = 0.762
FEATURE [App::DocumentObjectGroupPython] G4_TISSUE_SOFT_ICRU_4  label="G4_TISSUE_SOFT_ICRU-4"  # scripted group (container) (typed FeaturePython)
  Dunit = g/cm3
  Dvalue = 1
  Group = -> [H_element101,C_element111,N_element043,O_element095]
  conduct = 2
  density = 1
  expand = 3
  formula = G4_TISSUE_SOFT_ICRU-4
  name = G4_TISSUE_SOFT_ICRU-4
  specific = 4
FEATURE [App::DocumentObjectGroupPython] H_element102  label="H_element : 0.149"  # scripted group (container) (typed FeaturePython)
  n = 0.101869
FEATURE [App::DocumentObjectGroupPython] C_element112  label="C_element : 0.456"  # scripted group (container) (typed FeaturePython)
  n = 0.456179
FEATURE [App::DocumentObjectGroupPython] N_element044  label="N_element : 0.761"  # scripted group (container) (typed FeaturePython)
  n = 0.035172
FEATURE [App::DocumentObjectGroupPython] O_element096  label="O_element : 0.407"  # scripted group (container) (typed FeaturePython)
  n = 0.40678
FEATURE [App::DocumentObjectGroupPython] G4_TISSUE_METHANE  label="G4_TISSUE-METHANE"  # scripted group (container) (typed FeaturePython)
  Dunit = g/cm3
  Dvalue = 0.00106409
  Group = -> [H_element102,C_element112,N_element044,O_element096]
  conduct = 2
  density = 1
  expand = 3
  formula = G4_TISSUE-METHANE
  name = G4_TISSUE-METHANE
  specific = 4
FEATURE [App::DocumentObjectGroupPython] H_element103  label="H_element : 0.103"  # scripted group (container) (typed FeaturePython)
  n = 0.102672
FEATURE [App::DocumentObjectGroupPython] C_element113  label="C_element : 0.569"  # scripted group (container) (typed FeaturePython)
  n = 0.56894
FEATURE [App::DocumentObjectGroupPython] N_element045  label="N_element : 0.762"  # scripted group (container) (typed FeaturePython)
  n = 0.035022
FEATURE [App::DocumentObjectGroupPython] O_element097  label="O_element : 0.293"  # scripted group (container) (typed FeaturePython)
  n = 0.293366
FEATURE [App::DocumentObjectGroupPython] G4_TISSUE_PROPANE  label="G4_TISSUE-PROPANE"  # scripted group (container) (typed FeaturePython)
  Dunit = g/cm3
  Dvalue = 0.00182628
  Group = -> [H_element103,C_element113,N_element045,O_element097]
  conduct = 2
  density = 1
  expand = 3
  formula = G4_TISSUE-PROPANE
  name = G4_TISSUE-PROPANE
  specific = 4
FEATURE [App::DocumentObjectGroupPython] Ti_element003  label="Ti_element : 1"  # scripted group (container) (typed FeaturePython)
  n = 1
  ref = Ti_element
FEATURE [App::DocumentObjectGroupPython] O_element098  label="O_element : 052"  # scripted group (container) (typed FeaturePython)
  n = 2
  ref = O_element
FEATURE [App::DocumentObjectGroupPython] G4_TITANIUM_DIOXIDE  # scripted group (container) (typed FeaturePython)
  Dunit = g/cm3
  Dvalue = 4.26
  Group = -> [Ti_element003,O_element098]
  conduct = 2
  density = 1
  expand = 3
  formula = G4_TITANIUM_DIOXIDE
  name = G4_TITANIUM_DIOXIDE
  specific = 4
FEATURE [App::DocumentObjectGroupPython] C_element114  label="C_element : 061"  # scripted group (container) (typed FeaturePython)
  n = 7
  ref = C_element
FEATURE [App::DocumentObjectGroupPython] H_element104  label="H_element : 055"  # scripted group (container) (typed FeaturePython)
  n = 8
  ref = H_element
FEATURE [App::DocumentObjectGroupPython] G4_TOLUENE  # scripted group (container) (typed FeaturePython)
  Dunit = g/cm3
  Dvalue = 0.8669
  Group = -> [C_element114,H_element104]
  conduct = 2
  density = 1
  expand = 3
  formula = G4_TOLUENE
  name = G4_TOLUENE
  specific = 4
FEATURE [App::DocumentObjectGroupPython] C_element115  label="C_element : 062"  # scripted group (container) (typed FeaturePython)
  n = 2
  ref = C_element
FEATURE [App::DocumentObjectGroupPython] H_element105  label="H_element : 056"  # scripted group (container) (typed FeaturePython)
  n = 1
  ref = H_element
FEATURE [App::DocumentObjectGroupPython] Cl_element028  label="Cl_element : 014"  # scripted group (container) (typed FeaturePython)
  n = 3
  ref = Cl_element
FEATURE [App::DocumentObjectGroupPython] G4_TRICHLOROETHYLENE  # scripted group (container) (typed FeaturePython)
  Dunit = g/cm3
  Dvalue = 1.46
  Group = -> [C_element115,H_element105,Cl_element028]
  conduct = 2
  density = 1
  expand = 3
  formula = G4_TRICHLOROETHYLENE
  name = G4_TRICHLOROETHYLENE
  specific = 4
FEATURE [App::DocumentObjectGroupPython] C_element116  label="C_element : 063"  # scripted group (container) (typed FeaturePython)
  n = 6
  ref = C_element
FEATURE [App::DocumentObjectGroupPython] H_element106  label="H_element : 15"  # scripted group (container) (typed FeaturePython)
  n = 15
  ref = H_element
FEATURE [App::DocumentObjectGroupPython] O_element099  label="O_element : 053"  # scripted group (container) (typed FeaturePython)
  n = 4
  ref = O_element
FEATURE [App::DocumentObjectGroupPython] P_element012  label="P_element : 1"  # scripted group (container) (typed FeaturePython)
  n = 1
  ref = P_element
FEATURE [App::DocumentObjectGroupPython] G4_TRIETHYL_PHOSPHATE  # scripted group (container) (typed FeaturePython)
  Dunit = g/cm3
  Dvalue = 1.07
  Group = -> [C_element116,H_element106,O_element099,P_element012]
  conduct = 2
  density = 1
  expand = 3
  formula = G4_TRIETHYL_PHOSPHATE
  name = G4_TRIETHYL_PHOSPHATE
  specific = 4
FEATURE [App::DocumentObjectGroupPython] W_element003  label="W_element : 003"  # scripted group (container) (typed FeaturePython)
  n = 1
  ref = W_element
FEATURE [App::DocumentObjectGroupPython] F_element017  label="F_element : 6"  # scripted group (container) (typed FeaturePython)
  n = 6
  ref = F_element
FEATURE [App::DocumentObjectGroupPython] G4_TUNGSTEN_HEXAFLUORIDE  # scripted group (container) (typed FeaturePython)
  Dunit = g/cm3
  Dvalue = 2.4
  Group = -> [W_element003,F_element017]
  conduct = 2
  density = 1
  expand = 3
  formula = G4_TUNGSTEN_HEXAFLUORIDE
  name = G4_TUNGSTEN_HEXAFLUORIDE
  specific = 4
FEATURE [App::DocumentObjectGroupPython] U_element001  label="U_element : 1"  # scripted group (container) (typed FeaturePython)
  n = 1
  ref = U_element
FEATURE [App::DocumentObjectGroupPython] C_element117  label="C_element : 064"  # scripted group (container) (typed FeaturePython)
  n = 2
  ref = C_element
FEATURE [App::DocumentObjectGroupPython] G4_URANIUM_DICARBIDE  # scripted group (container) (typed FeaturePython)
  Dunit = g/cm3
  Dvalue = 11.28
  Group = -> [U_element001,C_element117]
  conduct = 2
  density = 1
  expand = 3
  formula = G4_URANIUM_DICARBIDE
  name = G4_URANIUM_DICARBIDE
  specific = 4
FEATURE [App::DocumentObjectGroupPython] U_element002  label="U_element : 002"  # scripted group (container) (typed FeaturePython)
  n = 1
  ref = U_element
FEATURE [App::DocumentObjectGroupPython] C_element118  label="C_element : 065"  # scripted group (container) (typed FeaturePython)
  n = 1
  ref = C_element
FEATURE [App::DocumentObjectGroupPython] G4_URANIUM_MONOCARBIDE  # scripted group (container) (typed FeaturePython)
  Dunit = g/cm3
  Dvalue = 13.63
  Group = -> [U_element002,C_element118]
  conduct = 2
  density = 1
  expand = 3
  formula = G4_URANIUM_MONOCARBIDE
  name = G4_URANIUM_MONOCARBIDE
  specific = 4
FEATURE [App::DocumentObjectGroupPython] U_element003  label="U_element : 003"  # scripted group (container) (typed FeaturePython)
  n = 1
  ref = U_element
FEATURE [App::DocumentObjectGroupPython] O_element100  label="O_element : 054"  # scripted group (container) (typed FeaturePython)
  n = 2
  ref = O_element
FEATURE [App::DocumentObjectGroupPython] G4_URANIUM_OXIDE  # scripted group (container) (typed FeaturePython)
  Dunit = g/cm3
  Dvalue = 10.96
  Group = -> [U_element003,O_element100]
  conduct = 2
  density = 1
  expand = 3
  formula = G4_URANIUM_OXIDE
  name = G4_URANIUM_OXIDE
  specific = 4
FEATURE [App::DocumentObjectGroupPython] C_element119  label="C_element : 066"  # scripted group (container) (typed FeaturePython)
  n = 1
  ref = C_element
FEATURE [App::DocumentObjectGroupPython] H_element107  label="H_element : 057"  # scripted group (container) (typed FeaturePython)
  n = 4
  ref = H_element
FEATURE [App::DocumentObjectGroupPython] N_element046  label="N_element : 019"  # scripted group (container) (typed FeaturePython)
  n = 2
  ref = N_element
FEATURE [App::DocumentObjectGroupPython] O_element101  label="O_element : 055"  # scripted group (container) (typed FeaturePython)
  n = 1
  ref = O_element
FEATURE [App::DocumentObjectGroupPython] G4_UREA  # scripted group (container) (typed FeaturePython)
  Dunit = g/cm3
  Dvalue = 1.323
  Group = -> [C_element119,H_element107,N_element046,O_element101]
  conduct = 2
  density = 1
  expand = 3
  formula = G4_UREA
  name = G4_UREA
  specific = 4
FEATURE [App::DocumentObjectGroupPython] C_element120  label="C_element : 067"  # scripted group (container) (typed FeaturePython)
  n = 5
  ref = C_element
FEATURE [App::DocumentObjectGroupPython] H_element108  label="H_element : 058"  # scripted group (container) (typed FeaturePython)
  n = 11
  ref = H_element
FEATURE [App::DocumentObjectGroupPython] N_element047  label="N_element : 020"  # scripted group (container) (typed FeaturePython)
  n = 1
  ref = N_element
FEATURE [App::DocumentObjectGroupPython] O_element102  label="O_element : 056"  # scripted group (container) (typed FeaturePython)
  n = 2
  ref = O_element
FEATURE [App::DocumentObjectGroupPython] G4_VALINE  # scripted group (container) (typed FeaturePython)
  Dunit = g/cm3
  Dvalue = 1.23
  Group = -> [C_element120,H_element108,N_element047,O_element102]
  conduct = 2
  density = 1
  expand = 3
  formula = G4_VALINE
  name = G4_VALINE
  specific = 4
FEATURE [App::DocumentObjectGroupPython] H_element109  label="H_element : 0.009"  # scripted group (container) (typed FeaturePython)
  n = 0.009417
FEATURE [App::DocumentObjectGroupPython] C_element121  label="C_element : 0.281"  # scripted group (container) (typed FeaturePython)
  n = 0.280555
FEATURE [App::DocumentObjectGroupPython] F_element018  label="F_element : 0.710"  # scripted group (container) (typed FeaturePython)
  n = 0.710028
FEATURE [App::DocumentObjectGroupPython] G4_VITON  # scripted group (container) (typed FeaturePython)
  Dunit = g/cm3
  Dvalue = 1.8
  Group = -> [H_element109,C_element121,F_element018]
  conduct = 2
  density = 1
  expand = 3
  formula = G4_VITON
  name = G4_VITON
  specific = 4
FEATURE [App::DocumentObjectGroupPython] H_element110  label="H_element : 059"  # scripted group (container) (typed FeaturePython)
  n = 2
  ref = H_element
FEATURE [App::DocumentObjectGroupPython] O_element103  label="O_element : 057"  # scripted group (container) (typed FeaturePython)
  n = 1
  ref = O_element
FEATURE [App::DocumentObjectGroupPython] G4_WATER  # scripted group (container) (typed FeaturePython)
  Dunit = g/cm3
  Dvalue = 1
  Group = -> [H_element110,O_element103]
  conduct = 2
  density = 1
  expand = 3
  formula = G4_WATER
  name = G4_WATER
  specific = 4
FEATURE [App::DocumentObjectGroupPython] H_element111  label="H_element : 060"  # scripted group (container) (typed FeaturePython)
  n = 2
  ref = H_element
FEATURE [App::DocumentObjectGroupPython] O_element104  label="O_element : 058"  # scripted group (container) (typed FeaturePython)
  n = 1
  ref = O_element
FEATURE [App::DocumentObjectGroupPython] G4_WATER_VAPOR  # scripted group (container) (typed FeaturePython)
  Dunit = g/cm3
  Dvalue = 0.000756182
  Group = -> [H_element111,O_element104]
  conduct = 2
  density = 1
  expand = 3
  formula = G4_WATER_VAPOR
  name = G4_WATER_VAPOR
  specific = 4
FEATURE [App::DocumentObjectGroupPython] C_element122  label="C_element : 068"  # scripted group (container) (typed FeaturePython)
  n = 8
  ref = C_element
FEATURE [App::DocumentObjectGroupPython] H_element112  label="H_element : 061"  # scripted group (container) (typed FeaturePython)
  n = 10
  ref = H_element
FEATURE [App::DocumentObjectGroupPython] G4_XYLENE  # scripted group (container) (typed FeaturePython)
  Dunit = g/cm3
  Dvalue = 0.87
  Group = -> [C_element122,H_element112]
  conduct = 2
  density = 1
  expand = 3
  formula = G4_XYLENE
  name = G4_XYLENE
  specific = 4
FEATURE [App::DocumentObjectGroupPython] C_element123  label="C_element : 069"  # scripted group (container) (typed FeaturePython)
  n = 1
  ref = C_element
FEATURE [App::DocumentObjectGroupPython] G4_GRAPHITE  # scripted group (container) (typed FeaturePython)
  Dunit = g/cm3
  Dvalue = 2.21
  Group = -> [C_element123]
  conduct = 2
  density = 1
  expand = 3
  formula = G4_GRAPHITE
  name = G4_GRAPHITE
  specific = 4
FEATURE [App::DocumentObjectGroupPython] NIST  # scripted group (container) (typed FeaturePython)
  Group = -> [G4_A_150_TISSUE,G4_ACETONE,G4_ACETYLENE,G4_ADENINE,G4_ADIPOSE_TISSUE_ICRP,G4_AIR,G4_ALANINE,G4_ALUMINUM_OXIDE,G4_AMBER,G4_AMMONIA,G4_ANILINE,G4_ANTHRACENE,G4_B_100_BONE,G4_BAKELITE,G4_BARIUM_FLUORIDE,G4_BARIUM_SULFATE,G4_BENZENE,G4_BERYLLIUM_OXIDE,G4_BGO,G4_BLOOD_ICRP,G4_BONE_COMPACT_ICRU,G4_BONE_CORTICAL_ICRP,G4_BORON_CARBIDE,G4_BORON_OXIDE,G4_BRAIN_ICRP,G4_BUTANE,G4_N_BUTYL_ALCOHOL,G4_C_552,+152 more]
FEATURE [App::DocumentObjectGroupPython] H_element113  label="H_element : 062"  # scripted group (container) (typed FeaturePython)
  n = 1
  ref = H_element
FEATURE [App::DocumentObjectGroupPython] G4_H  # scripted group (container) (typed FeaturePython)
  Dunit = g/cm3
  Dvalue = 8.3748e-05
  Group = -> [H_element113]
  conduct = 2
  density = 1
  expand = 3
  formula = H
  name = G4_H
  specific = 4
FEATURE [App::DocumentObjectGroupPython] He_element001  label="He_element : 1"  # scripted group (container) (typed FeaturePython)
  n = 1
  ref = He_element
FEATURE [App::DocumentObjectGroupPython] G4_He  # scripted group (container) (typed FeaturePython)
  Dunit = g/cm3
  Dvalue = 0.000166322
  Group = -> [He_element001]
  conduct = 2
  density = 1
  expand = 3
  formula = He
  name = G4_He
  specific = 4
FEATURE [App::DocumentObjectGroupPython] Li_element008  label="Li_element : 008"  # scripted group (container) (typed FeaturePython)
  n = 1
  ref = Li_element
FEATURE [App::DocumentObjectGroupPython] G4_Li  # scripted group (container) (typed FeaturePython)
  Dunit = g/cm3
  Dvalue = 0.534
  Group = -> [Li_element008]
  conduct = 2
  density = 1
  expand = 3
  formula = Li
  name = G4_Li
  specific = 4
FEATURE [App::DocumentObjectGroupPython] Be_element002  label="Be_element : 002"  # scripted group (container) (typed FeaturePython)
  n = 1
  ref = Be_element
FEATURE [App::DocumentObjectGroupPython] G4_Be  # scripted group (container) (typed FeaturePython)
  Dunit = g/cm3
  Dvalue = 1.848
  Group = -> [Be_element002]
  conduct = 2
  density = 1
  expand = 3
  formula = Be
  name = G4_Be
  specific = 4
FEATURE [App::DocumentObjectGroupPython] B_element007  label="B_element : 007"  # scripted group (container) (typed FeaturePython)
  n = 1
  ref = B_element
FEATURE [App::DocumentObjectGroupPython] G4_B  # scripted group (container) (typed FeaturePython)
  Dunit = g/cm3
  Dvalue = 2.37
  Group = -> [B_element007]
  conduct = 2
  density = 1
  expand = 3
  formula = B
  name = G4_B
  specific = 4
FEATURE [App::DocumentObjectGroupPython] C_element124  label="C_element : 070"  # scripted group (container) (typed FeaturePython)
  n = 1
  ref = C_element
FEATURE [App::DocumentObjectGroupPython] G4_C  # scripted group (container) (typed FeaturePython)
  Dunit = g/cm3
  Dvalue = 2
  Group = -> [C_element124]
  conduct = 2
  density = 1
  expand = 3
  formula = C
  name = G4_C
  specific = 4
FEATURE [App::DocumentObjectGroupPython] N_element048  label="N_element : 021"  # scripted group (container) (typed FeaturePython)
  n = 1
  ref = N_element
FEATURE [App::DocumentObjectGroupPython] G4_N  # scripted group (container) (typed FeaturePython)
  Dunit = g/cm3
  Dvalue = 0.0011652
  Group = -> [N_element048]
  conduct = 2
  density = 1
  expand = 3
  formula = N
  name = G4_N
  specific = 4
FEATURE [App::DocumentObjectGroupPython] O_element105  label="O_element : 059"  # scripted group (container) (typed FeaturePython)
  n = 1
  ref = O_element
FEATURE [App::DocumentObjectGroupPython] G4_O  # scripted group (container) (typed FeaturePython)
  Dunit = g/cm3
  Dvalue = 0.00133151
  Group = -> [O_element105]
  conduct = 2
  density = 1
  expand = 3
  formula = O
  name = G4_O
  specific = 4
FEATURE [App::DocumentObjectGroupPython] F_element019  label="F_element : 008"  # scripted group (container) (typed FeaturePython)
  n = 1
  ref = F_element
FEATURE [App::DocumentObjectGroupPython] G4_F  # scripted group (container) (typed FeaturePython)
  Dunit = g/cm3
  Dvalue = 0.00158029
  Group = -> [F_element019]
  conduct = 2
  density = 1
  expand = 3
  formula = F
  name = G4_F
  specific = 4
FEATURE [App::DocumentObjectGroupPython] Ne_element001  label="Ne_element : 1"  # scripted group (container) (typed FeaturePython)
  n = 1
  ref = Ne_element
FEATURE [App::DocumentObjectGroupPython] G4_Ne  # scripted group (container) (typed FeaturePython)
  Dunit = g/cm3
  Dvalue = 0.000838505
  Group = -> [Ne_element001]
  conduct = 2
  density = 1
  expand = 3
  formula = Ne
  name = G4_Ne
  specific = 4
FEATURE [App::DocumentObjectGroupPython] Na_element020  label="Na_element : 005"  # scripted group (container) (typed FeaturePython)
  n = 1
  ref = Na_element
FEATURE [App::DocumentObjectGroupPython] G4_Na  # scripted group (container) (typed FeaturePython)
  Dunit = g/cm3
  Dvalue = 0.971
  Group = -> [Na_element020]
  conduct = 2
  density = 1
  expand = 3
  formula = Na
  name = G4_Na
  specific = 4
FEATURE [App::DocumentObjectGroupPython] Mg_element011  label="Mg_element : 005"  # scripted group (container) (typed FeaturePython)
  n = 1
  ref = Mg_element
FEATURE [App::DocumentObjectGroupPython] G4_Mg  # scripted group (container) (typed FeaturePython)
  Dunit = g/cm3
  Dvalue = 1.74
  Group = -> [Mg_element011]
  conduct = 2
  density = 1
  expand = 3
  formula = Mg
  name = G4_Mg
  specific = 4
FEATURE [App::DocumentObjectGroupPython] Al_element004  label="Al_element : 1"  # scripted group (container) (typed FeaturePython)
  n = 1
  ref = Al_element
FEATURE [App::DocumentObjectGroupPython] G4_Al  # scripted group (container) (typed FeaturePython)
  Dunit = g/cm3
  Dvalue = 2.699
  Group = -> [Al_element004]
  conduct = 2
  density = 1
  expand = 3
  formula = Al
  name = G4_Al
  specific = 4
FEATURE [App::DocumentObjectGroupPython] Si_element007  label="Si_element : 002"  # scripted group (container) (typed FeaturePython)
  n = 1
  ref = Si_element
FEATURE [App::DocumentObjectGroupPython] G4_Si  # scripted group (container) (typed FeaturePython)
  Dunit = g/cm3
  Dvalue = 2.33
  Group = -> [Si_element007]
  conduct = 2
  density = 1
  expand = 3
  formula = Si
  name = G4_Si
  specific = 4
FEATURE [App::DocumentObjectGroupPython] P_element013  label="P_element : 002"  # scripted group (container) (typed FeaturePython)
  n = 1
  ref = P_element
FEATURE [App::DocumentObjectGroupPython] G4_P  # scripted group (container) (typed FeaturePython)
  Dunit = g/cm3
  Dvalue = 2.2
  Group = -> [P_element013]
  conduct = 2
  density = 1
  expand = 3
  formula = P
  name = G4_P
  specific = 4
FEATURE [App::DocumentObjectGroupPython] S_element023  label="S_element : 007"  # scripted group (container) (typed FeaturePython)
  n = 1
  ref = S_element
FEATURE [App::DocumentObjectGroupPython] G4_S  # scripted group (container) (typed FeaturePython)
  Dunit = g/cm3
  Dvalue = 2
  Group = -> [S_element023]
  conduct = 2
  density = 1
  expand = 3
  formula = S
  name = G4_S
  specific = 4
FEATURE [App::DocumentObjectGroupPython] Cl_element029  label="Cl_element : 015"  # scripted group (container) (typed FeaturePython)
  n = 1
  ref = Cl_element
FEATURE [App::DocumentObjectGroupPython] G4_Cl  # scripted group (container) (typed FeaturePython)
  Dunit = g/cm3
  Dvalue = 0.00299473
  Group = -> [Cl_element029]
  conduct = 2
  density = 1
  expand = 3
  formula = Cl
  name = G4_Cl
  specific = 4
FEATURE [App::DocumentObjectGroupPython] Ar_element002  label="Ar_element : 1"  # scripted group (container) (typed FeaturePython)
  n = 1
  ref = Ar_element
FEATURE [App::DocumentObjectGroupPython] G4_Ar  # scripted group (container) (typed FeaturePython)
  Dunit = g/cm3
  Dvalue = 0.00166201
  Group = -> [Ar_element002]
  conduct = 2
  density = 1
  expand = 3
  formula = Ar
  name = G4_Ar
  specific = 4
FEATURE [App::DocumentObjectGroupPython] K_element013  label="K_element : 003"  # scripted group (container) (typed FeaturePython)
  n = 1
  ref = K_element
FEATURE [App::DocumentObjectGroupPython] G4_K  # scripted group (container) (typed FeaturePython)
  Dunit = g/cm3
  Dvalue = 0.862
  Group = -> [K_element013]
  conduct = 2
  density = 1
  expand = 3
  formula = K
  name = G4_K
  specific = 4
FEATURE [App::DocumentObjectGroupPython] Ca_element014  label="Ca_element : 007"  # scripted group (container) (typed FeaturePython)
  n = 1
  ref = Ca_element
FEATURE [App::DocumentObjectGroupPython] G4_Ca  # scripted group (container) (typed FeaturePython)
  Dunit = g/cm3
  Dvalue = 1.55
  Group = -> [Ca_element014]
  conduct = 2
  density = 1
  expand = 3
  formula = Ca
  name = G4_Ca
  specific = 4
FEATURE [App::DocumentObjectGroupPython] Sc_element001  label="Sc_element : 1"  # scripted group (container) (typed FeaturePython)
  n = 1
  ref = Sc_element
FEATURE [App::DocumentObjectGroupPython] G4_Sc  # scripted group (container) (typed FeaturePython)
  Dunit = g/cm3
  Dvalue = 2.989
  Group = -> [Sc_element001]
  conduct = 2
  density = 1
  expand = 3
  formula = Sc
  name = G4_Sc
  specific = 4
FEATURE [App::DocumentObjectGroupPython] Ti_element004  label="Ti_element : 002"  # scripted group (container) (typed FeaturePython)
  n = 1
  ref = Ti_element
FEATURE [App::DocumentObjectGroupPython] G4_Ti  # scripted group (container) (typed FeaturePython)
  Dunit = g/cm3
  Dvalue = 4.54
  Group = -> [Ti_element004]
  conduct = 2
  density = 1
  expand = 3
  formula = Ti
  name = G4_Ti
  specific = 4
FEATURE [App::DocumentObjectGroupPython] V_element001  label="V_element : 1"  # scripted group (container) (typed FeaturePython)
  n = 1
  ref = V_element
FEATURE [App::DocumentObjectGroupPython] G4_V  # scripted group (container) (typed FeaturePython)
  Dunit = g/cm3
  Dvalue = 6.11
  Group = -> [V_element001]
  conduct = 2
  density = 1
  expand = 3
  formula = V
  name = G4_V
  specific = 4
FEATURE [App::DocumentObjectGroupPython] Cr_element001  label="Cr_element : 1"  # scripted group (container) (typed FeaturePython)
  n = 1
  ref = Cr_element
FEATURE [App::DocumentObjectGroupPython] G4_Cr  # scripted group (container) (typed FeaturePython)
  Dunit = g/cm3
  Dvalue = 7.18
  Group = -> [Cr_element001]
  conduct = 2
  density = 1
  expand = 3
  formula = Cr
  name = G4_Cr
  specific = 4
FEATURE [App::DocumentObjectGroupPython] Mn_element001  label="Mn_element : 1"  # scripted group (container) (typed FeaturePython)
  n = 1
  ref = Mn_element
FEATURE [App::DocumentObjectGroupPython] G4_Mn  # scripted group (container) (typed FeaturePython)
  Dunit = g/cm3
  Dvalue = 7.44
  Group = -> [Mn_element001]
  conduct = 2
  density = 1
  expand = 3
  formula = Mn
  name = G4_Mn
  specific = 4
FEATURE [App::DocumentObjectGroupPython] Fe_element007  label="Fe_element : 004"  # scripted group (container) (typed FeaturePython)
  n = 1
  ref = Fe_element
FEATURE [App::DocumentObjectGroupPython] G4_Fe  # scripted group (container) (typed FeaturePython)
  Dunit = g/cm3
  Dvalue = 7.874
  Group = -> [Fe_element007]
  conduct = 2
  density = 1
  expand = 3
  formula = Fe
  name = G4_Fe
  specific = 4
FEATURE [App::DocumentObjectGroupPython] Co_element001  label="Co_element : 1"  # scripted group (container) (typed FeaturePython)
  n = 1
  ref = Co_element
FEATURE [App::DocumentObjectGroupPython] G4_Co  # scripted group (container) (typed FeaturePython)
  Dunit = g/cm3
  Dvalue = 8.9
  Group = -> [Co_element001]
  conduct = 2
  density = 1
  expand = 3
  formula = Co
  name = G4_Co
  specific = 4
FEATURE [App::DocumentObjectGroupPython] Ni_element001  label="Ni_element : 1"  # scripted group (container) (typed FeaturePython)
  n = 1
  ref = Ni_element
FEATURE [App::DocumentObjectGroupPython] G4_Ni  # scripted group (container) (typed FeaturePython)
  Dunit = g/cm3
  Dvalue = 8.902
  Group = -> [Ni_element001]
  conduct = 2
  density = 1
  expand = 3
  formula = Ni
  name = G4_Ni
  specific = 4
FEATURE [App::DocumentObjectGroupPython] Cu_element001  label="Cu_element : 1"  # scripted group (container) (typed FeaturePython)
  n = 1
  ref = Cu_element
FEATURE [App::DocumentObjectGroupPython] G4_Cu  # scripted group (container) (typed FeaturePython)
  Dunit = g/cm3
  Dvalue = 8.96
  Group = -> [Cu_element001]
  conduct = 2
  density = 1
  expand = 3
  formula = Cu
  name = G4_Cu
  specific = 4
FEATURE [App::DocumentObjectGroupPython] Zn_element001  label="Zn_element : 1"  # scripted group (container) (typed FeaturePython)
  n = 1
  ref = Zn_element
FEATURE [App::DocumentObjectGroupPython] G4_Zn  # scripted group (container) (typed FeaturePython)
  Dunit = g/cm3
  Dvalue = 7.133
  Group = -> [Zn_element001]
  conduct = 2
  density = 1
  expand = 3
  formula = Zn
  name = G4_Zn
  specific = 4
FEATURE [App::DocumentObjectGroupPython] Ga_element002  label="Ga_element : 002"  # scripted group (container) (typed FeaturePython)
  n = 1
  ref = Ga_element
FEATURE [App::DocumentObjectGroupPython] G4_Ga  # scripted group (container) (typed FeaturePython)
  Dunit = g/cm3
  Dvalue = 5.904
  Group = -> [Ga_element002]
  conduct = 2
  density = 1
  expand = 3
  formula = Ga
  name = G4_Ga
  specific = 4
FEATURE [App::DocumentObjectGroupPython] Ge_element002  label="Ge_element : 1"  # scripted group (container) (typed FeaturePython)
  n = 1
  ref = Ge_element
FEATURE [App::DocumentObjectGroupPython] G4_Ge  # scripted group (container) (typed FeaturePython)
  Dunit = g/cm3
  Dvalue = 5.323
  Group = -> [Ge_element002]
  conduct = 2
  density = 1
  expand = 3
  formula = Ge
  name = G4_Ge
  specific = 4
FEATURE [App::DocumentObjectGroupPython] As_element003  label="As_element : 002"  # scripted group (container) (typed FeaturePython)
  n = 1
  ref = As_element
FEATURE [App::DocumentObjectGroupPython] G4_As  # scripted group (container) (typed FeaturePython)
  Dunit = g/cm3
  Dvalue = 5.73
  Group = -> [As_element003]
  conduct = 2
  density = 1
  expand = 3
  formula = As
  name = G4_As
  specific = 4
FEATURE [App::DocumentObjectGroupPython] Se_element001  label="Se_element : 1"  # scripted group (container) (typed FeaturePython)
  n = 1
  ref = Se_element
FEATURE [App::DocumentObjectGroupPython] G4_Se  # scripted group (container) (typed FeaturePython)
  Dunit = g/cm3
  Dvalue = 4.5
  Group = -> [Se_element001]
  conduct = 2
  density = 1
  expand = 3
  formula = Se
  name = G4_Se
  specific = 4
FEATURE [App::DocumentObjectGroupPython] Br_element007  label="Br_element : 004"  # scripted group (container) (typed FeaturePython)
  n = 1
  ref = Br_element
FEATURE [App::DocumentObjectGroupPython] G4_Br  # scripted group (container) (typed FeaturePython)
  Dunit = g/cm3
  Dvalue = 0.0070721
  Group = -> [Br_element007]
  conduct = 2
  density = 1
  expand = 3
  formula = Br
  name = G4_Br
  specific = 4
FEATURE [App::DocumentObjectGroupPython] Kr_element001  label="Kr_element : 1"  # scripted group (container) (typed FeaturePython)
  n = 1
  ref = Kr_element
FEATURE [App::DocumentObjectGroupPython] G4_Kr  # scripted group (container) (typed FeaturePython)
  Dunit = g/cm3
  Dvalue = 0.00347832
  Group = -> [Kr_element001]
  conduct = 2
  density = 1
  expand = 3
  formula = Kr
  name = G4_Kr
  specific = 4
FEATURE [App::DocumentObjectGroupPython] Rb_element001  label="Rb_element : 1"  # scripted group (container) (typed FeaturePython)
  n = 1
  ref = Rb_element
FEATURE [App::DocumentObjectGroupPython] G4_Rb  # scripted group (container) (typed FeaturePython)
  Dunit = g/cm3
  Dvalue = 1.532
  Group = -> [Rb_element001]
  conduct = 2
  density = 1
  expand = 3
  formula = Rb
  name = G4_Rb
  specific = 4
FEATURE [App::DocumentObjectGroupPython] Sr_element001  label="Sr_element : 1"  # scripted group (container) (typed FeaturePython)
  n = 1
  ref = Sr_element
FEATURE [App::DocumentObjectGroupPython] G4_Sr  # scripted group (container) (typed FeaturePython)
  Dunit = g/cm3
  Dvalue = 2.54
  Group = -> [Sr_element001]
  conduct = 2
  density = 1
  expand = 3
  formula = Sr
  name = G4_Sr
  specific = 4
FEATURE [App::DocumentObjectGroupPython] Y_element001  label="Y_element : 1"  # scripted group (container) (typed FeaturePython)
  n = 1
  ref = Y_element
FEATURE [App::DocumentObjectGroupPython] G4_Y  # scripted group (container) (typed FeaturePython)
  Dunit = g/cm3
  Dvalue = 4.469
  Group = -> [Y_element001]
  conduct = 2
  density = 1
  expand = 3
  formula = Y
  name = G4_Y
  specific = 4
FEATURE [App::DocumentObjectGroupPython] Zr_element001  label="Zr_element : 1"  # scripted group (container) (typed FeaturePython)
  n = 1
  ref = Zr_element
FEATURE [App::DocumentObjectGroupPython] G4_Zr  # scripted group (container) (typed FeaturePython)
  Dunit = g/cm3
  Dvalue = 6.506
  Group = -> [Zr_element001]
  conduct = 2
  density = 1
  expand = 3
  formula = Zr
  name = G4_Zr
  specific = 4
FEATURE [App::DocumentObjectGroupPython] Nb_element001  label="Nb_element : 1"  # scripted group (container) (typed FeaturePython)
  n = 1
  ref = Nb_element
FEATURE [App::DocumentObjectGroupPython] G4_Nb  # scripted group (container) (typed FeaturePython)
  Dunit = g/cm3
  Dvalue = 8.57
  Group = -> [Nb_element001]
  conduct = 2
  density = 1
  expand = 3
  formula = Nb
  name = G4_Nb
  specific = 4
FEATURE [App::DocumentObjectGroupPython] Mo_element001  label="Mo_element : 1"  # scripted group (container) (typed FeaturePython)
  n = 1
  ref = Mo_element
FEATURE [App::DocumentObjectGroupPython] G4_Mo  # scripted group (container) (typed FeaturePython)
  Dunit = g/cm3
  Dvalue = 10.22
  Group = -> [Mo_element001]
  conduct = 2
  density = 1
  expand = 3
  formula = Mo
  name = G4_Mo
  specific = 4
FEATURE [App::DocumentObjectGroupPython] Tc_element001  label="Tc_element : 1"  # scripted group (container) (typed FeaturePython)
  n = 1
  ref = Tc_element
FEATURE [App::DocumentObjectGroupPython] G4_Tc  # scripted group (container) (typed FeaturePython)
  Dunit = g/cm3
  Dvalue = 11.5
  Group = -> [Tc_element001]
  conduct = 2
  density = 1
  expand = 3
  formula = Tc
  name = G4_Tc
  specific = 4
FEATURE [App::DocumentObjectGroupPython] Ru_element001  label="Ru_element : 1"  # scripted group (container) (typed FeaturePython)
  n = 1
  ref = Ru_element
FEATURE [App::DocumentObjectGroupPython] G4_Ru  # scripted group (container) (typed FeaturePython)
  Dunit = g/cm3
  Dvalue = 12.41
  Group = -> [Ru_element001]
  conduct = 2
  density = 1
  expand = 3
  formula = Ru
  name = G4_Ru
  specific = 4
FEATURE [App::DocumentObjectGroupPython] Rh_element001  label="Rh_element : 1"  # scripted group (container) (typed FeaturePython)
  n = 1
  ref = Rh_element
FEATURE [App::DocumentObjectGroupPython] G4_Rh  # scripted group (container) (typed FeaturePython)
  Dunit = g/cm3
  Dvalue = 12.41
  Group = -> [Rh_element001]
  conduct = 2
  density = 1
  expand = 3
  formula = Rh
  name = G4_Rh
  specific = 4
FEATURE [App::DocumentObjectGroupPython] Pd_element001  label="Pd_element : 1"  # scripted group (container) (typed FeaturePython)
  n = 1
  ref = Pd_element
FEATURE [App::DocumentObjectGroupPython] G4_Pd  # scripted group (container) (typed FeaturePython)
  Dunit = g/cm3
  Dvalue = 12.02
  Group = -> [Pd_element001]
  conduct = 2
  density = 1
  expand = 3
  formula = Pd
  name = G4_Pd
  specific = 4
FEATURE [App::DocumentObjectGroupPython] Ag_element006  label="Ag_element : 004"  # scripted group (container) (typed FeaturePython)
  n = 1
  ref = Ag_element
FEATURE [App::DocumentObjectGroupPython] G4_Ag  # scripted group (container) (typed FeaturePython)
  Dunit = g/cm3
  Dvalue = 10.5
  Group = -> [Ag_element006]
  conduct = 2
  density = 1
  expand = 3
  formula = Ag
  name = G4_Ag
  specific = 4
FEATURE [App::DocumentObjectGroupPython] Cd_element003  label="Cd_element : 003"  # scripted group (container) (typed FeaturePython)
  n = 1
  ref = Cd_element
FEATURE [App::DocumentObjectGroupPython] G4_Cd  # scripted group (container) (typed FeaturePython)
  Dunit = g/cm3
  Dvalue = 8.65
  Group = -> [Cd_element003]
  conduct = 2
  density = 1
  expand = 3
  formula = Cd
  name = G4_Cd
  specific = 4
FEATURE [App::DocumentObjectGroupPython] In_element001  label="In_element : 1"  # scripted group (container) (typed FeaturePython)
  n = 1
  ref = In_element
FEATURE [App::DocumentObjectGroupPython] G4_In  # scripted group (container) (typed FeaturePython)
  Dunit = g/cm3
  Dvalue = 7.31
  Group = -> [In_element001]
  conduct = 2
  density = 1
  expand = 3
  formula = In
  name = G4_In
  specific = 4
FEATURE [App::DocumentObjectGroupPython] Sn_element001  label="Sn_element : 1"  # scripted group (container) (typed FeaturePython)
  n = 1
  ref = Sn_element
FEATURE [App::DocumentObjectGroupPython] G4_Sn  # scripted group (container) (typed FeaturePython)
  Dunit = g/cm3
  Dvalue = 7.31
  Group = -> [Sn_element001]
  conduct = 2
  density = 1
  expand = 3
  formula = Sn
  name = G4_Sn
  specific = 4
FEATURE [App::DocumentObjectGroupPython] Sb_element001  label="Sb_element : 1"  # scripted group (container) (typed FeaturePython)
  n = 1
  ref = Sb_element
FEATURE [App::DocumentObjectGroupPython] G4_Sb  # scripted group (container) (typed FeaturePython)
  Dunit = g/cm3
  Dvalue = 6.691
  Group = -> [Sb_element001]
  conduct = 2
  density = 1
  expand = 3
  formula = Sb
  name = G4_Sb
  specific = 4
FEATURE [App::DocumentObjectGroupPython] Te_element002  label="Te_element : 002"  # scripted group (container) (typed FeaturePython)
  n = 1
  ref = Te_element
FEATURE [App::DocumentObjectGroupPython] G4_Te  # scripted group (container) (typed FeaturePython)
  Dunit = g/cm3
  Dvalue = 6.24
  Group = -> [Te_element002]
  conduct = 2
  density = 1
  expand = 3
  formula = Te
  name = G4_Te
  specific = 4
FEATURE [App::DocumentObjectGroupPython] I_element010  label="I_element : 006"  # scripted group (container) (typed FeaturePython)
  n = 1
  ref = I_element
FEATURE [App::DocumentObjectGroupPython] G4_I  # scripted group (container) (typed FeaturePython)
  Dunit = g/cm3
  Dvalue = 4.93
  Group = -> [I_element010]
  conduct = 2
  density = 1
  expand = 3
  formula = I
  name = G4_I
  specific = 4
FEATURE [App::DocumentObjectGroupPython] Xe_element001  label="Xe_element : 1"  # scripted group (container) (typed FeaturePython)
  n = 1
  ref = Xe_element
FEATURE [App::DocumentObjectGroupPython] G4_Xe  # scripted group (container) (typed FeaturePython)
  Dunit = g/cm3
  Dvalue = 0.00548536
  Group = -> [Xe_element001]
  conduct = 2
  density = 1
  expand = 3
  formula = Xe
  name = G4_Xe
  specific = 4
FEATURE [App::DocumentObjectGroupPython] Cs_element003  label="Cs_element : 003"  # scripted group (container) (typed FeaturePython)
  n = 1
  ref = Cs_element
FEATURE [App::DocumentObjectGroupPython] G4_Cs  # scripted group (container) (typed FeaturePython)
  Dunit = g/cm3
  Dvalue = 1.873
  Group = -> [Cs_element003]
  conduct = 2
  density = 1
  expand = 3
  formula = Cs
  name = G4_Cs
  specific = 4
FEATURE [App::DocumentObjectGroupPython] Ba_element003  label="Ba_element : 003"  # scripted group (container) (typed FeaturePython)
  n = 1
  ref = Ba_element
FEATURE [App::DocumentObjectGroupPython] G4_Ba  # scripted group (container) (typed FeaturePython)
  Dunit = g/cm3
  Dvalue = 3.5
  Group = -> [Ba_element003]
  conduct = 2
  density = 1
  expand = 3
  formula = Ba
  name = G4_Ba
  specific = 4
FEATURE [App::DocumentObjectGroupPython] La_element003  label="La_element : 003"  # scripted group (container) (typed FeaturePython)
  n = 1
  ref = La_element
FEATURE [App::DocumentObjectGroupPython] G4_La  # scripted group (container) (typed FeaturePython)
  Dunit = g/cm3
  Dvalue = 6.154
  Group = -> [La_element003]
  conduct = 2
  density = 1
  expand = 3
  formula = La
  name = G4_La
  specific = 4
FEATURE [App::DocumentObjectGroupPython] Ce_element002  label="Ce_element : 1"  # scripted group (container) (typed FeaturePython)
  n = 1
  ref = Ce_element
FEATURE [App::DocumentObjectGroupPython] G4_Ce  # scripted group (container) (typed FeaturePython)
  Dunit = g/cm3
  Dvalue = 6.657
  Group = -> [Ce_element002]
  conduct = 2
  density = 1
  expand = 3
  formula = Ce
  name = G4_Ce
  specific = 4
FEATURE [App::DocumentObjectGroupPython] Pr_element001  label="Pr_element : 1"  # scripted group (container) (typed FeaturePython)
  n = 1
  ref = Pr_element
FEATURE [App::DocumentObjectGroupPython] G4_Pr  # scripted group (container) (typed FeaturePython)
  Dunit = g/cm3
  Dvalue = 6.71
  Group = -> [Pr_element001]
  conduct = 2
  density = 1
  expand = 3
  formula = Pr
  name = G4_Pr
  specific = 4
FEATURE [App::DocumentObjectGroupPython] Nd_element001  label="Nd_element : 1"  # scripted group (container) (typed FeaturePython)
  n = 1
  ref = Nd_element
FEATURE [App::DocumentObjectGroupPython] G4_Nd  # scripted group (container) (typed FeaturePython)
  Dunit = g/cm3
  Dvalue = 6.9
  Group = -> [Nd_element001]
  conduct = 2
  density = 1
  expand = 3
  formula = Nd
  name = G4_Nd
  specific = 4
FEATURE [App::DocumentObjectGroupPython] Pm_element001  label="Pm_element : 1"  # scripted group (container) (typed FeaturePython)
  n = 1
  ref = Pm_element
FEATURE [App::DocumentObjectGroupPython] G4_Pm  # scripted group (container) (typed FeaturePython)
  Dunit = g/cm3
  Dvalue = 7.22
  Group = -> [Pm_element001]
  conduct = 2
  density = 1
  expand = 3
  formula = Pm
  name = G4_Pm
  specific = 4
FEATURE [App::DocumentObjectGroupPython] Sm_element001  label="Sm_element : 1"  # scripted group (container) (typed FeaturePython)
  n = 1
  ref = Sm_element
FEATURE [App::DocumentObjectGroupPython] G4_Sm  # scripted group (container) (typed FeaturePython)
  Dunit = g/cm3
  Dvalue = 7.46
  Group = -> [Sm_element001]
  conduct = 2
  density = 1
  expand = 3
  formula = Sm
  name = G4_Sm
  specific = 4
FEATURE [App::DocumentObjectGroupPython] Eu_element001  label="Eu_element : 1"  # scripted group (container) (typed FeaturePython)
  n = 1
  ref = Eu_element
FEATURE [App::DocumentObjectGroupPython] G4_Eu  # scripted group (container) (typed FeaturePython)
  Dunit = g/cm3
  Dvalue = 5.243
  Group = -> [Eu_element001]
  conduct = 2
  density = 1
  expand = 3
  formula = Eu
  name = G4_Eu
  specific = 4
FEATURE [App::DocumentObjectGroupPython] Gd_element002  label="Gd_element : 1"  # scripted group (container) (typed FeaturePython)
  n = 1
  ref = Gd_element
FEATURE [App::DocumentObjectGroupPython] G4_Gd  # scripted group (container) (typed FeaturePython)
  Dunit = g/cm3
  Dvalue = 7.9004
  Group = -> [Gd_element002]
  conduct = 2
  density = 1
  expand = 3
  formula = Gd
  name = G4_Gd
  specific = 4
FEATURE [App::DocumentObjectGroupPython] Tb_element001  label="Tb_element : 1"  # scripted group (container) (typed FeaturePython)
  n = 1
  ref = Tb_element
FEATURE [App::DocumentObjectGroupPython] G4_Tb  # scripted group (container) (typed FeaturePython)
  Dunit = g/cm3
  Dvalue = 8.229
  Group = -> [Tb_element001]
  conduct = 2
  density = 1
  expand = 3
  formula = Tb
  name = G4_Tb
  specific = 4
FEATURE [App::DocumentObjectGroupPython] Dy_element001  label="Dy_element : 1"  # scripted group (container) (typed FeaturePython)
  n = 1
  ref = Dy_element
FEATURE [App::DocumentObjectGroupPython] G4_Dy  # scripted group (container) (typed FeaturePython)
  Dunit = g/cm3
  Dvalue = 8.55
  Group = -> [Dy_element001]
  conduct = 2
  density = 1
  expand = 3
  formula = Dy
  name = G4_Dy
  specific = 4
FEATURE [App::DocumentObjectGroupPython] Ho_element001  label="Ho_element : 1"  # scripted group (container) (typed FeaturePython)
  n = 1
  ref = Ho_element
FEATURE [App::DocumentObjectGroupPython] G4_Ho  # scripted group (container) (typed FeaturePython)
  Dunit = g/cm3
  Dvalue = 8.795
  Group = -> [Ho_element001]
  conduct = 2
  density = 1
  expand = 3
  formula = Ho
  name = G4_Ho
  specific = 4
FEATURE [App::DocumentObjectGroupPython] Er_element001  label="Er_element : 1"  # scripted group (container) (typed FeaturePython)
  n = 1
  ref = Er_element
FEATURE [App::DocumentObjectGroupPython] G4_Er  # scripted group (container) (typed FeaturePython)
  Dunit = g/cm3
  Dvalue = 9.066
  Group = -> [Er_element001]
  conduct = 2
  density = 1
  expand = 3
  formula = Er
  name = G4_Er
  specific = 4
FEATURE [App::DocumentObjectGroupPython] Tm_element001  label="Tm_element : 1"  # scripted group (container) (typed FeaturePython)
  n = 1
  ref = Tm_element
FEATURE [App::DocumentObjectGroupPython] G4_Tm  # scripted group (container) (typed FeaturePython)
  Dunit = g/cm3
  Dvalue = 9.321
  Group = -> [Tm_element001]
  conduct = 2
  density = 1
  expand = 3
  formula = Tm
  name = G4_Tm
  specific = 4
FEATURE [App::DocumentObjectGroupPython] Yb_element001  label="Yb_element : 1"  # scripted group (container) (typed FeaturePython)
  n = 1
  ref = Yb_element
FEATURE [App::DocumentObjectGroupPython] G4_Yb  # scripted group (container) (typed FeaturePython)
  Dunit = g/cm3
  Dvalue = 6.73
  Group = -> [Yb_element001]
  conduct = 2
  density = 1
  expand = 3
  formula = Yb
  name = G4_Yb
  specific = 4
FEATURE [App::DocumentObjectGroupPython] Lu_element001  label="Lu_element : 1"  # scripted group (container) (typed FeaturePython)
  n = 1
  ref = Lu_element
FEATURE [App::DocumentObjectGroupPython] G4_Lu  # scripted group (container) (typed FeaturePython)
  Dunit = g/cm3
  Dvalue = 9.84
  Group = -> [Lu_element001]
  conduct = 2
  density = 1
  expand = 3
  formula = Lu
  name = G4_Lu
  specific = 4
FEATURE [App::DocumentObjectGroupPython] Hf_element001  label="Hf_element : 1"  # scripted group (container) (typed FeaturePython)
  n = 1
  ref = Hf_element
FEATURE [App::DocumentObjectGroupPython] G4_Hf  # scripted group (container) (typed FeaturePython)
  Dunit = g/cm3
  Dvalue = 13.31
  Group = -> [Hf_element001]
  conduct = 2
  density = 1
  expand = 3
  formula = Hf
  name = G4_Hf
  specific = 4
FEATURE [App::DocumentObjectGroupPython] Ta_element001  label="Ta_element : 1"  # scripted group (container) (typed FeaturePython)
  n = 1
  ref = Ta_element
FEATURE [App::DocumentObjectGroupPython] G4_Ta  # scripted group (container) (typed FeaturePython)
  Dunit = g/cm3
  Dvalue = 16.654
  Group = -> [Ta_element001]
  conduct = 2
  density = 1
  expand = 3
  formula = Ta
  name = G4_Ta
  specific = 4
FEATURE [App::DocumentObjectGroupPython] W_element004  label="W_element : 004"  # scripted group (container) (typed FeaturePython)
  n = 1
  ref = W_element
FEATURE [App::DocumentObjectGroupPython] G4_W  # scripted group (container) (typed FeaturePython)
  Dunit = g/cm3
  Dvalue = 19.3
  Group = -> [W_element004]
  conduct = 2
  density = 1
  expand = 3
  formula = W
  name = G4_W
  specific = 4
FEATURE [App::DocumentObjectGroupPython] Re_element001  label="Re_element : 1"  # scripted group (container) (typed FeaturePython)
  n = 1
  ref = Re_element
FEATURE [App::DocumentObjectGroupPython] G4_Re  # scripted group (container) (typed FeaturePython)
  Dunit = g/cm3
  Dvalue = 21.02
  Group = -> [Re_element001]
  conduct = 2
  density = 1
  expand = 3
  formula = Re
  name = G4_Re
  specific = 4
FEATURE [App::DocumentObjectGroupPython] Os_element001  label="Os_element : 1"  # scripted group (container) (typed FeaturePython)
  n = 1
  ref = Os_element
FEATURE [App::DocumentObjectGroupPython] G4_Os  # scripted group (container) (typed FeaturePython)
  Dunit = g/cm3
  Dvalue = 22.57
  Group = -> [Os_element001]
  conduct = 2
  density = 1
  expand = 3
  formula = Os
  name = G4_Os
  specific = 4
FEATURE [App::DocumentObjectGroupPython] Ir_element001  label="Ir_element : 1"  # scripted group (container) (typed FeaturePython)
  n = 1
  ref = Ir_element
FEATURE [App::DocumentObjectGroupPython] G4_Ir  # scripted group (container) (typed FeaturePython)
  Dunit = g/cm3
  Dvalue = 22.42
  Group = -> [Ir_element001]
  conduct = 2
  density = 1
  expand = 3
  formula = Ir
  name = G4_Ir
  specific = 4
FEATURE [App::DocumentObjectGroupPython] Pt_element001  label="Pt_element : 1"  # scripted group (container) (typed FeaturePython)
  n = 1
  ref = Pt_element
FEATURE [App::DocumentObjectGroupPython] G4_Pt  # scripted group (container) (typed FeaturePython)
  Dunit = g/cm3
  Dvalue = 21.45
  Group = -> [Pt_element001]
  conduct = 2
  density = 1
  expand = 3
  formula = Pt
  name = G4_Pt
  specific = 4
FEATURE [App::DocumentObjectGroupPython] Au_element001  label="Au_element : 1"  # scripted group (container) (typed FeaturePython)
  n = 1
  ref = Au_element
FEATURE [App::DocumentObjectGroupPython] G4_Au  # scripted group (container) (typed FeaturePython)
  Dunit = g/cm3
  Dvalue = 19.32
  Group = -> [Au_element001]
  conduct = 2
  density = 1
  expand = 3
  formula = Au
  name = G4_Au
  specific = 4
FEATURE [App::DocumentObjectGroupPython] Hg_element002  label="Hg_element : 002"  # scripted group (container) (typed FeaturePython)
  n = 1
  ref = Hg_element
FEATURE [App::DocumentObjectGroupPython] G4_Hg  # scripted group (container) (typed FeaturePython)
  Dunit = g/cm3
  Dvalue = 13.546
  Group = -> [Hg_element002]
  conduct = 2
  density = 1
  expand = 3
  formula = Hg
  name = G4_Hg
  specific = 4
FEATURE [App::DocumentObjectGroupPython] Tl_element002  label="Tl_element : 002"  # scripted group (container) (typed FeaturePython)
  n = 1
  ref = Tl_element
FEATURE [App::DocumentObjectGroupPython] G4_Tl  # scripted group (container) (typed FeaturePython)
  Dunit = g/cm3
  Dvalue = 11.72
  Group = -> [Tl_element002]
  conduct = 2
  density = 1
  expand = 3
  formula = Tl
  name = G4_Tl
  specific = 4
FEATURE [App::DocumentObjectGroupPython] Pb_element003  label="Pb_element : 1"  # scripted group (container) (typed FeaturePython)
  n = 1
  ref = Pb_element
FEATURE [App::DocumentObjectGroupPython] G4_Pb  # scripted group (container) (typed FeaturePython)
  Dunit = g/cm3
  Dvalue = 11.35
  Group = -> [Pb_element003]
  conduct = 2
  density = 1
  expand = 3
  formula = Pb
  name = G4_Pb
  specific = 4
FEATURE [App::DocumentObjectGroupPython] Bi_element002  label="Bi_element : 1"  # scripted group (container) (typed FeaturePython)
  n = 1
  ref = Bi_element
FEATURE [App::DocumentObjectGroupPython] G4_Bi  # scripted group (container) (typed FeaturePython)
  Dunit = g/cm3
  Dvalue = 9.747
  Group = -> [Bi_element002]
  conduct = 2
  density = 1
  expand = 3
  formula = Bi
  name = G4_Bi
  specific = 4
FEATURE [App::DocumentObjectGroupPython] Po_element001  label="Po_element : 1"  # scripted group (container) (typed FeaturePython)
  n = 1
  ref = Po_element
FEATURE [App::DocumentObjectGroupPython] G4_Po  # scripted group (container) (typed FeaturePython)
  Dunit = g/cm3
  Dvalue = 9.32
  Group = -> [Po_element001]
  conduct = 2
  density = 1
  expand = 3
  formula = Po
  name = G4_Po
  specific = 4
FEATURE [App::DocumentObjectGroupPython] At_element001  label="At_element : 1"  # scripted group (container) (typed FeaturePython)
  n = 1
  ref = At_element
FEATURE [App::DocumentObjectGroupPython] G4_At  # scripted group (container) (typed FeaturePython)
  Dunit = g/cm3
  Dvalue = 9.32
  Group = -> [At_element001]
  conduct = 2
  density = 1
  expand = 3
  formula = At
  name = G4_At
  specific = 4
FEATURE [App::DocumentObjectGroupPython] Rn_element001  label="Rn_element : 1"  # scripted group (container) (typed FeaturePython)
  n = 1
  ref = Rn_element
FEATURE [App::DocumentObjectGroupPython] G4_Rn  # scripted group (container) (typed FeaturePython)
  Dunit = g/cm3
  Dvalue = 0.00900662
  Group = -> [Rn_element001]
  conduct = 2
  density = 1
  expand = 3
  formula = Rn
  name = G4_Rn
  specific = 4
FEATURE [App::DocumentObjectGroupPython] Fr_element001  label="Fr_element : 1"  # scripted group (container) (typed FeaturePython)
  n = 1
  ref = Fr_element
FEATURE [App::DocumentObjectGroupPython] G4_Fr  # scripted group (container) (typed FeaturePython)
  Dunit = g/cm3
  Dvalue = 1
  Group = -> [Fr_element001]
  conduct = 2
  density = 1
  expand = 3
  formula = Fr
  name = G4_Fr
  specific = 4
FEATURE [App::DocumentObjectGroupPython] Ra_element001  label="Ra_element : 1"  # scripted group (container) (typed FeaturePython)
  n = 1
  ref = Ra_element
FEATURE [App::DocumentObjectGroupPython] G4_Ra  # scripted group (container) (typed FeaturePython)
  Dunit = g/cm3
  Dvalue = 5
  Group = -> [Ra_element001]
  conduct = 2
  density = 1
  expand = 3
  formula = Ra
  name = G4_Ra
  specific = 4
FEATURE [App::DocumentObjectGroupPython] Ac_element001  label="Ac_element : 1"  # scripted group (container) (typed FeaturePython)
  n = 1
  ref = Ac_element
FEATURE [App::DocumentObjectGroupPython] G4_Ac  # scripted group (container) (typed FeaturePython)
  Dunit = g/cm3
  Dvalue = 10.07
  Group = -> [Ac_element001]
  conduct = 2
  density = 1
  expand = 3
  formula = Ac
  name = G4_Ac
  specific = 4
FEATURE [App::DocumentObjectGroupPython] Th_element001  label="Th_element : 1"  # scripted group (container) (typed FeaturePython)
  n = 1
  ref = Th_element
FEATURE [App::DocumentObjectGroupPython] G4_Th  # scripted group (container) (typed FeaturePython)
  Dunit = g/cm3
  Dvalue = 11.72
  Group = -> [Th_element001]
  conduct = 2
  density = 1
  expand = 3
  formula = Th
  name = G4_Th
  specific = 4
FEATURE [App::DocumentObjectGroupPython] Pa_element001  label="Pa_element : 1"  # scripted group (container) (typed FeaturePython)
  n = 1
  ref = Pa_element
FEATURE [App::DocumentObjectGroupPython] G4_Pa  # scripted group (container) (typed FeaturePython)
  Dunit = g/cm3
  Dvalue = 15.37
  Group = -> [Pa_element001]
  conduct = 2
  density = 1
  expand = 3
  formula = Pa
  name = G4_Pa
  specific = 4
FEATURE [App::DocumentObjectGroupPython] U_element004  label="U_element : 004"  # scripted group (container) (typed FeaturePython)
  n = 1
  ref = U_element
FEATURE [App::DocumentObjectGroupPython] G4_U  # scripted group (container) (typed FeaturePython)
  Dunit = g/cm3
  Dvalue = 18.95
  Group = -> [U_element004]
  conduct = 2
  density = 1
  expand = 3
  formula = U
  name = G4_U
  specific = 4
FEATURE [App::DocumentObjectGroupPython] Np_element001  label="Np_element : 1"  # scripted group (container) (typed FeaturePython)
  n = 1
  ref = Np_element
FEATURE [App::DocumentObjectGroupPython] G4_Np  # scripted group (container) (typed FeaturePython)
  Dunit = g/cm3
  Dvalue = 20.25
  Group = -> [Np_element001]
  conduct = 2
  density = 1
  expand = 3
  formula = Np
  name = G4_Np
  specific = 4
FEATURE [App::DocumentObjectGroupPython] Pu_element002  label="Pu_element : 002"  # scripted group (container) (typed FeaturePython)
  n = 1
  ref = Pu_element
FEATURE [App::DocumentObjectGroupPython] G4_Pu  # scripted group (container) (typed FeaturePython)
  Dunit = g/cm3
  Dvalue = 19.84
  Group = -> [Pu_element002]
  conduct = 2
  density = 1
  expand = 3
  formula = Pu
  name = G4_Pu
  specific = 4
FEATURE [App::DocumentObjectGroupPython] Am_element001  label="Am_element : 1"  # scripted group (container) (typed FeaturePython)
  n = 1
  ref = Am_element
FEATURE [App::DocumentObjectGroupPython] G4_Am  # scripted group (container) (typed FeaturePython)
  Dunit = g/cm3
  Dvalue = 13.67
  Group = -> [Am_element001]
  conduct = 2
  density = 1
  expand = 3
  formula = Am
  name = G4_Am
  specific = 4
FEATURE [App::DocumentObjectGroupPython] Cm_element001  label="Cm_element : 1"  # scripted group (container) (typed FeaturePython)
  n = 1
  ref = Cm_element
FEATURE [App::DocumentObjectGroupPython] G4_Cm  # scripted group (container) (typed FeaturePython)
  Dunit = g/cm3
  Dvalue = 13.51
  Group = -> [Cm_element001]
  conduct = 2
  density = 1
  expand = 3
  formula = Cm
  name = G4_Cm
  specific = 4
FEATURE [App::DocumentObjectGroupPython] Bk_element001  label="Bk_element : 1"  # scripted group (container) (typed FeaturePython)
  n = 1
  ref = Bk_element
FEATURE [App::DocumentObjectGroupPython] G4_Bk  # scripted group (container) (typed FeaturePython)
  Dunit = g/cm3
  Dvalue = 14
  Group = -> [Bk_element001]
  conduct = 2
  density = 1
  expand = 3
  formula = Bk
  name = G4_Bk
  specific = 4
FEATURE [App::DocumentObjectGroupPython] Cf_element001  label="Cf_element : 1"  # scripted group (container) (typed FeaturePython)
  n = 1
  ref = Cf_element
FEATURE [App::DocumentObjectGroupPython] G4_Cf  # scripted group (container) (typed FeaturePython)
  Dunit = g/cm3
  Dvalue = 10
  Group = -> [Cf_element001]
  conduct = 2
  density = 1
  expand = 3
  formula = Cf
  name = G4_Cf
  specific = 4
FEATURE [App::DocumentObjectGroupPython] Element  # scripted group (container) (typed FeaturePython)
  Group = -> [G4_H,G4_He,G4_Li,G4_Be,G4_B,G4_C,G4_N,G4_O,G4_F,G4_Ne,G4_Na,G4_Mg,G4_Al,G4_Si,G4_P,G4_S,G4_Cl,G4_Ar,G4_K,G4_Ca,G4_Sc,G4_Ti,G4_V,G4_Cr,G4_Mn,G4_Fe,G4_Co,G4_Ni,G4_Cu,G4_Zn,G4_Ga,G4_Ge,G4_As,G4_Se,G4_Br,G4_Kr,G4_Rb,G4_Sr,G4_Y,G4_Zr,G4_Nb,G4_Mo,G4_Tc,G4_Ru,G4_Rh,G4_Pd,G4_Ag,G4_Cd,G4_In,G4_Sn,G4_Sb,G4_Te,G4_I,G4_Xe,G4_Cs,G4_Ba,G4_La,G4_Ce,G4_Pr,G4_Nd,G4_Pm,G4_Sm,G4_Eu,G4_Gd,G4_Tb,G4_Dy,G4_Ho,G4_Er,+30 more]
FEATURE [App::DocumentObjectGroupPython] H_element114  label="H_element : 063"  # scripted group (container) (typed FeaturePython)
  n = 2
  ref = H_element
FEATURE [App::DocumentObjectGroupPython] G4_lH2  # scripted group (container) (typed FeaturePython)
  Dunit = g/cm3
  Dvalue = 0.0708
  Group = -> [H_element114]
  conduct = 2
  density = 1
  expand = 3
  formula = G4_lH2
  name = G4_lH2
  specific = 4
FEATURE [App::DocumentObjectGroupPython] N_element049  label="N_element : 022"  # scripted group (container) (typed FeaturePython)
  n = 2
  ref = N_element
FEATURE [App::DocumentObjectGroupPython] G4_lN2  # scripted group (container) (typed FeaturePython)
  Dunit = g/cm3
  Dvalue = 0.807
  Group = -> [N_element049]
  conduct = 2
  density = 1
  expand = 3
  formula = G4_lN2
  name = G4_lN2
  specific = 4
FEATURE [App::DocumentObjectGroupPython] O_element106  label="O_element : 060"  # scripted group (container) (typed FeaturePython)
  n = 2
  ref = O_element
FEATURE [App::DocumentObjectGroupPython] G4_lO2  # scripted group (container) (typed FeaturePython)
  Dunit = g/cm3
  Dvalue = 1.141
  Group = -> [O_element106]
  conduct = 2
  density = 1
  expand = 3
  formula = G4_lO2
  name = G4_lO2
  specific = 4
FEATURE [App::DocumentObjectGroupPython] Ar_element003  label="Ar_element : 002"  # scripted group (container) (typed FeaturePython)
  n = 1
  ref = Ar_element
FEATURE [App::DocumentObjectGroupPython] G4_lAr  # scripted group (container) (typed FeaturePython)
  Dunit = g/cm3
  Dvalue = 1.396
  Group = -> [Ar_element003]
  conduct = 2
  density = 1
  expand = 3
  formula = G4_lAr
  name = G4_lAr
  specific = 4
FEATURE [App::DocumentObjectGroupPython] Br_element008  label="Br_element : 005"  # scripted group (container) (typed FeaturePython)
  n = 1
  ref = Br_element
FEATURE [App::DocumentObjectGroupPython] G4_lBr  # scripted group (container) (typed FeaturePython)
  Dunit = g/cm3
  Dvalue = 3.1028
  Group = -> [Br_element008]
  conduct = 2
  density = 1
  expand = 3
  formula = G4_lBr
  name = G4_lBr
  specific = 4
FEATURE [App::DocumentObjectGroupPython] Kr_element002  label="Kr_element : 002"  # scripted group (container) (typed FeaturePython)
  n = 1
  ref = Kr_element
FEATURE [App::DocumentObjectGroupPython] G4_lKr  # scripted group (container) (typed FeaturePython)
  Dunit = g/cm3
  Dvalue = 2.418
  Group = -> [Kr_element002]
  conduct = 2
  density = 1
  expand = 3
  formula = G4_lKr
  name = G4_lKr
  specific = 4
FEATURE [App::DocumentObjectGroupPython] Xe_element002  label="Xe_element : 002"  # scripted group (container) (typed FeaturePython)
  n = 1
  ref = Xe_element
FEATURE [App::DocumentObjectGroupPython] G4_lXe  # scripted group (container) (typed FeaturePython)
  Dunit = g/cm3
  Dvalue = 2.953
  Group = -> [Xe_element002]
  conduct = 2
  density = 1
  expand = 3
  formula = G4_lXe
  name = G4_lXe
  specific = 4
FEATURE [App::DocumentObjectGroupPython] O_element107  label="O_element : 061"  # scripted group (container) (typed FeaturePython)
  n = 4
  ref = O_element
FEATURE [App::DocumentObjectGroupPython] Pb_element004  label="Pb_element : 002"  # scripted group (container) (typed FeaturePython)
  n = 1
  ref = Pb_element
FEATURE [App::DocumentObjectGroupPython] W_element005  label="W_element : 005"  # scripted group (container) (typed FeaturePython)
  n = 1
  ref = W_element
FEATURE [App::DocumentObjectGroupPython] G4_PbWO4  # scripted group (container) (typed FeaturePython)
  Dunit = g/cm3
  Dvalue = 8.28
  Group = -> [O_element107,Pb_element004,W_element005]
  conduct = 2
  density = 1
  expand = 3
  formula = G4_PbWO4
  name = G4_PbWO4
  specific = 4
FEATURE [App::DocumentObjectGroupPython] H_element115  label="H_element : 064"  # scripted group (container) (typed FeaturePython)
  n = 1
  ref = H_element
FEATURE [App::DocumentObjectGroupPython] G4_Galactic  # scripted group (container) (typed FeaturePython)
  Dunit = g/cm3
  Dvalue = 0
  Group = -> [H_element115]
  conduct = 2
  density = 1
  expand = 3
  formula = G4_Galactic
  name = G4_Galactic
  specific = 4
FEATURE [App::DocumentObjectGroupPython] C_element125  label="C_element : 071"  # scripted group (container) (typed FeaturePython)
  n = 1
  ref = C_element
FEATURE [App::DocumentObjectGroupPython] G4_GRAPHITE_POROUS  # scripted group (container) (typed FeaturePython)
  Dunit = g/cm3
  Dvalue = 1.7
  Group = -> [C_element125]
  conduct = 2
  density = 1
  expand = 3
  formula = G4_GRAPHITE_POROUS
  name = G4_GRAPHITE_POROUS
  specific = 4
FEATURE [App::DocumentObjectGroupPython] H_element116  label="H_element : 0.150"  # scripted group (container) (typed FeaturePython)
  n = 0.080538
FEATURE [App::DocumentObjectGroupPython] C_element126  label="C_element : 0.600"  # scripted group (container) (typed FeaturePython)
  n = 0.599848
FEATURE [App::DocumentObjectGroupPython] O_element108  label="O_element : 0.320"  # scripted group (container) (typed FeaturePython)
  n = 0.319614
FEATURE [App::DocumentObjectGroupPython] G4_LUCITE  # scripted group (container) (typed FeaturePython)
  Dunit = g/cm3
  Dvalue = 1.19
  Group = -> [H_element116,C_element126,O_element108]
  conduct = 2
  density = 1
  expand = 3
  formula = G4_LUCITE
  name = G4_LUCITE
  specific = 4
FEATURE [App::DocumentObjectGroupPython] Cu_element002  label="Cu_element : 62"  # scripted group (container) (typed FeaturePython)
  n = 62
  ref = Cu_element
FEATURE [App::DocumentObjectGroupPython] Zn_element002  label="Zn_element : 35"  # scripted group (container) (typed FeaturePython)
  n = 35
  ref = Zn_element
FEATURE [App::DocumentObjectGroupPython] Pb_element005  label="Pb_element : 3"  # scripted group (container) (typed FeaturePython)
  n = 3
  ref = Pb_element
FEATURE [App::DocumentObjectGroupPython] G4_BRASS  # scripted group (container) (typed FeaturePython)
  Dunit = g/cm3
  Dvalue = 8.52
  Group = -> [Cu_element002,Zn_element002,Pb_element005]
  conduct = 2
  density = 1
  expand = 3
  formula = G4_BRASS
  name = G4_BRASS
  specific = 4
FEATURE [App::DocumentObjectGroupPython] Cu_element003  label="Cu_element : 89"  # scripted group (container) (typed FeaturePython)
  n = 89
  ref = Cu_element
FEATURE [App::DocumentObjectGroupPython] Zn_element003  label="Zn_element : 9"  # scripted group (container) (typed FeaturePython)
  n = 9
  ref = Zn_element
FEATURE [App::DocumentObjectGroupPython] Pb_element006  label="Pb_element : 2"  # scripted group (container) (typed FeaturePython)
  n = 2
  ref = Pb_element
FEATURE [App::DocumentObjectGroupPython] G4_BRONZE  # scripted group (container) (typed FeaturePython)
  Dunit = g/cm3
  Dvalue = 8.82
  Group = -> [Cu_element003,Zn_element003,Pb_element006]
  conduct = 2
  density = 1
  expand = 3
  formula = G4_BRONZE
  name = G4_BRONZE
  specific = 4
FEATURE [App::DocumentObjectGroupPython] Fe_element008  label="Fe_element : 74"  # scripted group (container) (typed FeaturePython)
  n = 74
  ref = Fe_element
FEATURE [App::DocumentObjectGroupPython] Cr_element002  label="Cr_element : 18"  # scripted group (container) (typed FeaturePython)
  n = 18
  ref = Cr_element
FEATURE [App::DocumentObjectGroupPython] Ni_element002  label="Ni_element : 8"  # scripted group (container) (typed FeaturePython)
  n = 8
  ref = Ni_element
FEATURE [App::DocumentObjectGroupPython] G4_STAINLESS_STEEL  label="G4_STAINLESS-STEEL"  # scripted group (container) (typed FeaturePython)
  Dunit = g/cm3
  Dvalue = 8
  Group = -> [Fe_element008,Cr_element002,Ni_element002]
  conduct = 2
  density = 1
  expand = 3
  formula = G4_STAINLESS-STEEL
  name = G4_STAINLESS-STEEL
  specific = 4
FEATURE [App::DocumentObjectGroupPython] H_element117  label="H_element : 065"  # scripted group (container) (typed FeaturePython)
  n = 18
  ref = H_element
FEATURE [App::DocumentObjectGroupPython] C_element127  label="C_element : 072"  # scripted group (container) (typed FeaturePython)
  n = 12
  ref = C_element
FEATURE [App::DocumentObjectGroupPython] O_element109  label="O_element : 062"  # scripted group (container) (typed FeaturePython)
  n = 7
  ref = O_element
FEATURE [App::DocumentObjectGroupPython] G4_CR39  # scripted group (container) (typed FeaturePython)
  Dunit = g/cm3
  Dvalue = 1.32
  Group = -> [H_element117,C_element127,O_element109]
  conduct = 2
  density = 1
  expand = 3
  formula = G4_CR39
  name = G4_CR39
  specific = 4
FEATURE [App::DocumentObjectGroupPython] H_element118  label="H_element : 38"  # scripted group (container) (typed FeaturePython)
  n = 38
  ref = H_element
FEATURE [App::DocumentObjectGroupPython] C_element128  label="C_element : 073"  # scripted group (container) (typed FeaturePython)
  n = 18
  ref = C_element
FEATURE [App::DocumentObjectGroupPython] O_element110  label="O_element : 063"  # scripted group (container) (typed FeaturePython)
  n = 1
  ref = O_element
FEATURE [App::DocumentObjectGroupPython] G4_OCTADECANOL  # scripted group (container) (typed FeaturePython)
  Dunit = g/cm3
  Dvalue = 0.812
  Group = -> [H_element118,C_element128,O_element110]
  conduct = 2
  density = 1
  expand = 3
  formula = G4_OCTADECANOL
  name = G4_OCTADECANOL
  specific = 4
FEATURE [App::DocumentObjectGroupPython] HEP  # scripted group (container) (typed FeaturePython)
  Group = -> [G4_lH2,G4_lN2,G4_lO2,G4_lAr,G4_lBr,G4_lKr,G4_lXe,G4_PbWO4,G4_Galactic,G4_GRAPHITE_POROUS,G4_LUCITE,G4_BRASS,G4_BRONZE,G4_STAINLESS_STEEL,G4_CR39,G4_OCTADECANOL]
FEATURE [App::DocumentObjectGroupPython] C_element129  label="C_element : 074"  # scripted group (container) (typed FeaturePython)
  n = 14
  ref = C_element
FEATURE [App::DocumentObjectGroupPython] H_element119  label="H_element : 066"  # scripted group (container) (typed FeaturePython)
  n = 10
  ref = H_element
FEATURE [App::DocumentObjectGroupPython] O_element111  label="O_element : 064"  # scripted group (container) (typed FeaturePython)
  n = 2
  ref = O_element
FEATURE [App::DocumentObjectGroupPython] N_element050  label="N_element : 023"  # scripted group (container) (typed FeaturePython)
  n = 2
  ref = N_element
FEATURE [App::DocumentObjectGroupPython] G4_KEVLAR  # scripted group (container) (typed FeaturePython)
  Dunit = g/cm3
  Dvalue = 1.44
  Group = -> [C_element129,H_element119,O_element111,N_element050]
  conduct = 2
  density = 1
  expand = 3
  formula = G4_KEVLAR
  name = G4_KEVLAR
  specific = 4
FEATURE [App::DocumentObjectGroupPython] C_element130  label="C_element : 075"  # scripted group (container) (typed FeaturePython)
  n = 10
  ref = C_element
FEATURE [App::DocumentObjectGroupPython] H_element120  label="H_element : 067"  # scripted group (container) (typed FeaturePython)
  n = 8
  ref = H_element
FEATURE [App::DocumentObjectGroupPython] O_element112  label="O_element : 065"  # scripted group (container) (typed FeaturePython)
  n = 4
  ref = O_element
FEATURE [App::DocumentObjectGroupPython] G4_DACRON  # scripted group (container) (typed FeaturePython)
  Dunit = g/cm3
  Dvalue = 1.4
  Group = -> [C_element130,H_element120,O_element112]
  conduct = 2
  density = 1
  expand = 3
  formula = G4_DACRON
  name = G4_DACRON
  specific = 4
FEATURE [App::DocumentObjectGroupPython] C_element131  label="C_element : 076"  # scripted group (container) (typed FeaturePython)
  n = 4
  ref = C_element
FEATURE [App::DocumentObjectGroupPython] H_element121  label="H_element : 068"  # scripted group (container) (typed FeaturePython)
  n = 5
  ref = H_element
FEATURE [App::DocumentObjectGroupPython] Cl_element030  label="Cl_element : 016"  # scripted group (container) (typed FeaturePython)
  n = 1
  ref = Cl_element
FEATURE [App::DocumentObjectGroupPython] G4_NEOPRENE  # scripted group (container) (typed FeaturePython)
  Dunit = g/cm3
  Dvalue = 1.23
  Group = -> [C_element131,H_element121,Cl_element030]
  conduct = 2
  density = 1
  expand = 3
  formula = G4_NEOPRENE
  name = G4_NEOPRENE
  specific = 4
FEATURE [App::DocumentObjectGroupPython] Space  # scripted group (container) (typed FeaturePython)
  Group = -> [G4_KEVLAR,G4_DACRON,G4_NEOPRENE]
FEATURE [App::DocumentObjectGroupPython] H_element122  label="H_element : 069"  # scripted group (container) (typed FeaturePython)
  n = 5
  ref = H_element
FEATURE [App::DocumentObjectGroupPython] C_element132  label="C_element : 077"  # scripted group (container) (typed FeaturePython)
  n = 4
  ref = C_element
FEATURE [App::DocumentObjectGroupPython] N_element051  label="N_element : 3"  # scripted group (container) (typed FeaturePython)
  n = 3
  ref = N_element
FEATURE [App::DocumentObjectGroupPython] O_element113  label="O_element : 066"  # scripted group (container) (typed FeaturePython)
  n = 1
  ref = O_element
FEATURE [App::DocumentObjectGroupPython] G4_CYTOSINE  # scripted group (container) (typed FeaturePython)
  Dunit = g/cm3
  Dvalue = 1.55
  Group = -> [H_element122,C_element132,N_element051,O_element113]
  conduct = 2
  density = 1
  expand = 3
  formula = G4_CYTOSINE
  name = G4_CYTOSINE
  specific = 4
FEATURE [App::DocumentObjectGroupPython] H_element123  label="H_element : 070"  # scripted group (container) (typed FeaturePython)
  n = 6
  ref = H_element
FEATURE [App::DocumentObjectGroupPython] C_element133  label="C_element : 078"  # scripted group (container) (typed FeaturePython)
  n = 5
  ref = C_element
FEATURE [App::DocumentObjectGroupPython] N_element052  label="N_element : 024"  # scripted group (container) (typed FeaturePython)
  n = 2
  ref = N_element
FEATURE [App::DocumentObjectGroupPython] O_element114  label="O_element : 067"  # scripted group (container) (typed FeaturePython)
  n = 2
  ref = O_element
FEATURE [App::DocumentObjectGroupPython] G4_THYMINE  # scripted group (container) (typed FeaturePython)
  Dunit = g/cm3
  Dvalue = 1.23
  Group = -> [H_element123,C_element133,N_element052,O_element114]
  conduct = 2
  density = 1
  expand = 3
  formula = G4_THYMINE
  name = G4_THYMINE
  specific = 4
FEATURE [App::DocumentObjectGroupPython] H_element124  label="H_element : 071"  # scripted group (container) (typed FeaturePython)
  n = 4
  ref = H_element
FEATURE [App::DocumentObjectGroupPython] C_element134  label="C_element : 079"  # scripted group (container) (typed FeaturePython)
  n = 4
  ref = C_element
FEATURE [App::DocumentObjectGroupPython] N_element053  label="N_element : 025"  # scripted group (container) (typed FeaturePython)
  n = 2
  ref = N_element
FEATURE [App::DocumentObjectGroupPython] O_element115  label="O_element : 068"  # scripted group (container) (typed FeaturePython)
  n = 2
  ref = O_element
FEATURE [App::DocumentObjectGroupPython] G4_URACIL  # scripted group (container) (typed FeaturePython)
  Dunit = g/cm3
  Dvalue = 1.32
  Group = -> [H_element124,C_element134,N_element053,O_element115]
  conduct = 2
  density = 1
  expand = 3
  formula = G4_URACIL
  name = G4_URACIL
  specific = 4
FEATURE [App::DocumentObjectGroupPython] H_element125  label="H_element : 072"  # scripted group (container) (typed FeaturePython)
  n = 4
  ref = H_element
FEATURE [App::DocumentObjectGroupPython] C_element135  label="C_element : 080"  # scripted group (container) (typed FeaturePython)
  n = 5
  ref = C_element
FEATURE [App::DocumentObjectGroupPython] N_element054  label="N_element : 026"  # scripted group (container) (typed FeaturePython)
  n = 5
  ref = N_element
FEATURE [App::DocumentObjectGroupPython] G4_DNA_ADENINE  # scripted group (container) (typed FeaturePython)
  Dunit = g/cm3
  Dvalue = 1
  Group = -> [H_element125,C_element135,N_element054]
  conduct = 2
  density = 1
  expand = 3
  formula = G4_DNA_ADENINE
  name = G4_DNA_ADENINE
  specific = 4
FEATURE [App::DocumentObjectGroupPython] H_element126  label="H_element : 073"  # scripted group (container) (typed FeaturePython)
  n = 4
  ref = H_element
FEATURE [App::DocumentObjectGroupPython] C_element136  label="C_element : 081"  # scripted group (container) (typed FeaturePython)
  n = 5
  ref = C_element
FEATURE [App::DocumentObjectGroupPython] N_element055  label="N_element : 027"  # scripted group (container) (typed FeaturePython)
  n = 5
  ref = N_element
FEATURE [App::DocumentObjectGroupPython] O_element116  label="O_element : 069"  # scripted group (container) (typed FeaturePython)
  n = 1
  ref = O_element
FEATURE [App::DocumentObjectGroupPython] G4_DNA_GUANINE  # scripted group (container) (typed FeaturePython)
  Dunit = g/cm3
  Dvalue = 1
  Group = -> [H_element126,C_element136,N_element055,O_element116]
  conduct = 2
  density = 1
  expand = 3
  formula = G4_DNA_GUANINE
  name = G4_DNA_GUANINE
  specific = 4
FEATURE [App::DocumentObjectGroupPython] H_element127  label="H_element : 074"  # scripted group (container) (typed FeaturePython)
  n = 4
  ref = H_element
FEATURE [App::DocumentObjectGroupPython] C_element137  label="C_element : 082"  # scripted group (container) (typed FeaturePython)
  n = 4
  ref = C_element
FEATURE [App::DocumentObjectGroupPython] N_element056  label="N_element : 028"  # scripted group (container) (typed FeaturePython)
  n = 3
  ref = N_element
FEATURE [App::DocumentObjectGroupPython] O_element117  label="O_element : 070"  # scripted group (container) (typed FeaturePython)
  n = 1
  ref = O_element
FEATURE [App::DocumentObjectGroupPython] G4_DNA_CYTOSINE  # scripted group (container) (typed FeaturePython)
  Dunit = g/cm3
  Dvalue = 1
  Group = -> [H_element127,C_element137,N_element056,O_element117]
  conduct = 2
  density = 1
  expand = 3
  formula = G4_DNA_CYTOSINE
  name = G4_DNA_CYTOSINE
  specific = 4
FEATURE [App::DocumentObjectGroupPython] H_element128  label="H_element : 075"  # scripted group (container) (typed FeaturePython)
  n = 5
  ref = H_element
FEATURE [App::DocumentObjectGroupPython] C_element138  label="C_element : 083"  # scripted group (container) (typed FeaturePython)
  n = 5
  ref = C_element
FEATURE [App::DocumentObjectGroupPython] N_element057  label="N_element : 029"  # scripted group (container) (typed FeaturePython)
  n = 2
  ref = N_element
FEATURE [App::DocumentObjectGroupPython] O_element118  label="O_element : 071"  # scripted group (container) (typed FeaturePython)
  n = 2
  ref = O_element
FEATURE [App::DocumentObjectGroupPython] G4_DNA_THYMINE  # scripted group (container) (typed FeaturePython)
  Dunit = g/cm3
  Dvalue = 1
  Group = -> [H_element128,C_element138,N_element057,O_element118]
  conduct = 2
  density = 1
  expand = 3
  formula = G4_DNA_THYMINE
  name = G4_DNA_THYMINE
  specific = 4
FEATURE [App::DocumentObjectGroupPython] H_element129  label="H_element : 076"  # scripted group (container) (typed FeaturePython)
  n = 3
  ref = H_element
FEATURE [App::DocumentObjectGroupPython] C_element139  label="C_element : 084"  # scripted group (container) (typed FeaturePython)
  n = 4
  ref = C_element
FEATURE [App::DocumentObjectGroupPython] N_element058  label="N_element : 030"  # scripted group (container) (typed FeaturePython)
  n = 2
  ref = N_element
FEATURE [App::DocumentObjectGroupPython] O_element119  label="O_element : 072"  # scripted group (container) (typed FeaturePython)
  n = 2
  ref = O_element
FEATURE [App::DocumentObjectGroupPython] G4_DNA_URACIL  # scripted group (container) (typed FeaturePython)
  Dunit = g/cm3
  Dvalue = 1
  Group = -> [H_element129,C_element139,N_element058,O_element119]
  conduct = 2
  density = 1
  expand = 3
  formula = G4_DNA_URACIL
  name = G4_DNA_URACIL
  specific = 4
FEATURE [App::DocumentObjectGroupPython] H_element130  label="H_element : 077"  # scripted group (container) (typed FeaturePython)
  n = 10
  ref = H_element
FEATURE [App::DocumentObjectGroupPython] C_element140  label="C_element : 085"  # scripted group (container) (typed FeaturePython)
  n = 10
  ref = C_element
FEATURE [App::DocumentObjectGroupPython] N_element059  label="N_element : 031"  # scripted group (container) (typed FeaturePython)
  n = 5
  ref = N_element
FEATURE [App::DocumentObjectGroupPython] O_element120  label="O_element : 073"  # scripted group (container) (typed FeaturePython)
  n = 4
  ref = O_element
FEATURE [App::DocumentObjectGroupPython] G4_DNA_ADENOSINE  # scripted group (container) (typed FeaturePython)
  Dunit = g/cm3
  Dvalue = 1
  Group = -> [H_element130,C_element140,N_element059,O_element120]
  conduct = 2
  density = 1
  expand = 3
  formula = G4_DNA_ADENOSINE
  name = G4_DNA_ADENOSINE
  specific = 4
FEATURE [App::DocumentObjectGroupPython] H_element131  label="H_element : 078"  # scripted group (container) (typed FeaturePython)
  n = 10
  ref = H_element
FEATURE [App::DocumentObjectGroupPython] C_element141  label="C_element : 086"  # scripted group (container) (typed FeaturePython)
  n = 10
  ref = C_element
FEATURE [App::DocumentObjectGroupPython] N_element060  label="N_element : 032"  # scripted group (container) (typed FeaturePython)
  n = 5
  ref = N_element
FEATURE [App::DocumentObjectGroupPython] O_element121  label="O_element : 074"  # scripted group (container) (typed FeaturePython)
  n = 5
  ref = O_element
FEATURE [App::DocumentObjectGroupPython] G4_DNA_GUANOSINE  # scripted group (container) (typed FeaturePython)
  Dunit = g/cm3
  Dvalue = 1
  Group = -> [H_element131,C_element141,N_element060,O_element121]
  conduct = 2
  density = 1
  expand = 3
  formula = G4_DNA_GUANOSINE
  name = G4_DNA_GUANOSINE
  specific = 4
FEATURE [App::DocumentObjectGroupPython] H_element132  label="H_element : 079"  # scripted group (container) (typed FeaturePython)
  n = 10
  ref = H_element
FEATURE [App::DocumentObjectGroupPython] C_element142  label="C_element : 087"  # scripted group (container) (typed FeaturePython)
  n = 9
  ref = C_element
FEATURE [App::DocumentObjectGroupPython] N_element061  label="N_element : 033"  # scripted group (container) (typed FeaturePython)
  n = 3
  ref = N_element
FEATURE [App::DocumentObjectGroupPython] O_element122  label="O_element : 075"  # scripted group (container) (typed FeaturePython)
  n = 5
  ref = O_element
FEATURE [App::DocumentObjectGroupPython] G4_DNA_CYTIDINE  # scripted group (container) (typed FeaturePython)
  Dunit = g/cm3
  Dvalue = 1
  Group = -> [H_element132,C_element142,N_element061,O_element122]
  conduct = 2
  density = 1
  expand = 3
  formula = G4_DNA_CYTIDINE
  name = G4_DNA_CYTIDINE
  specific = 4
FEATURE [App::DocumentObjectGroupPython] H_element133  label="H_element : 080"  # scripted group (container) (typed FeaturePython)
  n = 9
  ref = H_element
FEATURE [App::DocumentObjectGroupPython] C_element143  label="C_element : 088"  # scripted group (container) (typed FeaturePython)
  n = 9
  ref = C_element
FEATURE [App::DocumentObjectGroupPython] N_element062  label="N_element : 034"  # scripted group (container) (typed FeaturePython)
  n = 2
  ref = N_element
FEATURE [App::DocumentObjectGroupPython] O_element123  label="O_element : 076"  # scripted group (container) (typed FeaturePython)
  n = 6
  ref = O_element
FEATURE [App::DocumentObjectGroupPython] G4_DNA_URIDINE  # scripted group (container) (typed FeaturePython)
  Dunit = g/cm3
  Dvalue = 1
  Group = -> [H_element133,C_element143,N_element062,O_element123]
  conduct = 2
  density = 1
  expand = 3
  formula = G4_DNA_URIDINE
  name = G4_DNA_URIDINE
  specific = 4
FEATURE [App::DocumentObjectGroupPython] H_element134  label="H_element : 081"  # scripted group (container) (typed FeaturePython)
  n = 11
  ref = H_element
FEATURE [App::DocumentObjectGroupPython] C_element144  label="C_element : 089"  # scripted group (container) (typed FeaturePython)
  n = 10
  ref = C_element
FEATURE [App::DocumentObjectGroupPython] N_element063  label="N_element : 035"  # scripted group (container) (typed FeaturePython)
  n = 2
  ref = N_element
FEATURE [App::DocumentObjectGroupPython] O_element124  label="O_element : 077"  # scripted group (container) (typed FeaturePython)
  n = 6
  ref = O_element
FEATURE [App::DocumentObjectGroupPython] G4_DNA_METHYLURIDINE  # scripted group (container) (typed FeaturePython)
  Dunit = g/cm3
  Dvalue = 1
  Group = -> [H_element134,C_element144,N_element063,O_element124]
  conduct = 2
  density = 1
  expand = 3
  formula = G4_DNA_METHYLURIDINE
  name = G4_DNA_METHYLURIDINE
  specific = 4
FEATURE [App::DocumentObjectGroupPython] P_element014  label="P_element : 003"  # scripted group (container) (typed FeaturePython)
  n = 1
  ref = P_element
FEATURE [App::DocumentObjectGroupPython] O_element125  label="O_element : 078"  # scripted group (container) (typed FeaturePython)
  n = 3
  ref = O_element
FEATURE [App::DocumentObjectGroupPython] G4_DNA_MONOPHOSPHATE  # scripted group (container) (typed FeaturePython)
  Dunit = g/cm3
  Dvalue = 1
  Group = -> [P_element014,O_element125]
  conduct = 2
  density = 1
  expand = 3
  formula = G4_DNA_MONOPHOSPHATE
  name = G4_DNA_MONOPHOSPHATE
  specific = 4
FEATURE [App::DocumentObjectGroupPython] H_element135  label="H_element : 082"  # scripted group (container) (typed FeaturePython)
  n = 10
  ref = H_element
FEATURE [App::DocumentObjectGroupPython] C_element145  label="C_element : 090"  # scripted group (container) (typed FeaturePython)
  n = 10
  ref = C_element
FEATURE [App::DocumentObjectGroupPython] N_element064  label="N_element : 036"  # scripted group (container) (typed FeaturePython)
  n = 5
  ref = N_element
FEATURE [App::DocumentObjectGroupPython] O_element126  label="O_element : 079"  # scripted group (container) (typed FeaturePython)
  n = 7
  ref = O_element
FEATURE [App::DocumentObjectGroupPython] P_element015  label="P_element : 004"  # scripted group (container) (typed FeaturePython)
  n = 1
  ref = P_element
FEATURE [App::DocumentObjectGroupPython] G4_DNA_A  # scripted group (container) (typed FeaturePython)
  Dunit = g/cm3
  Dvalue = 1
  Group = -> [H_element135,C_element145,N_element064,O_element126,P_element015]
  conduct = 2
  density = 1
  expand = 3
  formula = G4_DNA_A
  name = G4_DNA_A
  specific = 4
FEATURE [App::DocumentObjectGroupPython] H_element136  label="H_element : 083"  # scripted group (container) (typed FeaturePython)
  n = 10
  ref = H_element
FEATURE [App::DocumentObjectGroupPython] C_element146  label="C_element : 091"  # scripted group (container) (typed FeaturePython)
  n = 10
  ref = C_element
FEATURE [App::DocumentObjectGroupPython] N_element065  label="N_element : 037"  # scripted group (container) (typed FeaturePython)
  n = 5
  ref = N_element
FEATURE [App::DocumentObjectGroupPython] O_element127  label="O_element : 8"  # scripted group (container) (typed FeaturePython)
  n = 8
  ref = O_element
FEATURE [App::DocumentObjectGroupPython] P_element016  label="P_element : 005"  # scripted group (container) (typed FeaturePython)
  n = 1
  ref = P_element
FEATURE [App::DocumentObjectGroupPython] G4_DNA_G  # scripted group (container) (typed FeaturePython)
  Dunit = g/cm3
  Dvalue = 1
  Group = -> [H_element136,C_element146,N_element065,O_element127,P_element016]
  conduct = 2
  density = 1
  expand = 3
  formula = G4_DNA_G
  name = G4_DNA_G
  specific = 4
FEATURE [App::DocumentObjectGroupPython] H_element137  label="H_element : 084"  # scripted group (container) (typed FeaturePython)
  n = 10
  ref = H_element
FEATURE [App::DocumentObjectGroupPython] C_element147  label="C_element : 092"  # scripted group (container) (typed FeaturePython)
  n = 9
  ref = C_element
FEATURE [App::DocumentObjectGroupPython] N_element066  label="N_element : 038"  # scripted group (container) (typed FeaturePython)
  n = 3
  ref = N_element
FEATURE [App::DocumentObjectGroupPython] O_element128  label="O_element : 080"  # scripted group (container) (typed FeaturePython)
  n = 8
  ref = O_element
FEATURE [App::DocumentObjectGroupPython] P_element017  label="P_element : 006"  # scripted group (container) (typed FeaturePython)
  n = 1
  ref = P_element
FEATURE [App::DocumentObjectGroupPython] G4_DNA_C  # scripted group (container) (typed FeaturePython)
  Dunit = g/cm3
  Dvalue = 1
  Group = -> [H_element137,C_element147,N_element066,O_element128,P_element017]
  conduct = 2
  density = 1
  expand = 3
  formula = G4_DNA_C
  name = G4_DNA_C
  specific = 4
FEATURE [App::DocumentObjectGroupPython] H_element138  label="H_element : 085"  # scripted group (container) (typed FeaturePython)
  n = 9
  ref = H_element
FEATURE [App::DocumentObjectGroupPython] C_element148  label="C_element : 093"  # scripted group (container) (typed FeaturePython)
  n = 9
  ref = C_element
FEATURE [App::DocumentObjectGroupPython] N_element067  label="N_element : 039"  # scripted group (container) (typed FeaturePython)
  n = 2
  ref = N_element
FEATURE [App::DocumentObjectGroupPython] O_element129  label="O_element : 9"  # scripted group (container) (typed FeaturePython)
  n = 9
  ref = O_element
FEATURE [App::DocumentObjectGroupPython] P_element018  label="P_element : 007"  # scripted group (container) (typed FeaturePython)
  n = 1
  ref = P_element
FEATURE [App::DocumentObjectGroupPython] G4_DNA_U  # scripted group (container) (typed FeaturePython)
  Dunit = g/cm3
  Dvalue = 1
  Group = -> [H_element138,C_element148,N_element067,O_element129,P_element018]
  conduct = 2
  density = 1
  expand = 3
  formula = G4_DNA_U
  name = G4_DNA_U
  specific = 4
FEATURE [App::DocumentObjectGroupPython] H_element139  label="H_element : 086"  # scripted group (container) (typed FeaturePython)
  n = 11
  ref = H_element
FEATURE [App::DocumentObjectGroupPython] C_element149  label="C_element : 094"  # scripted group (container) (typed FeaturePython)
  n = 10
  ref = C_element
FEATURE [App::DocumentObjectGroupPython] N_element068  label="N_element : 040"  # scripted group (container) (typed FeaturePython)
  n = 2
  ref = N_element
FEATURE [App::DocumentObjectGroupPython] O_element130  label="O_element : 081"  # scripted group (container) (typed FeaturePython)
  n = 9
  ref = O_element
FEATURE [App::DocumentObjectGroupPython] P_element019  label="P_element : 008"  # scripted group (container) (typed FeaturePython)
  n = 1
  ref = P_element
FEATURE [App::DocumentObjectGroupPython] G4_DNA_MU  # scripted group (container) (typed FeaturePython)
  Dunit = g/cm3
  Dvalue = 1
  Group = -> [H_element139,C_element149,N_element068,O_element130,P_element019]
  conduct = 2
  density = 1
  expand = 3
  formula = G4_DNA_MU
  name = G4_DNA_MU
  specific = 4
FEATURE [App::DocumentObjectGroupPython] BioChemical  # scripted group (container) (typed FeaturePython)
  Group = -> [G4_CYTOSINE,G4_THYMINE,G4_URACIL,G4_DNA_ADENINE,G4_DNA_GUANINE,G4_DNA_CYTOSINE,G4_DNA_THYMINE,G4_DNA_URACIL,G4_DNA_ADENOSINE,G4_DNA_GUANOSINE,G4_DNA_CYTIDINE,G4_DNA_URIDINE,G4_DNA_METHYLURIDINE,G4_DNA_MONOPHOSPHATE,G4_DNA_A,G4_DNA_G,G4_DNA_C,G4_DNA_U,G4_DNA_MU]
FEATURE [App::DocumentObjectGroupPython] G4Materials  # scripted group (container) (typed FeaturePython)
  Group = -> [NIST,Element,HEP,Space,BioChemical]
  version = 1
FEATURE [App::DocumentObjectGroupPython] Geant4  # scripted group (container) (typed FeaturePython)
  Group = -> [G4Isotopes,G4Elements,G4Materials]
FEATURE [App::DocumentObjectGroupPython] Materials  # scripted group (container) (typed FeaturePython)
  Group = -> [Geant4]
FEATURE [Part::FeaturePython] GDMLBox_WorldBox  # WARN: FeaturePython — macro-defined, semantics opaque (R4)
  lunit = 2
  material = 5
  x = 403
  y = 429
  z = 130
FEATURE [Part::FeaturePython] GDMLBox_Box  # WARN: FeaturePython — macro-defined, semantics opaque (R4)
  Placement = pos=(30,0,0) rot=(0,0,1;0rad)
  lunit = 2
  material = 0
  x = 10
  y = 10
  z = 10
FEATURE [Part::FeaturePython] GDMLTorus  # WARN: FeaturePython — macro-defined, semantics opaque (R4)
  Placement = pos=(30,0,0) rot=(0,1,0;1.5708rad)
  aunit = deg
  deltaphi = 360
  lunit = 2
  material = 0
  rmax = 2
  rmin = 0
  rtor = 8
  startphi = 0
FEATURE [Part::MultiFuse] Fusion
  Shapes = -> [GDMLBox_Box,GDMLTorus]
FEATURE [Part::FeaturePython] Array  # Draft array (typed FeaturePython)
  AlwaysSyncPlacement = false
  Angle = 180
  ArrayType = 1
  Axis = (0,0,1)
  Base = -> Fusion
  Center = (-10,0,0)
  Count = 5
  ExpandArray = false
  Fuse = false
  IntervalAxis = (0,0,0)
  IntervalX = (50,0,0)
  IntervalY = (0,50,0)
  IntervalZ = (0,0,50)
  NumberCircles = 3
  NumberPolar = 5
  NumberX = 2
  NumberY = 2
  NumberZ = 1
  PlacementList = 5 placements: [(0,0,0),(-2.92893,7.07107,0),(-10,10,0),(-17.0711,7.07107,0),(-20,1.22465e-15,0)]
  RadialDistance = 50
  ScaleList = (5) [(1,1,1),(1,1,1),(1,1,1),(1,1,1),(1,1,1)]
  Symmetry = 1
  TangentialDistance = 25
FEATURE [Part::FeaturePython] Array001  # Draft array (typed FeaturePython)
  AlwaysSyncPlacement = false
  Angle = 360
  ArrayType = 0
  Axis = (0,0,1)
  Base = -> Array
  Center = (0,0,0)
  Count = 4
  ExpandArray = false
  Fuse = true
  IntervalAxis = (0,0,0)
  IntervalX = (120,0,0)
  IntervalY = (0,120,0)
  IntervalZ = (0,0,100)
  NumberCircles = 3
  NumberPolar = 5
  NumberX = 2
  NumberY = 2
  NumberZ = 1
  PlacementList = 4 placements: [(0,0,0),(0,120,0),(120,0,0),(120,120,0)]
  RadialDistance = 50
  ScaleList = (4) [(1,1,1),(1,1,1),(1,1,1),(1,1,1)]
  Symmetry = 1
  TangentialDistance = 25
FEATURE [App::Part] Part001
  Group = -> [Array,GDMLBox_Box,GDMLTorus,Fusion,Array001]
  Origin = -> Origin004
FEATURE [App::Part] worldVOL
  Group = -> [GDMLBox_WorldBox,Part001]
  Origin = -> Origin
